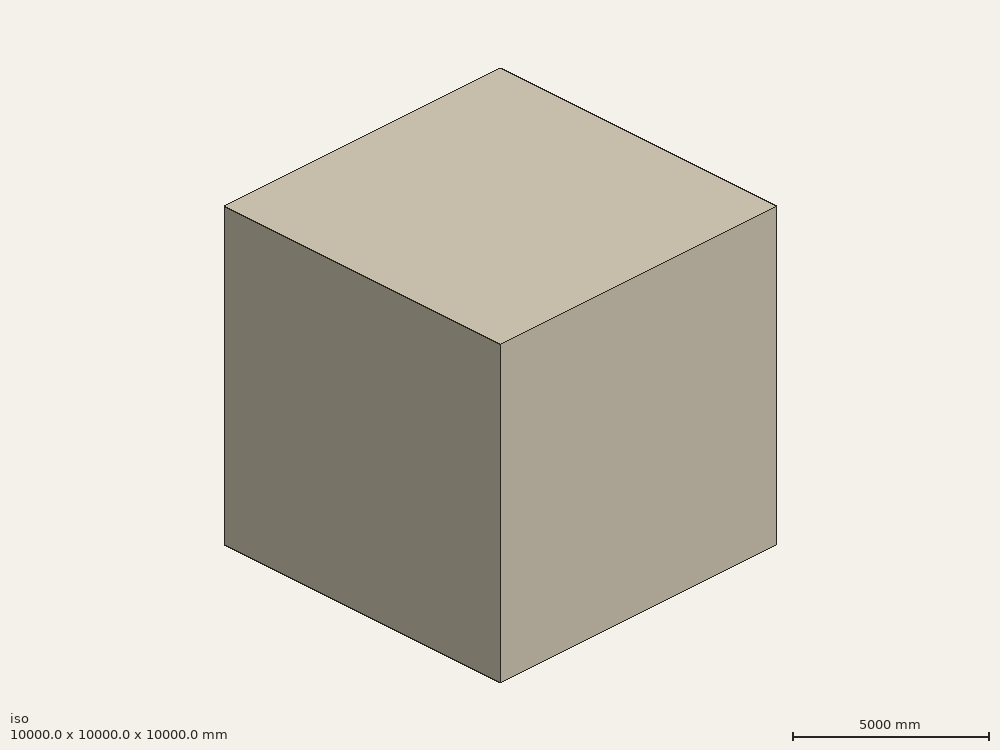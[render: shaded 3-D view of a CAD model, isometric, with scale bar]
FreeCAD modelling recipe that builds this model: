
FCSTD DOCUMENT  (FreeCAD 0.21R33694 (Git))
Label: vol31
License: All rights reserved
objects: App::DocumentObjectGroupPython×1265, Part::FeaturePython×4, App::Part×2, Part::Fuse×1, Part::Cut×1
note: 6 computed .brp shape members not serialized (recipe doc carries the construction recipe); baked Part::Feature solids carry a one-line shape summary decoded from their .brp

FEATURE [App::DocumentObjectGroupPython] HALFPI  # scripted group (container) (typed FeaturePython)
  name = HALFPI
  value = pi/2.
FEATURE [App::DocumentObjectGroupPython] PI  # scripted group (container) (typed FeaturePython)
  name = PI
  value = 1.*pi
FEATURE [App::DocumentObjectGroupPython] TWOPI  # scripted group (container) (typed FeaturePython)
  name = TWOPI
  value = 2.*pi
FEATURE [App::DocumentObjectGroupPython] Constants  # scripted group (container) (typed FeaturePython)
  Group = -> [HALFPI,PI,TWOPI]
FEATURE [App::DocumentObjectGroupPython] Variables  # scripted group (container) (typed FeaturePython)
FEATURE [App::DocumentObjectGroupPython] ro  # scripted group (container) (typed FeaturePython)
  name = ro
  type = density
  unit = g/cm3
  value = 1234
FEATURE [App::DocumentObjectGroupPython] sizeoft500  # scripted group (container) (typed FeaturePython)
  name = sizeoft500
  type = length
  unit = mm
  value = 500
FEATURE [App::DocumentObjectGroupPython] wextent  # scripted group (container) (typed FeaturePython)
  name = wextent
  type = length
  unit = mm
  value = 10000
FEATURE [App::DocumentObjectGroupPython] Quantities  # scripted group (container) (typed FeaturePython)
  Group = -> [ro,sizeoft500,wextent]
FEATURE [App::DocumentObjectGroupPython] Isotopes  # scripted group (container) (typed FeaturePython)
FEATURE [App::DocumentObjectGroupPython] Hydrogen  # scripted group (container) (typed FeaturePython)
  Z = 1
  atom_value = 1.01
  formula = H
  name = Hydrogen
FEATURE [App::DocumentObjectGroupPython] Oxygen  # scripted group (container) (typed FeaturePython)
  Z = 8
  atom_value = 16
  formula = O
  name = Oxygen
FEATURE [App::DocumentObjectGroupPython] Nitrogen  # scripted group (container) (typed FeaturePython)
  Z = 7
  atom_value = 14.01
  formula = N
  name = Nitrogen
FEATURE [App::DocumentObjectGroupPython] Lead  # scripted group (container) (typed FeaturePython)
  Z = 82
  atom_value = 207.2
  formula = Pb
  name = Lead
FEATURE [App::DocumentObjectGroupPython] Elements  # scripted group (container) (typed FeaturePython)
  Group = -> [Hydrogen,Oxygen,Nitrogen,Lead]
FEATURE [App::DocumentObjectGroupPython] Al  # scripted group (container) (typed FeaturePython)
  Dvalue = 2.7
  Z = 13
  atom_value = 26.98
  conduct = 2
  density = 1
  expand = 3
  name = Al
  specific = 4
FEATURE [App::DocumentObjectGroupPython] Hydrogen001  label="Hydrogen : 2"  # scripted group (container) (typed FeaturePython)
  n = 2
  ref = Hydrogen
FEATURE [App::DocumentObjectGroupPython] Oxygen001  label="Oxygen : 1"  # scripted group (container) (typed FeaturePython)
  n = 1
  ref = Oxygen
FEATURE [App::DocumentObjectGroupPython] Water  # scripted group (container) (typed FeaturePython)
  Dvalue = 1
  Group = -> [Hydrogen001,Oxygen001]
  conduct = 2
  density = 1
  expand = 3
  formula = H20
  name = Water
  specific = 4
FEATURE [App::DocumentObjectGroupPython] Nitrogen001  label="Nitrogen : 0.700"  # scripted group (container) (typed FeaturePython)
  n = 0.7
FEATURE [App::DocumentObjectGroupPython] Oxygen002  label="Oxygen : 0.300"  # scripted group (container) (typed FeaturePython)
  n = 0.3
FEATURE [App::DocumentObjectGroupPython] Air  # scripted group (container) (typed FeaturePython)
  Dunit = mg/cm3
  Dvalue = 1.29
  Group = -> [Nitrogen001,Oxygen002]
  conduct = 2
  density = 1
  expand = 3
  name = Air
  specific = 4
FEATURE [App::DocumentObjectGroupPython] Matrix  # scripted group (container) (typed FeaturePython)
FEATURE [App::DocumentObjectGroupPython] Surfaces  # scripted group (container) (typed FeaturePython)
FEATURE [App::DocumentObjectGroupPython] Opticals  # scripted group (container) (typed FeaturePython)
  Group = -> [Matrix,Surfaces]
FEATURE [App::DocumentObjectGroupPython] G4Isotopes  # scripted group (container) (typed FeaturePython)
FEATURE [App::DocumentObjectGroupPython] H_element  # scripted group (container) (typed FeaturePython)
  Z = 1
  atom_value = 1.008
  formula = H
  name = H_element
FEATURE [App::DocumentObjectGroupPython] He_element  # scripted group (container) (typed FeaturePython)
  Z = 2
  atom_value = 4.0026
  formula = He
  name = He_element
FEATURE [App::DocumentObjectGroupPython] Li_element  # scripted group (container) (typed FeaturePython)
  Z = 3
  atom_value = 6.94
  formula = Li
  name = Li_element
FEATURE [App::DocumentObjectGroupPython] Be_element  # scripted group (container) (typed FeaturePython)
  Z = 4
  atom_value = 9.01218
  formula = Be
  name = Be_element
FEATURE [App::DocumentObjectGroupPython] B_element  # scripted group (container) (typed FeaturePython)
  Z = 5
  atom_value = 10.81
  formula = B
  name = B_element
FEATURE [App::DocumentObjectGroupPython] C_element  # scripted group (container) (typed FeaturePython)
  Z = 6
  atom_value = 12.011
  formula = C
  name = C_element
FEATURE [App::DocumentObjectGroupPython] N_element  # scripted group (container) (typed FeaturePython)
  Z = 7
  atom_value = 14.007
  formula = N
  name = N_element
FEATURE [App::DocumentObjectGroupPython] O_element  # scripted group (container) (typed FeaturePython)
  Z = 8
  atom_value = 15.999
  formula = O
  name = O_element
FEATURE [App::DocumentObjectGroupPython] F_element  # scripted group (container) (typed FeaturePython)
  Z = 9
  atom_value = 18.9984
  formula = F
  name = F_element
FEATURE [App::DocumentObjectGroupPython] Ne_element  # scripted group (container) (typed FeaturePython)
  Z = 10
  atom_value = 20.1797
  formula = Ne
  name = Ne_element
FEATURE [App::DocumentObjectGroupPython] Na_element  # scripted group (container) (typed FeaturePython)
  Z = 11
  atom_value = 22.9898
  formula = Na
  name = Na_element
FEATURE [App::DocumentObjectGroupPython] Mg_element  # scripted group (container) (typed FeaturePython)
  Z = 12
  atom_value = 24.305
  formula = Mg
  name = Mg_element
FEATURE [App::DocumentObjectGroupPython] Al_element  # scripted group (container) (typed FeaturePython)
  Z = 13
  atom_value = 26.9815
  formula = Al
  name = Al_element
FEATURE [App::DocumentObjectGroupPython] Si_element  # scripted group (container) (typed FeaturePython)
  Z = 14
  atom_value = 28.085
  formula = Si
  name = Si_element
FEATURE [App::DocumentObjectGroupPython] P_element  # scripted group (container) (typed FeaturePython)
  Z = 15
  atom_value = 30.9738
  formula = P
  name = P_element
FEATURE [App::DocumentObjectGroupPython] S_element  # scripted group (container) (typed FeaturePython)
  Z = 16
  atom_value = 32.06
  formula = S
  name = S_element
FEATURE [App::DocumentObjectGroupPython] Cl_element  # scripted group (container) (typed FeaturePython)
  Z = 17
  atom_value = 35.45
  formula = Cl
  name = Cl_element
FEATURE [App::DocumentObjectGroupPython] Ar_element  # scripted group (container) (typed FeaturePython)
  Z = 18
  atom_value = 39.95
  formula = Ar
  name = Ar_element
FEATURE [App::DocumentObjectGroupPython] K_element  # scripted group (container) (typed FeaturePython)
  Z = 19
  atom_value = 39.0983
  formula = K
  name = K_element
FEATURE [App::DocumentObjectGroupPython] Ca_element  # scripted group (container) (typed FeaturePython)
  Z = 20
  atom_value = 40.078
  formula = Ca
  name = Ca_element
FEATURE [App::DocumentObjectGroupPython] Sc_element  # scripted group (container) (typed FeaturePython)
  Z = 21
  atom_value = 44.9559
  formula = Sc
  name = Sc_element
FEATURE [App::DocumentObjectGroupPython] Ti_element  # scripted group (container) (typed FeaturePython)
  Z = 22
  atom_value = 47.867
  formula = Ti
  name = Ti_element
FEATURE [App::DocumentObjectGroupPython] V_element  # scripted group (container) (typed FeaturePython)
  Z = 23
  atom_value = 50.9415
  formula = V
  name = V_element
FEATURE [App::DocumentObjectGroupPython] Cr_element  # scripted group (container) (typed FeaturePython)
  Z = 24
  atom_value = 51.9961
  formula = Cr
  name = Cr_element
FEATURE [App::DocumentObjectGroupPython] Mn_element  # scripted group (container) (typed FeaturePython)
  Z = 25
  atom_value = 54.938
  formula = Mn
  name = Mn_element
FEATURE [App::DocumentObjectGroupPython] Fe_element  # scripted group (container) (typed FeaturePython)
  Z = 26
  atom_value = 55.845
  formula = Fe
  name = Fe_element
FEATURE [App::DocumentObjectGroupPython] Co_element  # scripted group (container) (typed FeaturePython)
  Z = 27
  atom_value = 58.9332
  formula = Co
  name = Co_element
FEATURE [App::DocumentObjectGroupPython] Ni_element  # scripted group (container) (typed FeaturePython)
  Z = 28
  atom_value = 58.6934
  formula = Ni
  name = Ni_element
FEATURE [App::DocumentObjectGroupPython] Cu_element  # scripted group (container) (typed FeaturePython)
  Z = 29
  atom_value = 63.546
  formula = Cu
  name = Cu_element
FEATURE [App::DocumentObjectGroupPython] Zn_element  # scripted group (container) (typed FeaturePython)
  Z = 30
  atom_value = 65.38
  formula = Zn
  name = Zn_element
FEATURE [App::DocumentObjectGroupPython] Ga_element  # scripted group (container) (typed FeaturePython)
  Z = 31
  atom_value = 69.723
  formula = Ga
  name = Ga_element
FEATURE [App::DocumentObjectGroupPython] Ge_element  # scripted group (container) (typed FeaturePython)
  Z = 32
  atom_value = 72.63
  formula = Ge
  name = Ge_element
FEATURE [App::DocumentObjectGroupPython] As_element  # scripted group (container) (typed FeaturePython)
  Z = 33
  atom_value = 74.9216
  formula = As
  name = As_element
FEATURE [App::DocumentObjectGroupPython] Se_element  # scripted group (container) (typed FeaturePython)
  Z = 34
  atom_value = 78.971
  formula = Se
  name = Se_element
FEATURE [App::DocumentObjectGroupPython] Br_element  # scripted group (container) (typed FeaturePython)
  Z = 35
  atom_value = 79.904
  formula = Br
  name = Br_element
FEATURE [App::DocumentObjectGroupPython] Kr_element  # scripted group (container) (typed FeaturePython)
  Z = 36
  atom_value = 83.798
  formula = Kr
  name = Kr_element
FEATURE [App::DocumentObjectGroupPython] Rb_element  # scripted group (container) (typed FeaturePython)
  Z = 37
  atom_value = 85.4678
  formula = Rb
  name = Rb_element
FEATURE [App::DocumentObjectGroupPython] Sr_element  # scripted group (container) (typed FeaturePython)
  Z = 38
  atom_value = 87.62
  formula = Sr
  name = Sr_element
FEATURE [App::DocumentObjectGroupPython] Y_element  # scripted group (container) (typed FeaturePython)
  Z = 39
  atom_value = 88.9058
  formula = Y
  name = Y_element
FEATURE [App::DocumentObjectGroupPython] Zr_element  # scripted group (container) (typed FeaturePython)
  Z = 40
  atom_value = 91.224
  formula = Zr
  name = Zr_element
FEATURE [App::DocumentObjectGroupPython] Nb_element  # scripted group (container) (typed FeaturePython)
  Z = 41
  atom_value = 92.9064
  formula = Nb
  name = Nb_element
FEATURE [App::DocumentObjectGroupPython] Mo_element  # scripted group (container) (typed FeaturePython)
  Z = 42
  atom_value = 95.95
  formula = Mo
  name = Mo_element
FEATURE [App::DocumentObjectGroupPython] Tc_element  # scripted group (container) (typed FeaturePython)
  Z = 43
  atom_value = 97
  formula = Tc
  name = Tc_element
FEATURE [App::DocumentObjectGroupPython] Ru_element  # scripted group (container) (typed FeaturePython)
  Z = 44
  atom_value = 101.07
  formula = Ru
  name = Ru_element
FEATURE [App::DocumentObjectGroupPython] Rh_element  # scripted group (container) (typed FeaturePython)
  Z = 45
  atom_value = 102.905
  formula = Rh
  name = Rh_element
FEATURE [App::DocumentObjectGroupPython] Pd_element  # scripted group (container) (typed FeaturePython)
  Z = 46
  atom_value = 106.42
  formula = Pd
  name = Pd_element
FEATURE [App::DocumentObjectGroupPython] Ag_element  # scripted group (container) (typed FeaturePython)
  Z = 47
  atom_value = 107.868
  formula = Ag
  name = Ag_element
FEATURE [App::DocumentObjectGroupPython] Cd_element  # scripted group (container) (typed FeaturePython)
  Z = 48
  atom_value = 112.414
  formula = Cd
  name = Cd_element
FEATURE [App::DocumentObjectGroupPython] In_element  # scripted group (container) (typed FeaturePython)
  Z = 49
  atom_value = 114.818
  formula = In
  name = In_element
FEATURE [App::DocumentObjectGroupPython] Sn_element  # scripted group (container) (typed FeaturePython)
  Z = 50
  atom_value = 118.71
  formula = Sn
  name = Sn_element
FEATURE [App::DocumentObjectGroupPython] Sb_element  # scripted group (container) (typed FeaturePython)
  Z = 51
  atom_value = 121.76
  formula = Sb
  name = Sb_element
FEATURE [App::DocumentObjectGroupPython] Te_element  # scripted group (container) (typed FeaturePython)
  Z = 52
  atom_value = 127.6
  formula = Te
  name = Te_element
FEATURE [App::DocumentObjectGroupPython] I_element  # scripted group (container) (typed FeaturePython)
  Z = 53
  atom_value = 126.904
  formula = I
  name = I_element
FEATURE [App::DocumentObjectGroupPython] Xe_element  # scripted group (container) (typed FeaturePython)
  Z = 54
  atom_value = 131.293
  formula = Xe
  name = Xe_element
FEATURE [App::DocumentObjectGroupPython] Cs_element  # scripted group (container) (typed FeaturePython)
  Z = 55
  atom_value = 132.905
  formula = Cs
  name = Cs_element
FEATURE [App::DocumentObjectGroupPython] Ba_element  # scripted group (container) (typed FeaturePython)
  Z = 56
  atom_value = 137.327
  formula = Ba
  name = Ba_element
FEATURE [App::DocumentObjectGroupPython] La_element  # scripted group (container) (typed FeaturePython)
  Z = 57
  atom_value = 138.905
  formula = La
  name = La_element
FEATURE [App::DocumentObjectGroupPython] Ce_element  # scripted group (container) (typed FeaturePython)
  Z = 58
  atom_value = 140.116
  formula = Ce
  name = Ce_element
FEATURE [App::DocumentObjectGroupPython] Pr_element  # scripted group (container) (typed FeaturePython)
  Z = 59
  atom_value = 140.908
  formula = Pr
  name = Pr_element
FEATURE [App::DocumentObjectGroupPython] Nd_element  # scripted group (container) (typed FeaturePython)
  Z = 60
  atom_value = 144.242
  formula = Nd
  name = Nd_element
FEATURE [App::DocumentObjectGroupPython] Pm_element  # scripted group (container) (typed FeaturePython)
  Z = 61
  atom_value = 145
  formula = Pm
  name = Pm_element
FEATURE [App::DocumentObjectGroupPython] Sm_element  # scripted group (container) (typed FeaturePython)
  Z = 62
  atom_value = 150.36
  formula = Sm
  name = Sm_element
FEATURE [App::DocumentObjectGroupPython] Eu_element  # scripted group (container) (typed FeaturePython)
  Z = 63
  atom_value = 151.964
  formula = Eu
  name = Eu_element
FEATURE [App::DocumentObjectGroupPython] Gd_element  # scripted group (container) (typed FeaturePython)
  Z = 64
  atom_value = 157.25
  formula = Gd
  name = Gd_element
FEATURE [App::DocumentObjectGroupPython] Tb_element  # scripted group (container) (typed FeaturePython)
  Z = 65
  atom_value = 158.925
  formula = Tb
  name = Tb_element
FEATURE [App::DocumentObjectGroupPython] Dy_element  # scripted group (container) (typed FeaturePython)
  Z = 66
  atom_value = 162.5
  formula = Dy
  name = Dy_element
FEATURE [App::DocumentObjectGroupPython] Ho_element  # scripted group (container) (typed FeaturePython)
  Z = 67
  atom_value = 164.93
  formula = Ho
  name = Ho_element
FEATURE [App::DocumentObjectGroupPython] Er_element  # scripted group (container) (typed FeaturePython)
  Z = 68
  atom_value = 167.259
  formula = Er
  name = Er_element
FEATURE [App::DocumentObjectGroupPython] Tm_element  # scripted group (container) (typed FeaturePython)
  Z = 69
  atom_value = 168.934
  formula = Tm
  name = Tm_element
FEATURE [App::DocumentObjectGroupPython] Yb_element  # scripted group (container) (typed FeaturePython)
  Z = 70
  atom_value = 173.045
  formula = Yb
  name = Yb_element
FEATURE [App::DocumentObjectGroupPython] Lu_element  # scripted group (container) (typed FeaturePython)
  Z = 71
  atom_value = 174.967
  formula = Lu
  name = Lu_element
FEATURE [App::DocumentObjectGroupPython] Hf_element  # scripted group (container) (typed FeaturePython)
  Z = 72
  atom_value = 178.49
  formula = Hf
  name = Hf_element
FEATURE [App::DocumentObjectGroupPython] Ta_element  # scripted group (container) (typed FeaturePython)
  Z = 73
  atom_value = 180.948
  formula = Ta
  name = Ta_element
FEATURE [App::DocumentObjectGroupPython] W_element  # scripted group (container) (typed FeaturePython)
  Z = 74
  atom_value = 183.84
  formula = W
  name = W_element
FEATURE [App::DocumentObjectGroupPython] Re_element  # scripted group (container) (typed FeaturePython)
  Z = 75
  atom_value = 186.207
  formula = Re
  name = Re_element
FEATURE [App::DocumentObjectGroupPython] Os_element  # scripted group (container) (typed FeaturePython)
  Z = 76
  atom_value = 190.23
  formula = Os
  name = Os_element
FEATURE [App::DocumentObjectGroupPython] Ir_element  # scripted group (container) (typed FeaturePython)
  Z = 77
  atom_value = 192.217
  formula = Ir
  name = Ir_element
FEATURE [App::DocumentObjectGroupPython] Pt_element  # scripted group (container) (typed FeaturePython)
  Z = 78
  atom_value = 195.084
  formula = Pt
  name = Pt_element
FEATURE [App::DocumentObjectGroupPython] Au_element  # scripted group (container) (typed FeaturePython)
  Z = 79
  atom_value = 196.967
  formula = Au
  name = Au_element
FEATURE [App::DocumentObjectGroupPython] Hg_element  # scripted group (container) (typed FeaturePython)
  Z = 80
  atom_value = 200.592
  formula = Hg
  name = Hg_element
FEATURE [App::DocumentObjectGroupPython] Tl_element  # scripted group (container) (typed FeaturePython)
  Z = 81
  atom_value = 204.38
  formula = Tl
  name = Tl_element
FEATURE [App::DocumentObjectGroupPython] Pb_element  # scripted group (container) (typed FeaturePython)
  Z = 82
  atom_value = 207.2
  formula = Pb
  name = Pb_element
FEATURE [App::DocumentObjectGroupPython] Bi_element  # scripted group (container) (typed FeaturePython)
  Z = 83
  atom_value = 208.98
  formula = Bi
  name = Bi_element
FEATURE [App::DocumentObjectGroupPython] Po_element  # scripted group (container) (typed FeaturePython)
  Z = 84
  atom_value = 209
  formula = Po
  name = Po_element
FEATURE [App::DocumentObjectGroupPython] At_element  # scripted group (container) (typed FeaturePython)
  Z = 85
  atom_value = 210
  formula = At
  name = At_element
FEATURE [App::DocumentObjectGroupPython] Rn_element  # scripted group (container) (typed FeaturePython)
  Z = 86
  atom_value = 222
  formula = Rn
  name = Rn_element
FEATURE [App::DocumentObjectGroupPython] Fr_element  # scripted group (container) (typed FeaturePython)
  Z = 87
  atom_value = 223
  formula = Fr
  name = Fr_element
FEATURE [App::DocumentObjectGroupPython] Ra_element  # scripted group (container) (typed FeaturePython)
  Z = 88
  atom_value = 226
  formula = Ra
  name = Ra_element
FEATURE [App::DocumentObjectGroupPython] Ac_element  # scripted group (container) (typed FeaturePython)
  Z = 89
  atom_value = 227
  formula = Ac
  name = Ac_element
FEATURE [App::DocumentObjectGroupPython] Th_element  # scripted group (container) (typed FeaturePython)
  Z = 90
  atom_value = 232.038
  formula = Th
  name = Th_element
FEATURE [App::DocumentObjectGroupPython] Pa_element  # scripted group (container) (typed FeaturePython)
  Z = 91
  atom_value = 231.036
  formula = Pa
  name = Pa_element
FEATURE [App::DocumentObjectGroupPython] U_element  # scripted group (container) (typed FeaturePython)
  Z = 92
  atom_value = 238.029
  formula = U
  name = U_element
FEATURE [App::DocumentObjectGroupPython] Np_element  # scripted group (container) (typed FeaturePython)
  Z = 93
  atom_value = 237
  formula = Np
  name = Np_element
FEATURE [App::DocumentObjectGroupPython] Pu_element  # scripted group (container) (typed FeaturePython)
  Z = 94
  atom_value = 244
  formula = Pu
  name = Pu_element
FEATURE [App::DocumentObjectGroupPython] Am_element  # scripted group (container) (typed FeaturePython)
  Z = 95
  atom_value = 243
  formula = Am
  name = Am_element
FEATURE [App::DocumentObjectGroupPython] Cm_element  # scripted group (container) (typed FeaturePython)
  Z = 96
  atom_value = 247
  formula = Cm
  name = Cm_element
FEATURE [App::DocumentObjectGroupPython] Bk_element  # scripted group (container) (typed FeaturePython)
  Z = 97
  atom_value = 247
  formula = Bk
  name = Bk_element
FEATURE [App::DocumentObjectGroupPython] Cf_element  # scripted group (container) (typed FeaturePython)
  Z = 98
  atom_value = 251
  formula = Cf
  name = Cf_element
FEATURE [App::DocumentObjectGroupPython] G4Elements  # scripted group (container) (typed FeaturePython)
  Group = -> [H_element,He_element,Li_element,Be_element,B_element,C_element,N_element,O_element,F_element,Ne_element,Na_element,Mg_element,Al_element,Si_element,P_element,S_element,Cl_element,Ar_element,K_element,Ca_element,Sc_element,Ti_element,V_element,Cr_element,Mn_element,Fe_element,Co_element,Ni_element,Cu_element,Zn_element,Ga_element,Ge_element,As_element,Se_element,Br_element,Kr_element,Rb_element,+61 more]
FEATURE [App::DocumentObjectGroupPython] H_element001  label="H_element : 0.101"  # scripted group (container) (typed FeaturePython)
  n = 0.101327
FEATURE [App::DocumentObjectGroupPython] C_element001  label="C_element : 0.775"  # scripted group (container) (typed FeaturePython)
  n = 0.7755
FEATURE [App::DocumentObjectGroupPython] N_element001  label="N_element : 0.035"  # scripted group (container) (typed FeaturePython)
  n = 0.035057
FEATURE [App::DocumentObjectGroupPython] O_element001  label="O_element : 0.052"  # scripted group (container) (typed FeaturePython)
  n = 0.0523159
FEATURE [App::DocumentObjectGroupPython] F_element001  label="F_element : 0.017"  # scripted group (container) (typed FeaturePython)
  n = 0.017422
FEATURE [App::DocumentObjectGroupPython] Ca_element001  label="Ca_element : 0.018"  # scripted group (container) (typed FeaturePython)
  n = 0.018378
FEATURE [App::DocumentObjectGroupPython] G4_A_150_TISSUE  label="G4_A-150_TISSUE"  # scripted group (container) (typed FeaturePython)
  Dunit = g/cm3
  Dvalue = 1.127
  Group = -> [H_element001,C_element001,N_element001,O_element001,F_element001,Ca_element001]
  conduct = 2
  density = 1
  expand = 3
  formula = G4_A-150_TISSUE
  name = G4_A-150_TISSUE
  specific = 4
FEATURE [App::DocumentObjectGroupPython] C_element002  label="C_element : 3"  # scripted group (container) (typed FeaturePython)
  n = 3
  ref = C_element
FEATURE [App::DocumentObjectGroupPython] H_element002  label="H_element : 6"  # scripted group (container) (typed FeaturePython)
  n = 6
  ref = H_element
FEATURE [App::DocumentObjectGroupPython] O_element002  label="O_element : 1"  # scripted group (container) (typed FeaturePython)
  n = 1
  ref = O_element
FEATURE [App::DocumentObjectGroupPython] G4_ACETONE  # scripted group (container) (typed FeaturePython)
  Dunit = g/cm3
  Dvalue = 0.7899
  Group = -> [C_element002,H_element002,O_element002]
  conduct = 2
  density = 1
  expand = 3
  formula = G4_ACETONE
  name = G4_ACETONE
  specific = 4
FEATURE [App::DocumentObjectGroupPython] C_element003  label="C_element : 2"  # scripted group (container) (typed FeaturePython)
  n = 2
  ref = C_element
FEATURE [App::DocumentObjectGroupPython] H_element003  label="H_element : 2"  # scripted group (container) (typed FeaturePython)
  n = 2
  ref = H_element
FEATURE [App::DocumentObjectGroupPython] G4_ACETYLENE  # scripted group (container) (typed FeaturePython)
  Dunit = g/cm3
  Dvalue = 0.0010967
  Group = -> [C_element003,H_element003]
  conduct = 2
  density = 1
  expand = 3
  formula = G4_ACETYLENE
  name = G4_ACETYLENE
  specific = 4
FEATURE [App::DocumentObjectGroupPython] C_element004  label="C_element : 5"  # scripted group (container) (typed FeaturePython)
  n = 5
  ref = C_element
FEATURE [App::DocumentObjectGroupPython] H_element004  label="H_element : 5"  # scripted group (container) (typed FeaturePython)
  n = 5
  ref = H_element
FEATURE [App::DocumentObjectGroupPython] N_element002  label="N_element : 5"  # scripted group (container) (typed FeaturePython)
  n = 5
  ref = N_element
FEATURE [App::DocumentObjectGroupPython] G4_ADENINE  # scripted group (container) (typed FeaturePython)
  Dunit = g/cm3
  Dvalue = 1.6
  Group = -> [C_element004,H_element004,N_element002]
  conduct = 2
  density = 1
  expand = 3
  formula = G4_ADENINE
  name = G4_ADENINE
  specific = 4
FEATURE [App::DocumentObjectGroupPython] H_element005  label="H_element : 0.114"  # scripted group (container) (typed FeaturePython)
  n = 0.114
FEATURE [App::DocumentObjectGroupPython] C_element005  label="C_element : 0.598"  # scripted group (container) (typed FeaturePython)
  n = 0.598
FEATURE [App::DocumentObjectGroupPython] N_element003  label="N_element : 0.007"  # scripted group (container) (typed FeaturePython)
  n = 0.007
FEATURE [App::DocumentObjectGroupPython] O_element003  label="O_element : 0.278"  # scripted group (container) (typed FeaturePython)
  n = 0.278
FEATURE [App::DocumentObjectGroupPython] Na_element001  label="Na_element : 0.001"  # scripted group (container) (typed FeaturePython)
  n = 0.001
FEATURE [App::DocumentObjectGroupPython] S_element001  label="S_element : 0.001"  # scripted group (container) (typed FeaturePython)
  n = 0.001
FEATURE [App::DocumentObjectGroupPython] Cl_element001  label="Cl_element : 0.001"  # scripted group (container) (typed FeaturePython)
  n = 0.001
FEATURE [App::DocumentObjectGroupPython] G4_ADIPOSE_TISSUE_ICRP  # scripted group (container) (typed FeaturePython)
  Dunit = g/cm3
  Dvalue = 0.95
  Group = -> [H_element005,C_element005,N_element003,O_element003,Na_element001,S_element001,Cl_element001]
  conduct = 2
  density = 1
  expand = 3
  formula = G4_ADIPOSE_TISSUE_ICRP
  name = G4_ADIPOSE_TISSUE_ICRP
  specific = 4
FEATURE [App::DocumentObjectGroupPython] C_element006  label="C_element : 0.000"  # scripted group (container) (typed FeaturePython)
  n = 0.000124
FEATURE [App::DocumentObjectGroupPython] N_element004  label="N_element : 0.755"  # scripted group (container) (typed FeaturePython)
  n = 0.755268
FEATURE [App::DocumentObjectGroupPython] O_element004  label="O_element : 0.232"  # scripted group (container) (typed FeaturePython)
  n = 0.231781
FEATURE [App::DocumentObjectGroupPython] Ar_element001  label="Ar_element : 0.013"  # scripted group (container) (typed FeaturePython)
  n = 0.012827
FEATURE [App::DocumentObjectGroupPython] G4_AIR  # scripted group (container) (typed FeaturePython)
  Dunit = g/cm3
  Dvalue = 0.00120479
  Group = -> [C_element006,N_element004,O_element004,Ar_element001]
  conduct = 2
  density = 1
  expand = 3
  formula = G4_AIR
  name = G4_AIR
  specific = 4
FEATURE [App::DocumentObjectGroupPython] C_element007  label="C_element : 006"  # scripted group (container) (typed FeaturePython)
  n = 3
  ref = C_element
FEATURE [App::DocumentObjectGroupPython] H_element006  label="H_element : 7"  # scripted group (container) (typed FeaturePython)
  n = 7
  ref = H_element
FEATURE [App::DocumentObjectGroupPython] N_element005  label="N_element : 1"  # scripted group (container) (typed FeaturePython)
  n = 1
  ref = N_element
FEATURE [App::DocumentObjectGroupPython] O_element005  label="O_element : 2"  # scripted group (container) (typed FeaturePython)
  n = 2
  ref = O_element
FEATURE [App::DocumentObjectGroupPython] G4_ALANINE  # scripted group (container) (typed FeaturePython)
  Dunit = g/cm3
  Dvalue = 1.42
  Group = -> [C_element007,H_element006,N_element005,O_element005]
  conduct = 2
  density = 1
  expand = 3
  formula = G4_ALANINE
  name = G4_ALANINE
  specific = 4
FEATURE [App::DocumentObjectGroupPython] Al_element001  label="Al_element : 2"  # scripted group (container) (typed FeaturePython)
  n = 2
  ref = Al_element
FEATURE [App::DocumentObjectGroupPython] O_element006  label="O_element : 3"  # scripted group (container) (typed FeaturePython)
  n = 3
  ref = O_element
FEATURE [App::DocumentObjectGroupPython] G4_ALUMINUM_OXIDE  # scripted group (container) (typed FeaturePython)
  Dunit = g/cm3
  Dvalue = 3.97
  Group = -> [Al_element001,O_element006]
  conduct = 2
  density = 1
  expand = 3
  formula = G4_ALUMINUM_OXIDE
  name = G4_ALUMINUM_OXIDE
  specific = 4
FEATURE [App::DocumentObjectGroupPython] H_element007  label="H_element : 0.106"  # scripted group (container) (typed FeaturePython)
  n = 0.10593
FEATURE [App::DocumentObjectGroupPython] C_element008  label="C_element : 0.789"  # scripted group (container) (typed FeaturePython)
  n = 0.788974
FEATURE [App::DocumentObjectGroupPython] O_element007  label="O_element : 0.105"  # scripted group (container) (typed FeaturePython)
  n = 0.105096
FEATURE [App::DocumentObjectGroupPython] G4_AMBER  # scripted group (container) (typed FeaturePython)
  Dunit = g/cm3
  Dvalue = 1.1
  Group = -> [H_element007,C_element008,O_element007]
  conduct = 2
  density = 1
  expand = 3
  formula = G4_AMBER
  name = G4_AMBER
  specific = 4
FEATURE [App::DocumentObjectGroupPython] N_element006  label="N_element : 006"  # scripted group (container) (typed FeaturePython)
  n = 1
  ref = N_element
FEATURE [App::DocumentObjectGroupPython] H_element008  label="H_element : 3"  # scripted group (container) (typed FeaturePython)
  n = 3
  ref = H_element
FEATURE [App::DocumentObjectGroupPython] G4_AMMONIA  # scripted group (container) (typed FeaturePython)
  Dunit = g/cm3
  Dvalue = 0.000826019
  Group = -> [N_element006,H_element008]
  conduct = 2
  density = 1
  expand = 3
  formula = G4_AMMONIA
  name = G4_AMMONIA
  specific = 4
FEATURE [App::DocumentObjectGroupPython] C_element009  label="C_element : 6"  # scripted group (container) (typed FeaturePython)
  n = 6
  ref = C_element
FEATURE [App::DocumentObjectGroupPython] H_element009  label="H_element : 008"  # scripted group (container) (typed FeaturePython)
  n = 7
  ref = H_element
FEATURE [App::DocumentObjectGroupPython] N_element007  label="N_element : 007"  # scripted group (container) (typed FeaturePython)
  n = 1
  ref = N_element
FEATURE [App::DocumentObjectGroupPython] G4_ANILINE  # scripted group (container) (typed FeaturePython)
  Dunit = g/cm3
  Dvalue = 1.0235
  Group = -> [C_element009,H_element009,N_element007]
  conduct = 2
  density = 1
  expand = 3
  formula = G4_ANILINE
  name = G4_ANILINE
  specific = 4
FEATURE [App::DocumentObjectGroupPython] C_element010  label="C_element : 14"  # scripted group (container) (typed FeaturePython)
  n = 14
  ref = C_element
FEATURE [App::DocumentObjectGroupPython] H_element010  label="H_element : 10"  # scripted group (container) (typed FeaturePython)
  n = 10
  ref = H_element
FEATURE [App::DocumentObjectGroupPython] G4_ANTHRACENE  # scripted group (container) (typed FeaturePython)
  Dunit = g/cm3
  Dvalue = 1.283
  Group = -> [C_element010,H_element010]
  conduct = 2
  density = 1
  expand = 3
  formula = G4_ANTHRACENE
  name = G4_ANTHRACENE
  specific = 4
FEATURE [App::DocumentObjectGroupPython] H_element011  label="H_element : 0.065"  # scripted group (container) (typed FeaturePython)
  n = 0.0654709
FEATURE [App::DocumentObjectGroupPython] C_element011  label="C_element : 0.537"  # scripted group (container) (typed FeaturePython)
  n = 0.536944
FEATURE [App::DocumentObjectGroupPython] N_element008  label="N_element : 0.021"  # scripted group (container) (typed FeaturePython)
  n = 0.0215
FEATURE [App::DocumentObjectGroupPython] O_element008  label="O_element : 0.032"  # scripted group (container) (typed FeaturePython)
  n = 0.032085
FEATURE [App::DocumentObjectGroupPython] F_element002  label="F_element : 0.167"  # scripted group (container) (typed FeaturePython)
  n = 0.167411
FEATURE [App::DocumentObjectGroupPython] Ca_element002  label="Ca_element : 0.177"  # scripted group (container) (typed FeaturePython)
  n = 0.176589
FEATURE [App::DocumentObjectGroupPython] G4_B_100_BONE  label="G4_B-100_BONE"  # scripted group (container) (typed FeaturePython)
  Dunit = g/cm3
  Dvalue = 1.45
  Group = -> [H_element011,C_element011,N_element008,O_element008,F_element002,Ca_element002]
  conduct = 2
  density = 1
  expand = 3
  formula = G4_B-100_BONE
  name = G4_B-100_BONE
  specific = 4
FEATURE [App::DocumentObjectGroupPython] H_element012  label="H_element : 0.057"  # scripted group (container) (typed FeaturePython)
  n = 0.057441
FEATURE [App::DocumentObjectGroupPython] C_element012  label="C_element : 0.790"  # scripted group (container) (typed FeaturePython)
  n = 0.774591
FEATURE [App::DocumentObjectGroupPython] O_element009  label="O_element : 0.168"  # scripted group (container) (typed FeaturePython)
  n = 0.167968
FEATURE [App::DocumentObjectGroupPython] G4_BAKELITE  # scripted group (container) (typed FeaturePython)
  Dunit = g/cm3
  Dvalue = 1.25
  Group = -> [H_element012,C_element012,O_element009]
  conduct = 2
  density = 1
  expand = 3
  formula = G4_BAKELITE
  name = G4_BAKELITE
  specific = 4
FEATURE [App::DocumentObjectGroupPython] Ba_element001  label="Ba_element : 1"  # scripted group (container) (typed FeaturePython)
  n = 1
  ref = Ba_element
FEATURE [App::DocumentObjectGroupPython] F_element003  label="F_element : 2"  # scripted group (container) (typed FeaturePython)
  n = 2
  ref = F_element
FEATURE [App::DocumentObjectGroupPython] G4_BARIUM_FLUORIDE  # scripted group (container) (typed FeaturePython)
  Dunit = g/cm3
  Dvalue = 4.89
  Group = -> [Ba_element001,F_element003]
  conduct = 2
  density = 1
  expand = 3
  formula = G4_BARIUM_FLUORIDE
  name = G4_BARIUM_FLUORIDE
  specific = 4
FEATURE [App::DocumentObjectGroupPython] Ba_element002  label="Ba_element : 002"  # scripted group (container) (typed FeaturePython)
  n = 1
  ref = Ba_element
FEATURE [App::DocumentObjectGroupPython] S_element002  label="S_element : 1"  # scripted group (container) (typed FeaturePython)
  n = 1
  ref = S_element
FEATURE [App::DocumentObjectGroupPython] O_element010  label="O_element : 4"  # scripted group (container) (typed FeaturePython)
  n = 4
  ref = O_element
FEATURE [App::DocumentObjectGroupPython] G4_BARIUM_SULFATE  # scripted group (container) (typed FeaturePython)
  Dunit = g/cm3
  Dvalue = 4.5
  Group = -> [Ba_element002,S_element002,O_element010]
  conduct = 2
  density = 1
  expand = 3
  formula = G4_BARIUM_SULFATE
  name = G4_BARIUM_SULFATE
  specific = 4
FEATURE [App::DocumentObjectGroupPython] C_element013  label="C_element : 007"  # scripted group (container) (typed FeaturePython)
  n = 6
  ref = C_element
FEATURE [App::DocumentObjectGroupPython] H_element013  label="H_element : 009"  # scripted group (container) (typed FeaturePython)
  n = 6
  ref = H_element
FEATURE [App::DocumentObjectGroupPython] G4_BENZENE  # scripted group (container) (typed FeaturePython)
  Dunit = g/cm3
  Dvalue = 0.87865
  Group = -> [C_element013,H_element013]
  conduct = 2
  density = 1
  expand = 3
  formula = G4_BENZENE
  name = G4_BENZENE
  specific = 4
FEATURE [App::DocumentObjectGroupPython] Be_element001  label="Be_element : 1"  # scripted group (container) (typed FeaturePython)
  n = 1
  ref = Be_element
FEATURE [App::DocumentObjectGroupPython] O_element011  label="O_element : 005"  # scripted group (container) (typed FeaturePython)
  n = 1
  ref = O_element
FEATURE [App::DocumentObjectGroupPython] G4_BERYLLIUM_OXIDE  # scripted group (container) (typed FeaturePython)
  Dunit = g/cm3
  Dvalue = 3.01
  Group = -> [Be_element001,O_element011]
  conduct = 2
  density = 1
  expand = 3
  formula = G4_BERYLLIUM_OXIDE
  name = G4_BERYLLIUM_OXIDE
  specific = 4
FEATURE [App::DocumentObjectGroupPython] Bi_element001  label="Bi_element : 4"  # scripted group (container) (typed FeaturePython)
  n = 4
  ref = Bi_element
FEATURE [App::DocumentObjectGroupPython] Ge_element001  label="Ge_element : 3"  # scripted group (container) (typed FeaturePython)
  n = 3
  ref = Ge_element
FEATURE [App::DocumentObjectGroupPython] O_element012  label="O_element : 12"  # scripted group (container) (typed FeaturePython)
  n = 12
  ref = O_element
FEATURE [App::DocumentObjectGroupPython] G4_BGO  # scripted group (container) (typed FeaturePython)
  Dunit = g/cm3
  Dvalue = 7.13
  Group = -> [Bi_element001,Ge_element001,O_element012]
  conduct = 2
  density = 1
  expand = 3
  formula = G4_BGO
  name = G4_BGO
  specific = 4
FEATURE [App::DocumentObjectGroupPython] H_element014  label="H_element : 0.102"  # scripted group (container) (typed FeaturePython)
  n = 0.102
FEATURE [App::DocumentObjectGroupPython] C_element014  label="C_element : 0.110"  # scripted group (container) (typed FeaturePython)
  n = 0.11
FEATURE [App::DocumentObjectGroupPython] N_element009  label="N_element : 0.033"  # scripted group (container) (typed FeaturePython)
  n = 0.033
FEATURE [App::DocumentObjectGroupPython] O_element013  label="O_element : 0.745"  # scripted group (container) (typed FeaturePython)
  n = 0.745
FEATURE [App::DocumentObjectGroupPython] Na_element002  label="Na_element : 0.002"  # scripted group (container) (typed FeaturePython)
  n = 0.001
FEATURE [App::DocumentObjectGroupPython] P_element001  label="P_element : 0.001"  # scripted group (container) (typed FeaturePython)
  n = 0.001
FEATURE [App::DocumentObjectGroupPython] S_element003  label="S_element : 0.002"  # scripted group (container) (typed FeaturePython)
  n = 0.002
FEATURE [App::DocumentObjectGroupPython] Cl_element002  label="Cl_element : 0.003"  # scripted group (container) (typed FeaturePython)
  n = 0.003
FEATURE [App::DocumentObjectGroupPython] K_element001  label="K_element : 0.002"  # scripted group (container) (typed FeaturePython)
  n = 0.002
FEATURE [App::DocumentObjectGroupPython] Fe_element001  label="Fe_element : 0.001"  # scripted group (container) (typed FeaturePython)
  n = 0.001
FEATURE [App::DocumentObjectGroupPython] G4_BLOOD_ICRP  # scripted group (container) (typed FeaturePython)
  Dunit = g/cm3
  Dvalue = 1.06
  Group = -> [H_element014,C_element014,N_element009,O_element013,Na_element002,P_element001,S_element003,Cl_element002,K_element001,Fe_element001]
  conduct = 2
  density = 1
  expand = 3
  formula = G4_BLOOD_ICRP
  name = G4_BLOOD_ICRP
  specific = 4
FEATURE [App::DocumentObjectGroupPython] H_element015  label="H_element : 0.064"  # scripted group (container) (typed FeaturePython)
  n = 0.064
FEATURE [App::DocumentObjectGroupPython] C_element015  label="C_element : 0.278"  # scripted group (container) (typed FeaturePython)
  n = 0.278
FEATURE [App::DocumentObjectGroupPython] N_element010  label="N_element : 0.027"  # scripted group (container) (typed FeaturePython)
  n = 0.027
FEATURE [App::DocumentObjectGroupPython] O_element014  label="O_element : 0.410"  # scripted group (container) (typed FeaturePython)
  n = 0.41
FEATURE [App::DocumentObjectGroupPython] Mg_element001  label="Mg_element : 0.002"  # scripted group (container) (typed FeaturePython)
  n = 0.002
FEATURE [App::DocumentObjectGroupPython] P_element002  label="P_element : 0.070"  # scripted group (container) (typed FeaturePython)
  n = 0.07
FEATURE [App::DocumentObjectGroupPython] S_element004  label="S_element : 0.003"  # scripted group (container) (typed FeaturePython)
  n = 0.002
FEATURE [App::DocumentObjectGroupPython] Ca_element003  label="Ca_element : 0.147"  # scripted group (container) (typed FeaturePython)
  n = 0.147
FEATURE [App::DocumentObjectGroupPython] G4_BONE_COMPACT_ICRU  # scripted group (container) (typed FeaturePython)
  Dunit = g/cm3
  Dvalue = 1.85
  Group = -> [H_element015,C_element015,N_element010,O_element014,Mg_element001,P_element002,S_element004,Ca_element003]
  conduct = 2
  density = 1
  expand = 3
  formula = G4_BONE_COMPACT_ICRU
  name = G4_BONE_COMPACT_ICRU
  specific = 4
FEATURE [App::DocumentObjectGroupPython] H_element016  label="H_element : 0.034"  # scripted group (container) (typed FeaturePython)
  n = 0.034
FEATURE [App::DocumentObjectGroupPython] C_element016  label="C_element : 0.155"  # scripted group (container) (typed FeaturePython)
  n = 0.155
FEATURE [App::DocumentObjectGroupPython] N_element011  label="N_element : 0.042"  # scripted group (container) (typed FeaturePython)
  n = 0.042
FEATURE [App::DocumentObjectGroupPython] O_element015  label="O_element : 0.435"  # scripted group (container) (typed FeaturePython)
  n = 0.435
FEATURE [App::DocumentObjectGroupPython] Na_element003  label="Na_element : 0.003"  # scripted group (container) (typed FeaturePython)
  n = 0.001
FEATURE [App::DocumentObjectGroupPython] Mg_element002  label="Mg_element : 0.003"  # scripted group (container) (typed FeaturePython)
  n = 0.002
FEATURE [App::DocumentObjectGroupPython] P_element003  label="P_element : 0.103"  # scripted group (container) (typed FeaturePython)
  n = 0.103
FEATURE [App::DocumentObjectGroupPython] S_element005  label="S_element : 0.004"  # scripted group (container) (typed FeaturePython)
  n = 0.003
FEATURE [App::DocumentObjectGroupPython] Ca_element004  label="Ca_element : 0.225"  # scripted group (container) (typed FeaturePython)
  n = 0.225
FEATURE [App::DocumentObjectGroupPython] G4_BONE_CORTICAL_ICRP  # scripted group (container) (typed FeaturePython)
  Dunit = g/cm3
  Dvalue = 1.92
  Group = -> [H_element016,C_element016,N_element011,O_element015,Na_element003,Mg_element002,P_element003,S_element005,Ca_element004]
  conduct = 2
  density = 1
  expand = 3
  formula = G4_BONE_CORTICAL_ICRP
  name = G4_BONE_CORTICAL_ICRP
  specific = 4
FEATURE [App::DocumentObjectGroupPython] B_element001  label="B_element : 4"  # scripted group (container) (typed FeaturePython)
  n = 4
  ref = B_element
FEATURE [App::DocumentObjectGroupPython] C_element017  label="C_element : 1"  # scripted group (container) (typed FeaturePython)
  n = 1
  ref = C_element
FEATURE [App::DocumentObjectGroupPython] G4_BORON_CARBIDE  # scripted group (container) (typed FeaturePython)
  Dunit = g/cm3
  Dvalue = 2.52
  Group = -> [B_element001,C_element017]
  conduct = 2
  density = 1
  expand = 3
  formula = G4_BORON_CARBIDE
  name = G4_BORON_CARBIDE
  specific = 4
FEATURE [App::DocumentObjectGroupPython] B_element002  label="B_element : 2"  # scripted group (container) (typed FeaturePython)
  n = 2
  ref = B_element
FEATURE [App::DocumentObjectGroupPython] O_element016  label="O_element : 006"  # scripted group (container) (typed FeaturePython)
  n = 3
  ref = O_element
FEATURE [App::DocumentObjectGroupPython] G4_BORON_OXIDE  # scripted group (container) (typed FeaturePython)
  Dunit = g/cm3
  Dvalue = 1.812
  Group = -> [B_element002,O_element016]
  conduct = 2
  density = 1
  expand = 3
  formula = G4_BORON_OXIDE
  name = G4_BORON_OXIDE
  specific = 4
FEATURE [App::DocumentObjectGroupPython] H_element017  label="H_element : 0.107"  # scripted group (container) (typed FeaturePython)
  n = 0.107
FEATURE [App::DocumentObjectGroupPython] C_element018  label="C_element : 0.145"  # scripted group (container) (typed FeaturePython)
  n = 0.145
FEATURE [App::DocumentObjectGroupPython] N_element012  label="N_element : 0.022"  # scripted group (container) (typed FeaturePython)
  n = 0.022
FEATURE [App::DocumentObjectGroupPython] O_element017  label="O_element : 0.712"  # scripted group (container) (typed FeaturePython)
  n = 0.712
FEATURE [App::DocumentObjectGroupPython] Na_element004  label="Na_element : 0.004"  # scripted group (container) (typed FeaturePython)
  n = 0.002
FEATURE [App::DocumentObjectGroupPython] P_element004  label="P_element : 0.004"  # scripted group (container) (typed FeaturePython)
  n = 0.004
FEATURE [App::DocumentObjectGroupPython] S_element006  label="S_element : 0.005"  # scripted group (container) (typed FeaturePython)
  n = 0.002
FEATURE [App::DocumentObjectGroupPython] Cl_element003  label="Cl_element : 0.004"  # scripted group (container) (typed FeaturePython)
  n = 0.003
FEATURE [App::DocumentObjectGroupPython] K_element002  label="K_element : 0.003"  # scripted group (container) (typed FeaturePython)
  n = 0.003
FEATURE [App::DocumentObjectGroupPython] G4_BRAIN_ICRP  # scripted group (container) (typed FeaturePython)
  Dunit = g/cm3
  Dvalue = 1.04
  Group = -> [H_element017,C_element018,N_element012,O_element017,Na_element004,P_element004,S_element006,Cl_element003,K_element002]
  conduct = 2
  density = 1
  expand = 3
  formula = G4_BRAIN_ICRP
  name = G4_BRAIN_ICRP
  specific = 4
FEATURE [App::DocumentObjectGroupPython] C_element019  label="C_element : 4"  # scripted group (container) (typed FeaturePython)
  n = 4
  ref = C_element
FEATURE [App::DocumentObjectGroupPython] H_element018  label="H_element : 010"  # scripted group (container) (typed FeaturePython)
  n = 10
  ref = H_element
FEATURE [App::DocumentObjectGroupPython] G4_BUTANE  # scripted group (container) (typed FeaturePython)
  Dunit = g/cm3
  Dvalue = 0.00249343
  Group = -> [C_element019,H_element018]
  conduct = 2
  density = 1
  expand = 3
  formula = G4_BUTANE
  name = G4_BUTANE
  specific = 4
FEATURE [App::DocumentObjectGroupPython] C_element020  label="C_element : 008"  # scripted group (container) (typed FeaturePython)
  n = 4
  ref = C_element
FEATURE [App::DocumentObjectGroupPython] H_element019  label="H_element : 011"  # scripted group (container) (typed FeaturePython)
  n = 10
  ref = H_element
FEATURE [App::DocumentObjectGroupPython] O_element018  label="O_element : 007"  # scripted group (container) (typed FeaturePython)
  n = 1
  ref = O_element
FEATURE [App::DocumentObjectGroupPython] G4_N_BUTYL_ALCOHOL  label="G4_N-BUTYL_ALCOHOL"  # scripted group (container) (typed FeaturePython)
  Dunit = g/cm3
  Dvalue = 0.8098
  Group = -> [C_element020,H_element019,O_element018]
  conduct = 2
  density = 1
  expand = 3
  formula = G4_N-BUTYL_ALCOHOL
  name = G4_N-BUTYL_ALCOHOL
  specific = 4
FEATURE [App::DocumentObjectGroupPython] H_element020  label="H_element : 0.025"  # scripted group (container) (typed FeaturePython)
  n = 0.02468
FEATURE [App::DocumentObjectGroupPython] C_element021  label="C_element : 0.502"  # scripted group (container) (typed FeaturePython)
  n = 0.501611
FEATURE [App::DocumentObjectGroupPython] O_element019  label="O_element : 0.005"  # scripted group (container) (typed FeaturePython)
  n = 0.004527
FEATURE [App::DocumentObjectGroupPython] F_element004  label="F_element : 0.465"  # scripted group (container) (typed FeaturePython)
  n = 0.465209
FEATURE [App::DocumentObjectGroupPython] Si_element001  label="Si_element : 0.004"  # scripted group (container) (typed FeaturePython)
  n = 0.003973
FEATURE [App::DocumentObjectGroupPython] G4_C_552  label="G4_C-552"  # scripted group (container) (typed FeaturePython)
  Dunit = g/cm3
  Dvalue = 1.76
  Group = -> [H_element020,C_element021,O_element019,F_element004,Si_element001]
  conduct = 2
  density = 1
  expand = 3
  formula = G4_C-552
  name = G4_C-552
  specific = 4
FEATURE [App::DocumentObjectGroupPython] Cd_element001  label="Cd_element : 1"  # scripted group (container) (typed FeaturePython)
  n = 1
  ref = Cd_element
FEATURE [App::DocumentObjectGroupPython] Te_element001  label="Te_element : 1"  # scripted group (container) (typed FeaturePython)
  n = 1
  ref = Te_element
FEATURE [App::DocumentObjectGroupPython] G4_CADMIUM_TELLURIDE  # scripted group (container) (typed FeaturePython)
  Dunit = g/cm3
  Dvalue = 6.2
  Group = -> [Cd_element001,Te_element001]
  conduct = 2
  density = 1
  expand = 3
  formula = G4_CADMIUM_TELLURIDE
  name = G4_CADMIUM_TELLURIDE
  specific = 4
FEATURE [App::DocumentObjectGroupPython] Cd_element002  label="Cd_element : 002"  # scripted group (container) (typed FeaturePython)
  n = 1
  ref = Cd_element
FEATURE [App::DocumentObjectGroupPython] W_element001  label="W_element : 1"  # scripted group (container) (typed FeaturePython)
  n = 1
  ref = W_element
FEATURE [App::DocumentObjectGroupPython] O_element020  label="O_element : 008"  # scripted group (container) (typed FeaturePython)
  n = 4
  ref = O_element
FEATURE [App::DocumentObjectGroupPython] G4_CADMIUM_TUNGSTATE  # scripted group (container) (typed FeaturePython)
  Dunit = g/cm3
  Dvalue = 7.9
  Group = -> [Cd_element002,W_element001,O_element020]
  conduct = 2
  density = 1
  expand = 3
  formula = G4_CADMIUM_TUNGSTATE
  name = G4_CADMIUM_TUNGSTATE
  specific = 4
FEATURE [App::DocumentObjectGroupPython] Ca_element005  label="Ca_element : 1"  # scripted group (container) (typed FeaturePython)
  n = 1
  ref = Ca_element
FEATURE [App::DocumentObjectGroupPython] C_element022  label="C_element : 009"  # scripted group (container) (typed FeaturePython)
  n = 1
  ref = C_element
FEATURE [App::DocumentObjectGroupPython] O_element021  label="O_element : 009"  # scripted group (container) (typed FeaturePython)
  n = 3
  ref = O_element
FEATURE [App::DocumentObjectGroupPython] G4_CALCIUM_CARBONATE  # scripted group (container) (typed FeaturePython)
  Dunit = g/cm3
  Dvalue = 2.8
  Group = -> [Ca_element005,C_element022,O_element021]
  conduct = 2
  density = 1
  expand = 3
  formula = G4_CALCIUM_CARBONATE
  name = G4_CALCIUM_CARBONATE
  specific = 4
FEATURE [App::DocumentObjectGroupPython] Ca_element006  label="Ca_element : 002"  # scripted group (container) (typed FeaturePython)
  n = 1
  ref = Ca_element
FEATURE [App::DocumentObjectGroupPython] F_element005  label="F_element : 003"  # scripted group (container) (typed FeaturePython)
  n = 2
  ref = F_element
FEATURE [App::DocumentObjectGroupPython] G4_CALCIUM_FLUORIDE  # scripted group (container) (typed FeaturePython)
  Dunit = g/cm3
  Dvalue = 3.18
  Group = -> [Ca_element006,F_element005]
  conduct = 2
  density = 1
  expand = 3
  formula = G4_CALCIUM_FLUORIDE
  name = G4_CALCIUM_FLUORIDE
  specific = 4
FEATURE [App::DocumentObjectGroupPython] Ca_element007  label="Ca_element : 003"  # scripted group (container) (typed FeaturePython)
  n = 1
  ref = Ca_element
FEATURE [App::DocumentObjectGroupPython] O_element022  label="O_element : 010"  # scripted group (container) (typed FeaturePython)
  n = 1
  ref = O_element
FEATURE [App::DocumentObjectGroupPython] G4_CALCIUM_OXIDE  # scripted group (container) (typed FeaturePython)
  Dunit = g/cm3
  Dvalue = 3.3
  Group = -> [Ca_element007,O_element022]
  conduct = 2
  density = 1
  expand = 3
  formula = G4_CALCIUM_OXIDE
  name = G4_CALCIUM_OXIDE
  specific = 4
FEATURE [App::DocumentObjectGroupPython] Ca_element008  label="Ca_element : 004"  # scripted group (container) (typed FeaturePython)
  n = 1
  ref = Ca_element
FEATURE [App::DocumentObjectGroupPython] S_element007  label="S_element : 002"  # scripted group (container) (typed FeaturePython)
  n = 1
  ref = S_element
FEATURE [App::DocumentObjectGroupPython] O_element023  label="O_element : 011"  # scripted group (container) (typed FeaturePython)
  n = 4
  ref = O_element
FEATURE [App::DocumentObjectGroupPython] G4_CALCIUM_SULFATE  # scripted group (container) (typed FeaturePython)
  Dunit = g/cm3
  Dvalue = 2.96
  Group = -> [Ca_element008,S_element007,O_element023]
  conduct = 2
  density = 1
  expand = 3
  formula = G4_CALCIUM_SULFATE
  name = G4_CALCIUM_SULFATE
  specific = 4
FEATURE [App::DocumentObjectGroupPython] Ca_element009  label="Ca_element : 005"  # scripted group (container) (typed FeaturePython)
  n = 1
  ref = Ca_element
FEATURE [App::DocumentObjectGroupPython] W_element002  label="W_element : 002"  # scripted group (container) (typed FeaturePython)
  n = 1
  ref = W_element
FEATURE [App::DocumentObjectGroupPython] O_element024  label="O_element : 012"  # scripted group (container) (typed FeaturePython)
  n = 4
  ref = O_element
FEATURE [App::DocumentObjectGroupPython] G4_CALCIUM_TUNGSTATE  # scripted group (container) (typed FeaturePython)
  Dunit = g/cm3
  Dvalue = 6.062
  Group = -> [Ca_element009,W_element002,O_element024]
  conduct = 2
  density = 1
  expand = 3
  formula = G4_CALCIUM_TUNGSTATE
  name = G4_CALCIUM_TUNGSTATE
  specific = 4
FEATURE [App::DocumentObjectGroupPython] C_element023  label="C_element : 010"  # scripted group (container) (typed FeaturePython)
  n = 1
  ref = C_element
FEATURE [App::DocumentObjectGroupPython] O_element025  label="O_element : 013"  # scripted group (container) (typed FeaturePython)
  n = 2
  ref = O_element
FEATURE [App::DocumentObjectGroupPython] G4_CARBON_DIOXIDE  # scripted group (container) (typed FeaturePython)
  Dunit = g/cm3
  Dvalue = 0.00184212
  Group = -> [C_element023,O_element025]
  conduct = 2
  density = 1
  expand = 3
  formula = G4_CARBON_DIOXIDE
  name = G4_CARBON_DIOXIDE
  specific = 4
FEATURE [App::DocumentObjectGroupPython] C_element024  label="C_element : 011"  # scripted group (container) (typed FeaturePython)
  n = 1
  ref = C_element
FEATURE [App::DocumentObjectGroupPython] Cl_element004  label="Cl_element : 4"  # scripted group (container) (typed FeaturePython)
  n = 4
  ref = Cl_element
FEATURE [App::DocumentObjectGroupPython] G4_CARBON_TETRACHLORIDE  # scripted group (container) (typed FeaturePython)
  Dunit = g/cm3
  Dvalue = 1.594
  Group = -> [C_element024,Cl_element004]
  conduct = 2
  density = 1
  expand = 3
  formula = G4_CARBON_TETRACHLORIDE
  name = G4_CARBON_TETRACHLORIDE
  specific = 4
FEATURE [App::DocumentObjectGroupPython] C_element025  label="C_element : 012"  # scripted group (container) (typed FeaturePython)
  n = 6
  ref = C_element
FEATURE [App::DocumentObjectGroupPython] H_element021  label="H_element : 012"  # scripted group (container) (typed FeaturePython)
  n = 10
  ref = H_element
FEATURE [App::DocumentObjectGroupPython] O_element026  label="O_element : 5"  # scripted group (container) (typed FeaturePython)
  n = 5
  ref = O_element
FEATURE [App::DocumentObjectGroupPython] G4_CELLULOSE_CELLOPHANE  # scripted group (container) (typed FeaturePython)
  Dunit = g/cm3
  Dvalue = 1.42
  Group = -> [C_element025,H_element021,O_element026]
  conduct = 2
  density = 1
  expand = 3
  formula = G4_CELLULOSE_CELLOPHANE
  name = G4_CELLULOSE_CELLOPHANE
  specific = 4
FEATURE [App::DocumentObjectGroupPython] H_element022  label="H_element : 0.067"  # scripted group (container) (typed FeaturePython)
  n = 0.067125
FEATURE [App::DocumentObjectGroupPython] C_element026  label="C_element : 0.545"  # scripted group (container) (typed FeaturePython)
  n = 0.545403
FEATURE [App::DocumentObjectGroupPython] O_element027  label="O_element : 0.387"  # scripted group (container) (typed FeaturePython)
  n = 0.387472
FEATURE [App::DocumentObjectGroupPython] G4_CELLULOSE_BUTYRATE  # scripted group (container) (typed FeaturePython)
  Dunit = g/cm3
  Dvalue = 1.2
  Group = -> [H_element022,C_element026,O_element027]
  conduct = 2
  density = 1
  expand = 3
  formula = G4_CELLULOSE_BUTYRATE
  name = G4_CELLULOSE_BUTYRATE
  specific = 4
FEATURE [App::DocumentObjectGroupPython] H_element023  label="H_element : 0.029"  # scripted group (container) (typed FeaturePython)
  n = 0.029216
FEATURE [App::DocumentObjectGroupPython] C_element027  label="C_element : 0.271"  # scripted group (container) (typed FeaturePython)
  n = 0.271296
FEATURE [App::DocumentObjectGroupPython] N_element013  label="N_element : 0.121"  # scripted group (container) (typed FeaturePython)
  n = 0.121276
FEATURE [App::DocumentObjectGroupPython] O_element028  label="O_element : 0.578"  # scripted group (container) (typed FeaturePython)
  n = 0.578212
FEATURE [App::DocumentObjectGroupPython] G4_CELLULOSE_NITRATE  # scripted group (container) (typed FeaturePython)
  Dunit = g/cm3
  Dvalue = 1.49
  Group = -> [H_element023,C_element027,N_element013,O_element028]
  conduct = 2
  density = 1
  expand = 3
  formula = G4_CELLULOSE_NITRATE
  name = G4_CELLULOSE_NITRATE
  specific = 4
FEATURE [App::DocumentObjectGroupPython] H_element024  label="H_element : 0.108"  # scripted group (container) (typed FeaturePython)
  n = 0.107596
FEATURE [App::DocumentObjectGroupPython] N_element014  label="N_element : 0.001"  # scripted group (container) (typed FeaturePython)
  n = 0.0008
FEATURE [App::DocumentObjectGroupPython] O_element029  label="O_element : 0.875"  # scripted group (container) (typed FeaturePython)
  n = 0.874976
FEATURE [App::DocumentObjectGroupPython] S_element008  label="S_element : 0.015"  # scripted group (container) (typed FeaturePython)
  n = 0.014627
FEATURE [App::DocumentObjectGroupPython] Ce_element001  label="Ce_element : 0.002"  # scripted group (container) (typed FeaturePython)
  n = 0.002001
FEATURE [App::DocumentObjectGroupPython] G4_CERIC_SULFATE  # scripted group (container) (typed FeaturePython)
  Dunit = g/cm3
  Dvalue = 1.03
  Group = -> [H_element024,N_element014,O_element029,S_element008,Ce_element001]
  conduct = 2
  density = 1
  expand = 3
  formula = G4_CERIC_SULFATE
  name = G4_CERIC_SULFATE
  specific = 4
FEATURE [App::DocumentObjectGroupPython] Cs_element001  label="Cs_element : 1"  # scripted group (container) (typed FeaturePython)
  n = 1
  ref = Cs_element
FEATURE [App::DocumentObjectGroupPython] F_element006  label="F_element : 1"  # scripted group (container) (typed FeaturePython)
  n = 1
  ref = F_element
FEATURE [App::DocumentObjectGroupPython] G4_CESIUM_FLUORIDE  # scripted group (container) (typed FeaturePython)
  Dunit = g/cm3
  Dvalue = 4.115
  Group = -> [Cs_element001,F_element006]
  conduct = 2
  density = 1
  expand = 3
  formula = G4_CESIUM_FLUORIDE
  name = G4_CESIUM_FLUORIDE
  specific = 4
FEATURE [App::DocumentObjectGroupPython] Cs_element002  label="Cs_element : 002"  # scripted group (container) (typed FeaturePython)
  n = 1
  ref = Cs_element
FEATURE [App::DocumentObjectGroupPython] I_element001  label="I_element : 1"  # scripted group (container) (typed FeaturePython)
  n = 1
  ref = I_element
FEATURE [App::DocumentObjectGroupPython] G4_CESIUM_IODIDE  # scripted group (container) (typed FeaturePython)
  Dunit = g/cm3
  Dvalue = 4.51
  Group = -> [Cs_element002,I_element001]
  conduct = 2
  density = 1
  expand = 3
  formula = G4_CESIUM_IODIDE
  name = G4_CESIUM_IODIDE
  specific = 4
FEATURE [App::DocumentObjectGroupPython] C_element028  label="C_element : 013"  # scripted group (container) (typed FeaturePython)
  n = 6
  ref = C_element
FEATURE [App::DocumentObjectGroupPython] H_element025  label="H_element : 013"  # scripted group (container) (typed FeaturePython)
  n = 5
  ref = H_element
FEATURE [App::DocumentObjectGroupPython] Cl_element005  label="Cl_element : 1"  # scripted group (container) (typed FeaturePython)
  n = 1
  ref = Cl_element
FEATURE [App::DocumentObjectGroupPython] G4_CHLOROBENZENE  # scripted group (container) (typed FeaturePython)
  Dunit = g/cm3
  Dvalue = 1.1058
  Group = -> [C_element028,H_element025,Cl_element005]
  conduct = 2
  density = 1
  expand = 3
  formula = G4_CHLOROBENZENE
  name = G4_CHLOROBENZENE
  specific = 4
FEATURE [App::DocumentObjectGroupPython] C_element029  label="C_element : 014"  # scripted group (container) (typed FeaturePython)
  n = 1
  ref = C_element
FEATURE [App::DocumentObjectGroupPython] H_element026  label="H_element : 1"  # scripted group (container) (typed FeaturePython)
  n = 1
  ref = H_element
FEATURE [App::DocumentObjectGroupPython] Cl_element006  label="Cl_element : 3"  # scripted group (container) (typed FeaturePython)
  n = 3
  ref = Cl_element
FEATURE [App::DocumentObjectGroupPython] G4_CHLOROFORM  # scripted group (container) (typed FeaturePython)
  Dunit = g/cm3
  Dvalue = 1.4832
  Group = -> [C_element029,H_element026,Cl_element006]
  conduct = 2
  density = 1
  expand = 3
  formula = G4_CHLOROFORM
  name = G4_CHLOROFORM
  specific = 4
FEATURE [App::DocumentObjectGroupPython] H_element027  label="H_element : 0.010"  # scripted group (container) (typed FeaturePython)
  n = 0.01
FEATURE [App::DocumentObjectGroupPython] C_element030  label="C_element : 0.001"  # scripted group (container) (typed FeaturePython)
  n = 0.001
FEATURE [App::DocumentObjectGroupPython] O_element030  label="O_element : 0.529"  # scripted group (container) (typed FeaturePython)
  n = 0.529107
FEATURE [App::DocumentObjectGroupPython] Na_element005  label="Na_element : 0.016"  # scripted group (container) (typed FeaturePython)
  n = 0.016
FEATURE [App::DocumentObjectGroupPython] Mg_element003  label="Mg_element : 0.004"  # scripted group (container) (typed FeaturePython)
  n = 0.002
FEATURE [App::DocumentObjectGroupPython] Al_element002  label="Al_element : 0.034"  # scripted group (container) (typed FeaturePython)
  n = 0.033872
FEATURE [App::DocumentObjectGroupPython] Si_element002  label="Si_element : 0.337"  # scripted group (container) (typed FeaturePython)
  n = 0.337021
FEATURE [App::DocumentObjectGroupPython] K_element003  label="K_element : 0.013"  # scripted group (container) (typed FeaturePython)
  n = 0.013
FEATURE [App::DocumentObjectGroupPython] Ca_element010  label="Ca_element : 0.044"  # scripted group (container) (typed FeaturePython)
  n = 0.044
FEATURE [App::DocumentObjectGroupPython] Fe_element002  label="Fe_element : 0.014"  # scripted group (container) (typed FeaturePython)
  n = 0.014
FEATURE [App::DocumentObjectGroupPython] G4_CONCRETE  # scripted group (container) (typed FeaturePython)
  Dunit = g/cm3
  Dvalue = 2.3
  Group = -> [H_element027,C_element030,O_element030,Na_element005,Mg_element003,Al_element002,Si_element002,K_element003,Ca_element010,Fe_element002]
  conduct = 2
  density = 1
  expand = 3
  formula = G4_CONCRETE
  name = G4_CONCRETE
  specific = 4
FEATURE [App::DocumentObjectGroupPython] C_element031  label="C_element : 015"  # scripted group (container) (typed FeaturePython)
  n = 6
  ref = C_element
FEATURE [App::DocumentObjectGroupPython] H_element028  label="H_element : 12"  # scripted group (container) (typed FeaturePython)
  n = 12
  ref = H_element
FEATURE [App::DocumentObjectGroupPython] G4_CYCLOHEXANE  # scripted group (container) (typed FeaturePython)
  Dunit = g/cm3
  Dvalue = 0.779
  Group = -> [C_element031,H_element028]
  conduct = 2
  density = 1
  expand = 3
  formula = G4_CYCLOHEXANE
  name = G4_CYCLOHEXANE
  specific = 4
FEATURE [App::DocumentObjectGroupPython] C_element032  label="C_element : 016"  # scripted group (container) (typed FeaturePython)
  n = 6
  ref = C_element
FEATURE [App::DocumentObjectGroupPython] H_element029  label="H_element : 4"  # scripted group (container) (typed FeaturePython)
  n = 4
  ref = H_element
FEATURE [App::DocumentObjectGroupPython] Cl_element007  label="Cl_element : 2"  # scripted group (container) (typed FeaturePython)
  n = 2
  ref = Cl_element
FEATURE [App::DocumentObjectGroupPython] G4_1_2_DICHLOROBENZENE  label="G4_1.2-DICHLOROBENZENE"  # scripted group (container) (typed FeaturePython)
  Dunit = g/cm3
  Dvalue = 1.3048
  Group = -> [C_element032,H_element029,Cl_element007]
  conduct = 2
  density = 1
  expand = 3
  formula = G4_1.2-DICHLOROBENZENE
  name = G4_1.2-DICHLOROBENZENE
  specific = 4
FEATURE [App::DocumentObjectGroupPython] C_element033  label="C_element : 017"  # scripted group (container) (typed FeaturePython)
  n = 4
  ref = C_element
FEATURE [App::DocumentObjectGroupPython] H_element030  label="H_element : 8"  # scripted group (container) (typed FeaturePython)
  n = 8
  ref = H_element
FEATURE [App::DocumentObjectGroupPython] O_element031  label="O_element : 014"  # scripted group (container) (typed FeaturePython)
  n = 1
  ref = O_element
FEATURE [App::DocumentObjectGroupPython] Cl_element008  label="Cl_element : 005"  # scripted group (container) (typed FeaturePython)
  n = 2
  ref = Cl_element
FEATURE [App::DocumentObjectGroupPython] G4_DICHLORODIETHYL_ETHER  # scripted group (container) (typed FeaturePython)
  Dunit = g/cm3
  Dvalue = 1.2199
  Group = -> [C_element033,H_element030,O_element031,Cl_element008]
  conduct = 2
  density = 1
  expand = 3
  formula = G4_DICHLORODIETHYL_ETHER
  name = G4_DICHLORODIETHYL_ETHER
  specific = 4
FEATURE [App::DocumentObjectGroupPython] C_element034  label="C_element : 018"  # scripted group (container) (typed FeaturePython)
  n = 2
  ref = C_element
FEATURE [App::DocumentObjectGroupPython] H_element031  label="H_element : 014"  # scripted group (container) (typed FeaturePython)
  n = 4
  ref = H_element
FEATURE [App::DocumentObjectGroupPython] Cl_element009  label="Cl_element : 006"  # scripted group (container) (typed FeaturePython)
  n = 2
  ref = Cl_element
FEATURE [App::DocumentObjectGroupPython] G4_1_2_DICHLOROETHANE  label="G4_1.2-DICHLOROETHANE"  # scripted group (container) (typed FeaturePython)
  Dunit = g/cm3
  Dvalue = 1.2351
  Group = -> [C_element034,H_element031,Cl_element009]
  conduct = 2
  density = 1
  expand = 3
  formula = G4_1.2-DICHLOROETHANE
  name = G4_1.2-DICHLOROETHANE
  specific = 4
FEATURE [App::DocumentObjectGroupPython] C_element035  label="C_element : 019"  # scripted group (container) (typed FeaturePython)
  n = 4
  ref = C_element
FEATURE [App::DocumentObjectGroupPython] H_element032  label="H_element : 015"  # scripted group (container) (typed FeaturePython)
  n = 10
  ref = H_element
FEATURE [App::DocumentObjectGroupPython] O_element032  label="O_element : 015"  # scripted group (container) (typed FeaturePython)
  n = 1
  ref = O_element
FEATURE [App::DocumentObjectGroupPython] G4_DIETHYL_ETHER  # scripted group (container) (typed FeaturePython)
  Dunit = g/cm3
  Dvalue = 0.71378
  Group = -> [C_element035,H_element032,O_element032]
  conduct = 2
  density = 1
  expand = 3
  formula = G4_DIETHYL_ETHER
  name = G4_DIETHYL_ETHER
  specific = 4
FEATURE [App::DocumentObjectGroupPython] C_element036  label="C_element : 020"  # scripted group (container) (typed FeaturePython)
  n = 3
  ref = C_element
FEATURE [App::DocumentObjectGroupPython] H_element033  label="H_element : 016"  # scripted group (container) (typed FeaturePython)
  n = 7
  ref = H_element
FEATURE [App::DocumentObjectGroupPython] N_element015  label="N_element : 008"  # scripted group (container) (typed FeaturePython)
  n = 1
  ref = N_element
FEATURE [App::DocumentObjectGroupPython] O_element033  label="O_element : 016"  # scripted group (container) (typed FeaturePython)
  n = 1
  ref = O_element
FEATURE [App::DocumentObjectGroupPython] G4_N_N_DIMETHYL_FORMAMIDE  label="G4_N.N-DIMETHYL_FORMAMIDE"  # scripted group (container) (typed FeaturePython)
  Dunit = g/cm3
  Dvalue = 0.9487
  Group = -> [C_element036,H_element033,N_element015,O_element033]
  conduct = 2
  density = 1
  expand = 3
  formula = G4_N.N-DIMETHYL_FORMAMIDE
  name = G4_N.N-DIMETHYL_FORMAMIDE
  specific = 4
FEATURE [App::DocumentObjectGroupPython] C_element037  label="C_element : 021"  # scripted group (container) (typed FeaturePython)
  n = 2
  ref = C_element
FEATURE [App::DocumentObjectGroupPython] H_element034  label="H_element : 017"  # scripted group (container) (typed FeaturePython)
  n = 6
  ref = H_element
FEATURE [App::DocumentObjectGroupPython] O_element034  label="O_element : 017"  # scripted group (container) (typed FeaturePython)
  n = 1
  ref = O_element
FEATURE [App::DocumentObjectGroupPython] S_element009  label="S_element : 003"  # scripted group (container) (typed FeaturePython)
  n = 1
  ref = S_element
FEATURE [App::DocumentObjectGroupPython] G4_DIMETHYL_SULFOXIDE  # scripted group (container) (typed FeaturePython)
  Dunit = g/cm3
  Dvalue = 1.1014
  Group = -> [C_element037,H_element034,O_element034,S_element009]
  conduct = 2
  density = 1
  expand = 3
  formula = G4_DIMETHYL_SULFOXIDE
  name = G4_DIMETHYL_SULFOXIDE
  specific = 4
FEATURE [App::DocumentObjectGroupPython] C_element038  label="C_element : 022"  # scripted group (container) (typed FeaturePython)
  n = 2
  ref = C_element
FEATURE [App::DocumentObjectGroupPython] H_element035  label="H_element : 018"  # scripted group (container) (typed FeaturePython)
  n = 6
  ref = H_element
FEATURE [App::DocumentObjectGroupPython] G4_ETHANE  # scripted group (container) (typed FeaturePython)
  Dunit = g/cm3
  Dvalue = 0.00125324
  Group = -> [C_element038,H_element035]
  conduct = 2
  density = 1
  expand = 3
  formula = G4_ETHANE
  name = G4_ETHANE
  specific = 4
FEATURE [App::DocumentObjectGroupPython] C_element039  label="C_element : 023"  # scripted group (container) (typed FeaturePython)
  n = 2
  ref = C_element
FEATURE [App::DocumentObjectGroupPython] H_element036  label="H_element : 019"  # scripted group (container) (typed FeaturePython)
  n = 6
  ref = H_element
FEATURE [App::DocumentObjectGroupPython] O_element035  label="O_element : 018"  # scripted group (container) (typed FeaturePython)
  n = 1
  ref = O_element
FEATURE [App::DocumentObjectGroupPython] G4_ETHYL_ALCOHOL  # scripted group (container) (typed FeaturePython)
  Dunit = g/cm3
  Dvalue = 0.7893
  Group = -> [C_element039,H_element036,O_element035]
  conduct = 2
  density = 1
  expand = 3
  formula = G4_ETHYL_ALCOHOL
  name = G4_ETHYL_ALCOHOL
  specific = 4
FEATURE [App::DocumentObjectGroupPython] H_element037  label="H_element : 0.090"  # scripted group (container) (typed FeaturePython)
  n = 0.090027
FEATURE [App::DocumentObjectGroupPython] C_element040  label="C_element : 0.585"  # scripted group (container) (typed FeaturePython)
  n = 0.585182
FEATURE [App::DocumentObjectGroupPython] O_element036  label="O_element : 0.325"  # scripted group (container) (typed FeaturePython)
  n = 0.324791
FEATURE [App::DocumentObjectGroupPython] G4_ETHYL_CELLULOSE  # scripted group (container) (typed FeaturePython)
  Dunit = g/cm3
  Dvalue = 1.13
  Group = -> [H_element037,C_element040,O_element036]
  conduct = 2
  density = 1
  expand = 3
  formula = G4_ETHYL_CELLULOSE
  name = G4_ETHYL_CELLULOSE
  specific = 4
FEATURE [App::DocumentObjectGroupPython] C_element041  label="C_element : 024"  # scripted group (container) (typed FeaturePython)
  n = 2
  ref = C_element
FEATURE [App::DocumentObjectGroupPython] H_element038  label="H_element : 020"  # scripted group (container) (typed FeaturePython)
  n = 4
  ref = H_element
FEATURE [App::DocumentObjectGroupPython] G4_ETHYLENE  # scripted group (container) (typed FeaturePython)
  Dunit = g/cm3
  Dvalue = 0.00117497
  Group = -> [C_element041,H_element038]
  conduct = 2
  density = 1
  expand = 3
  formula = G4_ETHYLENE
  name = G4_ETHYLENE
  specific = 4
FEATURE [App::DocumentObjectGroupPython] H_element039  label="H_element : 0.096"  # scripted group (container) (typed FeaturePython)
  n = 0.096
FEATURE [App::DocumentObjectGroupPython] C_element042  label="C_element : 0.195"  # scripted group (container) (typed FeaturePython)
  n = 0.195
FEATURE [App::DocumentObjectGroupPython] N_element016  label="N_element : 0.057"  # scripted group (container) (typed FeaturePython)
  n = 0.057
FEATURE [App::DocumentObjectGroupPython] O_element037  label="O_element : 0.646"  # scripted group (container) (typed FeaturePython)
  n = 0.646
FEATURE [App::DocumentObjectGroupPython] Na_element006  label="Na_element : 0.017"  # scripted group (container) (typed FeaturePython)
  n = 0.001
FEATURE [App::DocumentObjectGroupPython] P_element005  label="P_element : 0.104"  # scripted group (container) (typed FeaturePython)
  n = 0.001
FEATURE [App::DocumentObjectGroupPython] S_element010  label="S_element : 0.016"  # scripted group (container) (typed FeaturePython)
  n = 0.003
FEATURE [App::DocumentObjectGroupPython] Cl_element010  label="Cl_element : 0.005"  # scripted group (container) (typed FeaturePython)
  n = 0.001
FEATURE [App::DocumentObjectGroupPython] G4_EYE_LENS_ICRP  # scripted group (container) (typed FeaturePython)
  Dunit = g/cm3
  Dvalue = 1.07
  Group = -> [H_element039,C_element042,N_element016,O_element037,Na_element006,P_element005,S_element010,Cl_element010]
  conduct = 2
  density = 1
  expand = 3
  formula = G4_EYE_LENS_ICRP
  name = G4_EYE_LENS_ICRP
  specific = 4
FEATURE [App::DocumentObjectGroupPython] Fe_element003  label="Fe_element : 2"  # scripted group (container) (typed FeaturePython)
  n = 2
  ref = Fe_element
FEATURE [App::DocumentObjectGroupPython] O_element038  label="O_element : 019"  # scripted group (container) (typed FeaturePython)
  n = 3
  ref = O_element
FEATURE [App::DocumentObjectGroupPython] G4_FERRIC_OXIDE  # scripted group (container) (typed FeaturePython)
  Dunit = g/cm3
  Dvalue = 5.2
  Group = -> [Fe_element003,O_element038]
  conduct = 2
  density = 1
  expand = 3
  formula = G4_FERRIC_OXIDE
  name = G4_FERRIC_OXIDE
  specific = 4
FEATURE [App::DocumentObjectGroupPython] Fe_element004  label="Fe_element : 1"  # scripted group (container) (typed FeaturePython)
  n = 1
  ref = Fe_element
FEATURE [App::DocumentObjectGroupPython] B_element003  label="B_element : 1"  # scripted group (container) (typed FeaturePython)
  n = 1
  ref = B_element
FEATURE [App::DocumentObjectGroupPython] G4_FERROBORIDE  # scripted group (container) (typed FeaturePython)
  Dunit = g/cm3
  Dvalue = 7.15
  Group = -> [Fe_element004,B_element003]
  conduct = 2
  density = 1
  expand = 3
  formula = G4_FERROBORIDE
  name = G4_FERROBORIDE
  specific = 4
FEATURE [App::DocumentObjectGroupPython] Fe_element005  label="Fe_element : 003"  # scripted group (container) (typed FeaturePython)
  n = 1
  ref = Fe_element
FEATURE [App::DocumentObjectGroupPython] O_element039  label="O_element : 020"  # scripted group (container) (typed FeaturePython)
  n = 1
  ref = O_element
FEATURE [App::DocumentObjectGroupPython] G4_FERROUS_OXIDE  # scripted group (container) (typed FeaturePython)
  Dunit = g/cm3
  Dvalue = 5.7
  Group = -> [Fe_element005,O_element039]
  conduct = 2
  density = 1
  expand = 3
  formula = G4_FERROUS_OXIDE
  name = G4_FERROUS_OXIDE
  specific = 4
FEATURE [App::DocumentObjectGroupPython] H_element040  label="H_element : 0.115"  # scripted group (container) (typed FeaturePython)
  n = 0.108259
FEATURE [App::DocumentObjectGroupPython] N_element017  label="N_element : 0.000"  # scripted group (container) (typed FeaturePython)
  n = 2.7e-05
FEATURE [App::DocumentObjectGroupPython] O_element040  label="O_element : 0.879"  # scripted group (container) (typed FeaturePython)
  n = 0.878636
FEATURE [App::DocumentObjectGroupPython] Na_element007  label="Na_element : 0.000"  # scripted group (container) (typed FeaturePython)
  n = 2.2e-05
FEATURE [App::DocumentObjectGroupPython] S_element011  label="S_element : 0.013"  # scripted group (container) (typed FeaturePython)
  n = 0.012968
FEATURE [App::DocumentObjectGroupPython] Cl_element011  label="Cl_element : 0.000"  # scripted group (container) (typed FeaturePython)
  n = 3.4e-05
FEATURE [App::DocumentObjectGroupPython] Fe_element006  label="Fe_element : 0.000"  # scripted group (container) (typed FeaturePython)
  n = 5.4e-05
FEATURE [App::DocumentObjectGroupPython] G4_FERROUS_SULFATE  # scripted group (container) (typed FeaturePython)
  Dunit = g/cm3
  Dvalue = 1.024
  Group = -> [H_element040,N_element017,O_element040,Na_element007,S_element011,Cl_element011,Fe_element006]
  conduct = 2
  density = 1
  expand = 3
  formula = G4_FERROUS_SULFATE
  name = G4_FERROUS_SULFATE
  specific = 4
FEATURE [App::DocumentObjectGroupPython] C_element043  label="C_element : 0.099"  # scripted group (container) (typed FeaturePython)
  n = 0.099335
FEATURE [App::DocumentObjectGroupPython] F_element007  label="F_element : 0.314"  # scripted group (container) (typed FeaturePython)
  n = 0.314247
FEATURE [App::DocumentObjectGroupPython] Cl_element012  label="Cl_element : 0.586"  # scripted group (container) (typed FeaturePython)
  n = 0.586418
FEATURE [App::DocumentObjectGroupPython] G4_FREON_12  label="G4_FREON-12"  # scripted group (container) (typed FeaturePython)
  Dunit = g/cm3
  Dvalue = 1.12
  Group = -> [C_element043,F_element007,Cl_element012]
  conduct = 2
  density = 1
  expand = 3
  formula = G4_FREON-12
  name = G4_FREON-12
  specific = 4
FEATURE [App::DocumentObjectGroupPython] C_element044  label="C_element : 0.057"  # scripted group (container) (typed FeaturePython)
  n = 0.057245
FEATURE [App::DocumentObjectGroupPython] F_element008  label="F_element : 0.181"  # scripted group (container) (typed FeaturePython)
  n = 0.181096
FEATURE [App::DocumentObjectGroupPython] Br_element001  label="Br_element : 0.762"  # scripted group (container) (typed FeaturePython)
  n = 0.761659
FEATURE [App::DocumentObjectGroupPython] G4_FREON_12B2  label="G4_FREON-12B2"  # scripted group (container) (typed FeaturePython)
  Dunit = g/cm3
  Dvalue = 1.8
  Group = -> [C_element044,F_element008,Br_element001]
  conduct = 2
  density = 1
  expand = 3
  formula = G4_FREON-12B2
  name = G4_FREON-12B2
  specific = 4
FEATURE [App::DocumentObjectGroupPython] C_element045  label="C_element : 0.115"  # scripted group (container) (typed FeaturePython)
  n = 0.114983
FEATURE [App::DocumentObjectGroupPython] F_element009  label="F_element : 0.546"  # scripted group (container) (typed FeaturePython)
  n = 0.545621
FEATURE [App::DocumentObjectGroupPython] Cl_element013  label="Cl_element : 0.339"  # scripted group (container) (typed FeaturePython)
  n = 0.339396
FEATURE [App::DocumentObjectGroupPython] G4_FREON_13  label="G4_FREON-13"  # scripted group (container) (typed FeaturePython)
  Dunit = g/cm3
  Dvalue = 0.95
  Group = -> [C_element045,F_element009,Cl_element013]
  conduct = 2
  density = 1
  expand = 3
  formula = G4_FREON-13
  name = G4_FREON-13
  specific = 4
FEATURE [App::DocumentObjectGroupPython] C_element046  label="C_element : 025"  # scripted group (container) (typed FeaturePython)
  n = 1
  ref = C_element
FEATURE [App::DocumentObjectGroupPython] F_element010  label="F_element : 3"  # scripted group (container) (typed FeaturePython)
  n = 3
  ref = F_element
FEATURE [App::DocumentObjectGroupPython] Br_element002  label="Br_element : 1"  # scripted group (container) (typed FeaturePython)
  n = 1
  ref = Br_element
FEATURE [App::DocumentObjectGroupPython] G4_FREON_13B1  label="G4_FREON-13B1"  # scripted group (container) (typed FeaturePython)
  Dunit = g/cm3
  Dvalue = 1.5
  Group = -> [C_element046,F_element010,Br_element002]
  conduct = 2
  density = 1
  expand = 3
  formula = G4_FREON-13B1
  name = G4_FREON-13B1
  specific = 4
FEATURE [App::DocumentObjectGroupPython] C_element047  label="C_element : 0.061"  # scripted group (container) (typed FeaturePython)
  n = 0.061309
FEATURE [App::DocumentObjectGroupPython] F_element011  label="F_element : 0.291"  # scripted group (container) (typed FeaturePython)
  n = 0.290924
FEATURE [App::DocumentObjectGroupPython] I_element002  label="I_element : 0.648"  # scripted group (container) (typed FeaturePython)
  n = 0.647767
FEATURE [App::DocumentObjectGroupPython] G4_FREON_13I1  label="G4_FREON-13I1"  # scripted group (container) (typed FeaturePython)
  Dunit = g/cm3
  Dvalue = 1.8
  Group = -> [C_element047,F_element011,I_element002]
  conduct = 2
  density = 1
  expand = 3
  formula = G4_FREON-13I1
  name = G4_FREON-13I1
  specific = 4
FEATURE [App::DocumentObjectGroupPython] Gd_element001  label="Gd_element : 2"  # scripted group (container) (typed FeaturePython)
  n = 2
  ref = Gd_element
FEATURE [App::DocumentObjectGroupPython] O_element041  label="O_element : 021"  # scripted group (container) (typed FeaturePython)
  n = 2
  ref = O_element
FEATURE [App::DocumentObjectGroupPython] S_element012  label="S_element : 004"  # scripted group (container) (typed FeaturePython)
  n = 1
  ref = S_element
FEATURE [App::DocumentObjectGroupPython] G4_GADOLINIUM_OXYSULFIDE  # scripted group (container) (typed FeaturePython)
  Dunit = g/cm3
  Dvalue = 7.44
  Group = -> [Gd_element001,O_element041,S_element012]
  conduct = 2
  density = 1
  expand = 3
  formula = G4_GADOLINIUM_OXYSULFIDE
  name = G4_GADOLINIUM_OXYSULFIDE
  specific = 4
FEATURE [App::DocumentObjectGroupPython] Ga_element001  label="Ga_element : 1"  # scripted group (container) (typed FeaturePython)
  n = 1
  ref = Ga_element
FEATURE [App::DocumentObjectGroupPython] As_element001  label="As_element : 1"  # scripted group (container) (typed FeaturePython)
  n = 1
  ref = As_element
FEATURE [App::DocumentObjectGroupPython] G4_GALLIUM_ARSENIDE  # scripted group (container) (typed FeaturePython)
  Dunit = g/cm3
  Dvalue = 5.31
  Group = -> [Ga_element001,As_element001]
  conduct = 2
  density = 1
  expand = 3
  formula = G4_GALLIUM_ARSENIDE
  name = G4_GALLIUM_ARSENIDE
  specific = 4
FEATURE [App::DocumentObjectGroupPython] H_element041  label="H_element : 0.081"  # scripted group (container) (typed FeaturePython)
  n = 0.08118
FEATURE [App::DocumentObjectGroupPython] C_element048  label="C_element : 0.416"  # scripted group (container) (typed FeaturePython)
  n = 0.41606
FEATURE [App::DocumentObjectGroupPython] N_element018  label="N_element : 0.111"  # scripted group (container) (typed FeaturePython)
  n = 0.11124
FEATURE [App::DocumentObjectGroupPython] O_element042  label="O_element : 0.381"  # scripted group (container) (typed FeaturePython)
  n = 0.38064
FEATURE [App::DocumentObjectGroupPython] S_element013  label="S_element : 0.011"  # scripted group (container) (typed FeaturePython)
  n = 0.01088
FEATURE [App::DocumentObjectGroupPython] G4_GEL_PHOTO_EMULSION  # scripted group (container) (typed FeaturePython)
  Dunit = g/cm3
  Dvalue = 1.2914
  Group = -> [H_element041,C_element048,N_element018,O_element042,S_element013]
  conduct = 2
  density = 1
  expand = 3
  formula = G4_GEL_PHOTO_EMULSION
  name = G4_GEL_PHOTO_EMULSION
  specific = 4
FEATURE [App::DocumentObjectGroupPython] B_element004  label="B_element : 0.040"  # scripted group (container) (typed FeaturePython)
  n = 0.0400639
FEATURE [App::DocumentObjectGroupPython] O_element043  label="O_element : 0.540"  # scripted group (container) (typed FeaturePython)
  n = 0.539561
FEATURE [App::DocumentObjectGroupPython] Na_element008  label="Na_element : 0.028"  # scripted group (container) (typed FeaturePython)
  n = 0.0281909
FEATURE [App::DocumentObjectGroupPython] Al_element003  label="Al_element : 0.012"  # scripted group (container) (typed FeaturePython)
  n = 0.011644
FEATURE [App::DocumentObjectGroupPython] Si_element003  label="Si_element : 0.377"  # scripted group (container) (typed FeaturePython)
  n = 0.377219
FEATURE [App::DocumentObjectGroupPython] K_element004  label="K_element : 0.014"  # scripted group (container) (typed FeaturePython)
  n = 0.00332099
FEATURE [App::DocumentObjectGroupPython] G4_Pyrex_Glass  # scripted group (container) (typed FeaturePython)
  Dunit = g/cm3
  Dvalue = 2.23
  Group = -> [B_element004,O_element043,Na_element008,Al_element003,Si_element003,K_element004]
  conduct = 2
  density = 1
  expand = 3
  formula = G4_Pyrex_Glass
  name = G4_Pyrex_Glass
  specific = 4
FEATURE [App::DocumentObjectGroupPython] O_element044  label="O_element : 0.156"  # scripted group (container) (typed FeaturePython)
  n = 0.156453
FEATURE [App::DocumentObjectGroupPython] Si_element004  label="Si_element : 0.081"  # scripted group (container) (typed FeaturePython)
  n = 0.080866
FEATURE [App::DocumentObjectGroupPython] Ti_element001  label="Ti_element : 0.008"  # scripted group (container) (typed FeaturePython)
  n = 0.008092
FEATURE [App::DocumentObjectGroupPython] As_element002  label="As_element : 0.003"  # scripted group (container) (typed FeaturePython)
  n = 0.002651
FEATURE [App::DocumentObjectGroupPython] Pb_element001  label="Pb_element : 0.752"  # scripted group (container) (typed FeaturePython)
  n = 0.751938
FEATURE [App::DocumentObjectGroupPython] G4_GLASS_LEAD  # scripted group (container) (typed FeaturePython)
  Dunit = g/cm3
  Dvalue = 6.22
  Group = -> [O_element044,Si_element004,Ti_element001,As_element002,Pb_element001]
  conduct = 2
  density = 1
  expand = 3
  formula = G4_GLASS_LEAD
  name = G4_GLASS_LEAD
  specific = 4
FEATURE [App::DocumentObjectGroupPython] O_element045  label="O_element : 0.460"  # scripted group (container) (typed FeaturePython)
  n = 0.4598
FEATURE [App::DocumentObjectGroupPython] Na_element009  label="Na_element : 0.096"  # scripted group (container) (typed FeaturePython)
  n = 0.0964411
FEATURE [App::DocumentObjectGroupPython] Si_element005  label="Si_element : 0.378"  # scripted group (container) (typed FeaturePython)
  n = 0.336553
FEATURE [App::DocumentObjectGroupPython] Ca_element011  label="Ca_element : 0.107"  # scripted group (container) (typed FeaturePython)
  n = 0.107205
FEATURE [App::DocumentObjectGroupPython] G4_GLASS_PLATE  # scripted group (container) (typed FeaturePython)
  Dunit = g/cm3
  Dvalue = 2.4
  Group = -> [O_element045,Na_element009,Si_element005,Ca_element011]
  conduct = 2
  density = 1
  expand = 3
  formula = G4_GLASS_PLATE
  name = G4_GLASS_PLATE
  specific = 4
FEATURE [App::DocumentObjectGroupPython] C_element049  label="C_element : 026"  # scripted group (container) (typed FeaturePython)
  n = 5
  ref = C_element
FEATURE [App::DocumentObjectGroupPython] H_element042  label="H_element : 021"  # scripted group (container) (typed FeaturePython)
  n = 10
  ref = H_element
FEATURE [App::DocumentObjectGroupPython] N_element019  label="N_element : 2"  # scripted group (container) (typed FeaturePython)
  n = 2
  ref = N_element
FEATURE [App::DocumentObjectGroupPython] O_element046  label="O_element : 022"  # scripted group (container) (typed FeaturePython)
  n = 3
  ref = O_element
FEATURE [App::DocumentObjectGroupPython] G4_GLUTAMINE  # scripted group (container) (typed FeaturePython)
  Dunit = g/cm3
  Dvalue = 1.46
  Group = -> [C_element049,H_element042,N_element019,O_element046]
  conduct = 2
  density = 1
  expand = 3
  formula = G4_GLUTAMINE
  name = G4_GLUTAMINE
  specific = 4
FEATURE [App::DocumentObjectGroupPython] C_element050  label="C_element : 027"  # scripted group (container) (typed FeaturePython)
  n = 3
  ref = C_element
FEATURE [App::DocumentObjectGroupPython] H_element043  label="H_element : 022"  # scripted group (container) (typed FeaturePython)
  n = 8
  ref = H_element
FEATURE [App::DocumentObjectGroupPython] O_element047  label="O_element : 023"  # scripted group (container) (typed FeaturePython)
  n = 3
  ref = O_element
FEATURE [App::DocumentObjectGroupPython] G4_GLYCEROL  # scripted group (container) (typed FeaturePython)
  Dunit = g/cm3
  Dvalue = 1.2613
  Group = -> [C_element050,H_element043,O_element047]
  conduct = 2
  density = 1
  expand = 3
  formula = G4_GLYCEROL
  name = G4_GLYCEROL
  specific = 4
FEATURE [App::DocumentObjectGroupPython] C_element051  label="C_element : 028"  # scripted group (container) (typed FeaturePython)
  n = 5
  ref = C_element
FEATURE [App::DocumentObjectGroupPython] H_element044  label="H_element : 023"  # scripted group (container) (typed FeaturePython)
  n = 5
  ref = H_element
FEATURE [App::DocumentObjectGroupPython] N_element020  label="N_element : 009"  # scripted group (container) (typed FeaturePython)
  n = 5
  ref = N_element
FEATURE [App::DocumentObjectGroupPython] O_element048  label="O_element : 024"  # scripted group (container) (typed FeaturePython)
  n = 1
  ref = O_element
FEATURE [App::DocumentObjectGroupPython] G4_GUANINE  # scripted group (container) (typed FeaturePython)
  Dunit = g/cm3
  Dvalue = 2.2
  Group = -> [C_element051,H_element044,N_element020,O_element048]
  conduct = 2
  density = 1
  expand = 3
  formula = G4_GUANINE
  name = G4_GUANINE
  specific = 4
FEATURE [App::DocumentObjectGroupPython] Ca_element012  label="Ca_element : 006"  # scripted group (container) (typed FeaturePython)
  n = 1
  ref = Ca_element
FEATURE [App::DocumentObjectGroupPython] S_element014  label="S_element : 005"  # scripted group (container) (typed FeaturePython)
  n = 1
  ref = S_element
FEATURE [App::DocumentObjectGroupPython] O_element049  label="O_element : 6"  # scripted group (container) (typed FeaturePython)
  n = 6
  ref = O_element
FEATURE [App::DocumentObjectGroupPython] H_element045  label="H_element : 024"  # scripted group (container) (typed FeaturePython)
  n = 4
  ref = H_element
FEATURE [App::DocumentObjectGroupPython] G4_GYPSUM  # scripted group (container) (typed FeaturePython)
  Dunit = g/cm3
  Dvalue = 2.32
  Group = -> [Ca_element012,S_element014,O_element049,H_element045]
  conduct = 2
  density = 1
  expand = 3
  formula = G4_GYPSUM
  name = G4_GYPSUM
  specific = 4
FEATURE [App::DocumentObjectGroupPython] C_element052  label="C_element : 7"  # scripted group (container) (typed FeaturePython)
  n = 7
  ref = C_element
FEATURE [App::DocumentObjectGroupPython] H_element046  label="H_element : 16"  # scripted group (container) (typed FeaturePython)
  n = 16
  ref = H_element
FEATURE [App::DocumentObjectGroupPython] G4_N_HEPTANE  label="G4_N-HEPTANE"  # scripted group (container) (typed FeaturePython)
  Dunit = g/cm3
  Dvalue = 0.68376
  Group = -> [C_element052,H_element046]
  conduct = 2
  density = 1
  expand = 3
  formula = G4_N-HEPTANE
  name = G4_N-HEPTANE
  specific = 4
FEATURE [App::DocumentObjectGroupPython] C_element053  label="C_element : 029"  # scripted group (container) (typed FeaturePython)
  n = 6
  ref = C_element
FEATURE [App::DocumentObjectGroupPython] H_element047  label="H_element : 14"  # scripted group (container) (typed FeaturePython)
  n = 14
  ref = H_element
FEATURE [App::DocumentObjectGroupPython] G4_N_HEXANE  label="G4_N-HEXANE"  # scripted group (container) (typed FeaturePython)
  Dunit = g/cm3
  Dvalue = 0.6603
  Group = -> [C_element053,H_element047]
  conduct = 2
  density = 1
  expand = 3
  formula = G4_N-HEXANE
  name = G4_N-HEXANE
  specific = 4
FEATURE [App::DocumentObjectGroupPython] C_element054  label="C_element : 22"  # scripted group (container) (typed FeaturePython)
  n = 22
  ref = C_element
FEATURE [App::DocumentObjectGroupPython] H_element048  label="H_element : 025"  # scripted group (container) (typed FeaturePython)
  n = 10
  ref = H_element
FEATURE [App::DocumentObjectGroupPython] N_element021  label="N_element : 010"  # scripted group (container) (typed FeaturePython)
  n = 2
  ref = N_element
FEATURE [App::DocumentObjectGroupPython] O_element050  label="O_element : 025"  # scripted group (container) (typed FeaturePython)
  n = 5
  ref = O_element
FEATURE [App::DocumentObjectGroupPython] G4_KAPTON  # scripted group (container) (typed FeaturePython)
  Dunit = g/cm3
  Dvalue = 1.42
  Group = -> [C_element054,H_element048,N_element021,O_element050]
  conduct = 2
  density = 1
  expand = 3
  formula = G4_KAPTON
  name = G4_KAPTON
  specific = 4
FEATURE [App::DocumentObjectGroupPython] La_element001  label="La_element : 1"  # scripted group (container) (typed FeaturePython)
  n = 1
  ref = La_element
FEATURE [App::DocumentObjectGroupPython] Br_element003  label="Br_element : 002"  # scripted group (container) (typed FeaturePython)
  n = 1
  ref = Br_element
FEATURE [App::DocumentObjectGroupPython] O_element051  label="O_element : 026"  # scripted group (container) (typed FeaturePython)
  n = 1
  ref = O_element
FEATURE [App::DocumentObjectGroupPython] G4_LANTHANUM_OXYBROMIDE  # scripted group (container) (typed FeaturePython)
  Dunit = g/cm3
  Dvalue = 6.28
  Group = -> [La_element001,Br_element003,O_element051]
  conduct = 2
  density = 1
  expand = 3
  formula = G4_LANTHANUM_OXYBROMIDE
  name = G4_LANTHANUM_OXYBROMIDE
  specific = 4
FEATURE [App::DocumentObjectGroupPython] La_element002  label="La_element : 2"  # scripted group (container) (typed FeaturePython)
  n = 2
  ref = La_element
FEATURE [App::DocumentObjectGroupPython] O_element052  label="O_element : 027"  # scripted group (container) (typed FeaturePython)
  n = 2
  ref = O_element
FEATURE [App::DocumentObjectGroupPython] S_element015  label="S_element : 006"  # scripted group (container) (typed FeaturePython)
  n = 1
  ref = S_element
FEATURE [App::DocumentObjectGroupPython] G4_LANTHANUM_OXYSULFIDE  # scripted group (container) (typed FeaturePython)
  Dunit = g/cm3
  Dvalue = 5.86
  Group = -> [La_element002,O_element052,S_element015]
  conduct = 2
  density = 1
  expand = 3
  formula = G4_LANTHANUM_OXYSULFIDE
  name = G4_LANTHANUM_OXYSULFIDE
  specific = 4
FEATURE [App::DocumentObjectGroupPython] O_element053  label="O_element : 0.072"  # scripted group (container) (typed FeaturePython)
  n = 0.071682
FEATURE [App::DocumentObjectGroupPython] Pb_element002  label="Pb_element : 0.928"  # scripted group (container) (typed FeaturePython)
  n = 0.928318
FEATURE [App::DocumentObjectGroupPython] G4_LEAD_OXIDE  # scripted group (container) (typed FeaturePython)
  Dunit = g/cm3
  Dvalue = 9.53
  Group = -> [O_element053,Pb_element002]
  conduct = 2
  density = 1
  expand = 3
  formula = G4_LEAD_OXIDE
  name = G4_LEAD_OXIDE
  specific = 4
FEATURE [App::DocumentObjectGroupPython] Li_element001  label="Li_element : 1"  # scripted group (container) (typed FeaturePython)
  n = 1
  ref = Li_element
FEATURE [App::DocumentObjectGroupPython] N_element022  label="N_element : 011"  # scripted group (container) (typed FeaturePython)
  n = 1
  ref = N_element
FEATURE [App::DocumentObjectGroupPython] H_element049  label="H_element : 026"  # scripted group (container) (typed FeaturePython)
  n = 2
  ref = H_element
FEATURE [App::DocumentObjectGroupPython] G4_LITHIUM_AMIDE  # scripted group (container) (typed FeaturePython)
  Dunit = g/cm3
  Dvalue = 1.178
  Group = -> [Li_element001,N_element022,H_element049]
  conduct = 2
  density = 1
  expand = 3
  formula = G4_LITHIUM_AMIDE
  name = G4_LITHIUM_AMIDE
  specific = 4
FEATURE [App::DocumentObjectGroupPython] Li_element002  label="Li_element : 2"  # scripted group (container) (typed FeaturePython)
  n = 2
  ref = Li_element
FEATURE [App::DocumentObjectGroupPython] C_element055  label="C_element : 030"  # scripted group (container) (typed FeaturePython)
  n = 1
  ref = C_element
FEATURE [App::DocumentObjectGroupPython] O_element054  label="O_element : 028"  # scripted group (container) (typed FeaturePython)
  n = 3
  ref = O_element
FEATURE [App::DocumentObjectGroupPython] G4_LITHIUM_CARBONATE  # scripted group (container) (typed FeaturePython)
  Dunit = g/cm3
  Dvalue = 2.11
  Group = -> [Li_element002,C_element055,O_element054]
  conduct = 2
  density = 1
  expand = 3
  formula = G4_LITHIUM_CARBONATE
  name = G4_LITHIUM_CARBONATE
  specific = 4
FEATURE [App::DocumentObjectGroupPython] Li_element003  label="Li_element : 003"  # scripted group (container) (typed FeaturePython)
  n = 1
  ref = Li_element
FEATURE [App::DocumentObjectGroupPython] F_element012  label="F_element : 004"  # scripted group (container) (typed FeaturePython)
  n = 1
  ref = F_element
FEATURE [App::DocumentObjectGroupPython] G4_LITHIUM_FLUORIDE  # scripted group (container) (typed FeaturePython)
  Dunit = g/cm3
  Dvalue = 2.635
  Group = -> [Li_element003,F_element012]
  conduct = 2
  density = 1
  expand = 3
  formula = G4_LITHIUM_FLUORIDE
  name = G4_LITHIUM_FLUORIDE
  specific = 4
FEATURE [App::DocumentObjectGroupPython] Li_element004  label="Li_element : 004"  # scripted group (container) (typed FeaturePython)
  n = 1
  ref = Li_element
FEATURE [App::DocumentObjectGroupPython] H_element050  label="H_element : 027"  # scripted group (container) (typed FeaturePython)
  n = 1
  ref = H_element
FEATURE [App::DocumentObjectGroupPython] G4_LITHIUM_HYDRIDE  # scripted group (container) (typed FeaturePython)
  Dunit = g/cm3
  Dvalue = 0.82
  Group = -> [Li_element004,H_element050]
  conduct = 2
  density = 1
  expand = 3
  formula = G4_LITHIUM_HYDRIDE
  name = G4_LITHIUM_HYDRIDE
  specific = 4
FEATURE [App::DocumentObjectGroupPython] Li_element005  label="Li_element : 005"  # scripted group (container) (typed FeaturePython)
  n = 1
  ref = Li_element
FEATURE [App::DocumentObjectGroupPython] I_element003  label="I_element : 002"  # scripted group (container) (typed FeaturePython)
  n = 1
  ref = I_element
FEATURE [App::DocumentObjectGroupPython] G4_LITHIUM_IODIDE  # scripted group (container) (typed FeaturePython)
  Dunit = g/cm3
  Dvalue = 3.494
  Group = -> [Li_element005,I_element003]
  conduct = 2
  density = 1
  expand = 3
  formula = G4_LITHIUM_IODIDE
  name = G4_LITHIUM_IODIDE
  specific = 4
FEATURE [App::DocumentObjectGroupPython] Li_element006  label="Li_element : 006"  # scripted group (container) (typed FeaturePython)
  n = 2
  ref = Li_element
FEATURE [App::DocumentObjectGroupPython] O_element055  label="O_element : 029"  # scripted group (container) (typed FeaturePython)
  n = 1
  ref = O_element
FEATURE [App::DocumentObjectGroupPython] G4_LITHIUM_OXIDE  # scripted group (container) (typed FeaturePython)
  Dunit = g/cm3
  Dvalue = 2.013
  Group = -> [Li_element006,O_element055]
  conduct = 2
  density = 1
  expand = 3
  formula = G4_LITHIUM_OXIDE
  name = G4_LITHIUM_OXIDE
  specific = 4
FEATURE [App::DocumentObjectGroupPython] Li_element007  label="Li_element : 007"  # scripted group (container) (typed FeaturePython)
  n = 2
  ref = Li_element
FEATURE [App::DocumentObjectGroupPython] B_element005  label="B_element : 005"  # scripted group (container) (typed FeaturePython)
  n = 4
  ref = B_element
FEATURE [App::DocumentObjectGroupPython] O_element056  label="O_element : 7"  # scripted group (container) (typed FeaturePython)
  n = 7
  ref = O_element
FEATURE [App::DocumentObjectGroupPython] G4_LITHIUM_TETRABORATE  # scripted group (container) (typed FeaturePython)
  Dunit = g/cm3
  Dvalue = 2.44
  Group = -> [Li_element007,B_element005,O_element056]
  conduct = 2
  density = 1
  expand = 3
  formula = G4_LITHIUM_TETRABORATE
  name = G4_LITHIUM_TETRABORATE
  specific = 4
FEATURE [App::DocumentObjectGroupPython] H_element051  label="H_element : 0.105"  # scripted group (container) (typed FeaturePython)
  n = 0.105
FEATURE [App::DocumentObjectGroupPython] C_element056  label="C_element : 0.083"  # scripted group (container) (typed FeaturePython)
  n = 0.083
FEATURE [App::DocumentObjectGroupPython] N_element023  label="N_element : 0.023"  # scripted group (container) (typed FeaturePython)
  n = 0.023
FEATURE [App::DocumentObjectGroupPython] O_element057  label="O_element : 0.779"  # scripted group (container) (typed FeaturePython)
  n = 0.779
FEATURE [App::DocumentObjectGroupPython] Na_element010  label="Na_element : 0.097"  # scripted group (container) (typed FeaturePython)
  n = 0.002
FEATURE [App::DocumentObjectGroupPython] P_element006  label="P_element : 0.105"  # scripted group (container) (typed FeaturePython)
  n = 0.001
FEATURE [App::DocumentObjectGroupPython] S_element016  label="S_element : 0.017"  # scripted group (container) (typed FeaturePython)
  n = 0.002
FEATURE [App::DocumentObjectGroupPython] Cl_element014  label="Cl_element : 0.587"  # scripted group (container) (typed FeaturePython)
  n = 0.003
FEATURE [App::DocumentObjectGroupPython] K_element005  label="K_element : 0.015"  # scripted group (container) (typed FeaturePython)
  n = 0.002
FEATURE [App::DocumentObjectGroupPython] G4_LUNG_ICRP  # scripted group (container) (typed FeaturePython)
  Dunit = g/cm3
  Dvalue = 1.04
  Group = -> [H_element051,C_element056,N_element023,O_element057,Na_element010,P_element006,S_element016,Cl_element014,K_element005]
  conduct = 2
  density = 1
  expand = 3
  formula = G4_LUNG_ICRP
  name = G4_LUNG_ICRP
  specific = 4
FEATURE [App::DocumentObjectGroupPython] H_element052  label="H_element : 0.116"  # scripted group (container) (typed FeaturePython)
  n = 0.114318
FEATURE [App::DocumentObjectGroupPython] C_element057  label="C_element : 0.656"  # scripted group (container) (typed FeaturePython)
  n = 0.655824
FEATURE [App::DocumentObjectGroupPython] O_element058  label="O_element : 0.092"  # scripted group (container) (typed FeaturePython)
  n = 0.0921831
FEATURE [App::DocumentObjectGroupPython] Mg_element004  label="Mg_element : 0.135"  # scripted group (container) (typed FeaturePython)
  n = 0.134792
FEATURE [App::DocumentObjectGroupPython] Ca_element013  label="Ca_element : 0.003"  # scripted group (container) (typed FeaturePython)
  n = 0.002883
FEATURE [App::DocumentObjectGroupPython] G4_M3_WAX  # scripted group (container) (typed FeaturePython)
  Dunit = g/cm3
  Dvalue = 1.05
  Group = -> [H_element052,C_element057,O_element058,Mg_element004,Ca_element013]
  conduct = 2
  density = 1
  expand = 3
  formula = G4_M3_WAX
  name = G4_M3_WAX
  specific = 4
FEATURE [App::DocumentObjectGroupPython] Mg_element005  label="Mg_element : 1"  # scripted group (container) (typed FeaturePython)
  n = 1
  ref = Mg_element
FEATURE [App::DocumentObjectGroupPython] C_element058  label="C_element : 031"  # scripted group (container) (typed FeaturePython)
  n = 1
  ref = C_element
FEATURE [App::DocumentObjectGroupPython] O_element059  label="O_element : 030"  # scripted group (container) (typed FeaturePython)
  n = 3
  ref = O_element
FEATURE [App::DocumentObjectGroupPython] G4_MAGNESIUM_CARBONATE  # scripted group (container) (typed FeaturePython)
  Dunit = g/cm3
  Dvalue = 2.958
  Group = -> [Mg_element005,C_element058,O_element059]
  conduct = 2
  density = 1
  expand = 3
  formula = G4_MAGNESIUM_CARBONATE
  name = G4_MAGNESIUM_CARBONATE
  specific = 4
FEATURE [App::DocumentObjectGroupPython] Mg_element006  label="Mg_element : 002"  # scripted group (container) (typed FeaturePython)
  n = 1
  ref = Mg_element
FEATURE [App::DocumentObjectGroupPython] F_element013  label="F_element : 005"  # scripted group (container) (typed FeaturePython)
  n = 2
  ref = F_element
FEATURE [App::DocumentObjectGroupPython] G4_MAGNESIUM_FLUORIDE  # scripted group (container) (typed FeaturePython)
  Dunit = g/cm3
  Dvalue = 3
  Group = -> [Mg_element006,F_element013]
  conduct = 2
  density = 1
  expand = 3
  formula = G4_MAGNESIUM_FLUORIDE
  name = G4_MAGNESIUM_FLUORIDE
  specific = 4
FEATURE [App::DocumentObjectGroupPython] Mg_element007  label="Mg_element : 003"  # scripted group (container) (typed FeaturePython)
  n = 1
  ref = Mg_element
FEATURE [App::DocumentObjectGroupPython] O_element060  label="O_element : 031"  # scripted group (container) (typed FeaturePython)
  n = 1
  ref = O_element
FEATURE [App::DocumentObjectGroupPython] G4_MAGNESIUM_OXIDE  # scripted group (container) (typed FeaturePython)
  Dunit = g/cm3
  Dvalue = 3.58
  Group = -> [Mg_element007,O_element060]
  conduct = 2
  density = 1
  expand = 3
  formula = G4_MAGNESIUM_OXIDE
  name = G4_MAGNESIUM_OXIDE
  specific = 4
FEATURE [App::DocumentObjectGroupPython] Mg_element008  label="Mg_element : 004"  # scripted group (container) (typed FeaturePython)
  n = 1
  ref = Mg_element
FEATURE [App::DocumentObjectGroupPython] B_element006  label="B_element : 006"  # scripted group (container) (typed FeaturePython)
  n = 4
  ref = B_element
FEATURE [App::DocumentObjectGroupPython] O_element061  label="O_element : 032"  # scripted group (container) (typed FeaturePython)
  n = 7
  ref = O_element
FEATURE [App::DocumentObjectGroupPython] G4_MAGNESIUM_TETRABORATE  # scripted group (container) (typed FeaturePython)
  Dunit = g/cm3
  Dvalue = 2.53
  Group = -> [Mg_element008,B_element006,O_element061]
  conduct = 2
  density = 1
  expand = 3
  formula = G4_MAGNESIUM_TETRABORATE
  name = G4_MAGNESIUM_TETRABORATE
  specific = 4
FEATURE [App::DocumentObjectGroupPython] Hg_element001  label="Hg_element : 1"  # scripted group (container) (typed FeaturePython)
  n = 1
  ref = Hg_element
FEATURE [App::DocumentObjectGroupPython] I_element004  label="I_element : 2"  # scripted group (container) (typed FeaturePython)
  n = 2
  ref = I_element
FEATURE [App::DocumentObjectGroupPython] G4_MERCURIC_IODIDE  # scripted group (container) (typed FeaturePython)
  Dunit = g/cm3
  Dvalue = 6.36
  Group = -> [Hg_element001,I_element004]
  conduct = 2
  density = 1
  expand = 3
  formula = G4_MERCURIC_IODIDE
  name = G4_MERCURIC_IODIDE
  specific = 4
FEATURE [App::DocumentObjectGroupPython] C_element059  label="C_element : 032"  # scripted group (container) (typed FeaturePython)
  n = 1
  ref = C_element
FEATURE [App::DocumentObjectGroupPython] H_element053  label="H_element : 028"  # scripted group (container) (typed FeaturePython)
  n = 4
  ref = H_element
FEATURE [App::DocumentObjectGroupPython] G4_METHANE  # scripted group (container) (typed FeaturePython)
  Dunit = g/cm3
  Dvalue = 0.000667151
  Group = -> [C_element059,H_element053]
  conduct = 2
  density = 1
  expand = 3
  formula = G4_METHANE
  name = G4_METHANE
  specific = 4
FEATURE [App::DocumentObjectGroupPython] C_element060  label="C_element : 033"  # scripted group (container) (typed FeaturePython)
  n = 1
  ref = C_element
FEATURE [App::DocumentObjectGroupPython] H_element054  label="H_element : 029"  # scripted group (container) (typed FeaturePython)
  n = 4
  ref = H_element
FEATURE [App::DocumentObjectGroupPython] O_element062  label="O_element : 033"  # scripted group (container) (typed FeaturePython)
  n = 1
  ref = O_element
FEATURE [App::DocumentObjectGroupPython] G4_METHANOL  # scripted group (container) (typed FeaturePython)
  Dunit = g/cm3
  Dvalue = 0.7914
  Group = -> [C_element060,H_element054,O_element062]
  conduct = 2
  density = 1
  expand = 3
  formula = G4_METHANOL
  name = G4_METHANOL
  specific = 4
FEATURE [App::DocumentObjectGroupPython] H_element055  label="H_element : 0.134"  # scripted group (container) (typed FeaturePython)
  n = 0.13404
FEATURE [App::DocumentObjectGroupPython] C_element061  label="C_element : 0.778"  # scripted group (container) (typed FeaturePython)
  n = 0.77796
FEATURE [App::DocumentObjectGroupPython] O_element063  label="O_element : 0.035"  # scripted group (container) (typed FeaturePython)
  n = 0.03502
FEATURE [App::DocumentObjectGroupPython] Mg_element009  label="Mg_element : 0.039"  # scripted group (container) (typed FeaturePython)
  n = 0.038594
FEATURE [App::DocumentObjectGroupPython] Ti_element002  label="Ti_element : 0.014"  # scripted group (container) (typed FeaturePython)
  n = 0.014386
FEATURE [App::DocumentObjectGroupPython] G4_MIX_D_WAX  # scripted group (container) (typed FeaturePython)
  Dunit = g/cm3
  Dvalue = 0.99
  Group = -> [H_element055,C_element061,O_element063,Mg_element009,Ti_element002]
  conduct = 2
  density = 1
  expand = 3
  formula = G4_MIX_D_WAX
  name = G4_MIX_D_WAX
  specific = 4
FEATURE [App::DocumentObjectGroupPython] H_element056  label="H_element : 0.135"  # scripted group (container) (typed FeaturePython)
  n = 0.081192
FEATURE [App::DocumentObjectGroupPython] C_element062  label="C_element : 0.583"  # scripted group (container) (typed FeaturePython)
  n = 0.583442
FEATURE [App::DocumentObjectGroupPython] N_element024  label="N_element : 0.018"  # scripted group (container) (typed FeaturePython)
  n = 0.017798
FEATURE [App::DocumentObjectGroupPython] O_element064  label="O_element : 0.186"  # scripted group (container) (typed FeaturePython)
  n = 0.186381
FEATURE [App::DocumentObjectGroupPython] Mg_element010  label="Mg_element : 0.130"  # scripted group (container) (typed FeaturePython)
  n = 0.130287
FEATURE [App::DocumentObjectGroupPython] Cl_element015  label="Cl_element : 0.588"  # scripted group (container) (typed FeaturePython)
  n = 0.0009
FEATURE [App::DocumentObjectGroupPython] G4_MS20_TISSUE  # scripted group (container) (typed FeaturePython)
  Dunit = g/cm3
  Dvalue = 1
  Group = -> [H_element056,C_element062,N_element024,O_element064,Mg_element010,Cl_element015]
  conduct = 2
  density = 1
  expand = 3
  formula = G4_MS20_TISSUE
  name = G4_MS20_TISSUE
  specific = 4
FEATURE [App::DocumentObjectGroupPython] H_element057  label="H_element : 0.136"  # scripted group (container) (typed FeaturePython)
  n = 0.102
FEATURE [App::DocumentObjectGroupPython] C_element063  label="C_element : 0.143"  # scripted group (container) (typed FeaturePython)
  n = 0.143
FEATURE [App::DocumentObjectGroupPython] N_element025  label="N_element : 0.034"  # scripted group (container) (typed FeaturePython)
  n = 0.034
FEATURE [App::DocumentObjectGroupPython] O_element065  label="O_element : 0.710"  # scripted group (container) (typed FeaturePython)
  n = 0.71
FEATURE [App::DocumentObjectGroupPython] Na_element011  label="Na_element : 0.098"  # scripted group (container) (typed FeaturePython)
  n = 0.001
FEATURE [App::DocumentObjectGroupPython] P_element007  label="P_element : 0.002"  # scripted group (container) (typed FeaturePython)
  n = 0.002
FEATURE [App::DocumentObjectGroupPython] S_element017  label="S_element : 0.018"  # scripted group (container) (typed FeaturePython)
  n = 0.003
FEATURE [App::DocumentObjectGroupPython] Cl_element016  label="Cl_element : 0.589"  # scripted group (container) (typed FeaturePython)
  n = 0.001
FEATURE [App::DocumentObjectGroupPython] K_element006  label="K_element : 0.004"  # scripted group (container) (typed FeaturePython)
  n = 0.004
FEATURE [App::DocumentObjectGroupPython] G4_MUSCLE_SKELETAL_ICRP  # scripted group (container) (typed FeaturePython)
  Dunit = g/cm3
  Dvalue = 1.05
  Group = -> [H_element057,C_element063,N_element025,O_element065,Na_element011,P_element007,S_element017,Cl_element016,K_element006]
  conduct = 2
  density = 1
  expand = 3
  formula = G4_MUSCLE_SKELETAL_ICRP
  name = G4_MUSCLE_SKELETAL_ICRP
  specific = 4
FEATURE [App::DocumentObjectGroupPython] H_element058  label="H_element : 0.137"  # scripted group (container) (typed FeaturePython)
  n = 0.102102
FEATURE [App::DocumentObjectGroupPython] C_element064  label="C_element : 0.123"  # scripted group (container) (typed FeaturePython)
  n = 0.123123
FEATURE [App::DocumentObjectGroupPython] N_element026  label="N_element : 0.756"  # scripted group (container) (typed FeaturePython)
  n = 0.035035
FEATURE [App::DocumentObjectGroupPython] O_element066  label="O_element : 0.730"  # scripted group (container) (typed FeaturePython)
  n = 0.72973
FEATURE [App::DocumentObjectGroupPython] Na_element012  label="Na_element : 0.099"  # scripted group (container) (typed FeaturePython)
  n = 0.001001
FEATURE [App::DocumentObjectGroupPython] P_element008  label="P_element : 0.106"  # scripted group (container) (typed FeaturePython)
  n = 0.002002
FEATURE [App::DocumentObjectGroupPython] S_element018  label="S_element : 0.019"  # scripted group (container) (typed FeaturePython)
  n = 0.004004
FEATURE [App::DocumentObjectGroupPython] K_element007  label="K_element : 0.016"  # scripted group (container) (typed FeaturePython)
  n = 0.003003
FEATURE [App::DocumentObjectGroupPython] G4_MUSCLE_STRIATED_ICRU  # scripted group (container) (typed FeaturePython)
  Dunit = g/cm3
  Dvalue = 1.04
  Group = -> [H_element058,C_element064,N_element026,O_element066,Na_element012,P_element008,S_element018,K_element007]
  conduct = 2
  density = 1
  expand = 3
  formula = G4_MUSCLE_STRIATED_ICRU
  name = G4_MUSCLE_STRIATED_ICRU
  specific = 4
FEATURE [App::DocumentObjectGroupPython] H_element059  label="H_element : 0.098"  # scripted group (container) (typed FeaturePython)
  n = 0.0982341
FEATURE [App::DocumentObjectGroupPython] C_element065  label="C_element : 0.156"  # scripted group (container) (typed FeaturePython)
  n = 0.156214
FEATURE [App::DocumentObjectGroupPython] N_element027  label="N_element : 0.757"  # scripted group (container) (typed FeaturePython)
  n = 0.035451
FEATURE [App::DocumentObjectGroupPython] O_element067  label="O_element : 0.880"  # scripted group (container) (typed FeaturePython)
  n = 0.710101
FEATURE [App::DocumentObjectGroupPython] G4_MUSCLE_WITH_SUCROSE  # scripted group (container) (typed FeaturePython)
  Dunit = g/cm3
  Dvalue = 1.11
  Group = -> [H_element059,C_element065,N_element027,O_element067]
  conduct = 2
  density = 1
  expand = 3
  formula = G4_MUSCLE_WITH_SUCROSE
  name = G4_MUSCLE_WITH_SUCROSE
  specific = 4
FEATURE [App::DocumentObjectGroupPython] H_element060  label="H_element : 0.138"  # scripted group (container) (typed FeaturePython)
  n = 0.101969
FEATURE [App::DocumentObjectGroupPython] C_element066  label="C_element : 0.120"  # scripted group (container) (typed FeaturePython)
  n = 0.120058
FEATURE [App::DocumentObjectGroupPython] N_element028  label="N_element : 0.758"  # scripted group (container) (typed FeaturePython)
  n = 0.035451
FEATURE [App::DocumentObjectGroupPython] O_element068  label="O_element : 0.743"  # scripted group (container) (typed FeaturePython)
  n = 0.742522
FEATURE [App::DocumentObjectGroupPython] G4_MUSCLE_WITHOUT_SUCROSE  # scripted group (container) (typed FeaturePython)
  Dunit = g/cm3
  Dvalue = 1.07
  Group = -> [H_element060,C_element066,N_element028,O_element068]
  conduct = 2
  density = 1
  expand = 3
  formula = G4_MUSCLE_WITHOUT_SUCROSE
  name = G4_MUSCLE_WITHOUT_SUCROSE
  specific = 4
FEATURE [App::DocumentObjectGroupPython] C_element067  label="C_element : 10"  # scripted group (container) (typed FeaturePython)
  n = 10
  ref = C_element
FEATURE [App::DocumentObjectGroupPython] H_element061  label="H_element : 030"  # scripted group (container) (typed FeaturePython)
  n = 8
  ref = H_element
FEATURE [App::DocumentObjectGroupPython] G4_NAPHTHALENE  # scripted group (container) (typed FeaturePython)
  Dunit = g/cm3
  Dvalue = 1.145
  Group = -> [C_element067,H_element061]
  conduct = 2
  density = 1
  expand = 3
  formula = G4_NAPHTHALENE
  name = G4_NAPHTHALENE
  specific = 4
FEATURE [App::DocumentObjectGroupPython] C_element068  label="C_element : 034"  # scripted group (container) (typed FeaturePython)
  n = 6
  ref = C_element
FEATURE [App::DocumentObjectGroupPython] H_element062  label="H_element : 031"  # scripted group (container) (typed FeaturePython)
  n = 5
  ref = H_element
FEATURE [App::DocumentObjectGroupPython] N_element029  label="N_element : 012"  # scripted group (container) (typed FeaturePython)
  n = 1
  ref = N_element
FEATURE [App::DocumentObjectGroupPython] O_element069  label="O_element : 034"  # scripted group (container) (typed FeaturePython)
  n = 2
  ref = O_element
FEATURE [App::DocumentObjectGroupPython] G4_NITROBENZENE  # scripted group (container) (typed FeaturePython)
  Dunit = g/cm3
  Dvalue = 1.19867
  Group = -> [C_element068,H_element062,N_element029,O_element069]
  conduct = 2
  density = 1
  expand = 3
  formula = G4_NITROBENZENE
  name = G4_NITROBENZENE
  specific = 4
FEATURE [App::DocumentObjectGroupPython] N_element030  label="N_element : 013"  # scripted group (container) (typed FeaturePython)
  n = 2
  ref = N_element
FEATURE [App::DocumentObjectGroupPython] O_element070  label="O_element : 035"  # scripted group (container) (typed FeaturePython)
  n = 1
  ref = O_element
FEATURE [App::DocumentObjectGroupPython] G4_NITROUS_OXIDE  # scripted group (container) (typed FeaturePython)
  Dunit = g/cm3
  Dvalue = 0.00183094
  Group = -> [N_element030,O_element070]
  conduct = 2
  density = 1
  expand = 3
  formula = G4_NITROUS_OXIDE
  name = G4_NITROUS_OXIDE
  specific = 4
FEATURE [App::DocumentObjectGroupPython] H_element063  label="H_element : 0.104"  # scripted group (container) (typed FeaturePython)
  n = 0.103509
FEATURE [App::DocumentObjectGroupPython] C_element069  label="C_element : 0.648"  # scripted group (container) (typed FeaturePython)
  n = 0.648416
FEATURE [App::DocumentObjectGroupPython] N_element031  label="N_element : 0.100"  # scripted group (container) (typed FeaturePython)
  n = 0.0995361
FEATURE [App::DocumentObjectGroupPython] O_element071  label="O_element : 0.149"  # scripted group (container) (typed FeaturePython)
  n = 0.148539
FEATURE [App::DocumentObjectGroupPython] G4_NYLON_8062  label="G4_NYLON-8062"  # scripted group (container) (typed FeaturePython)
  Dunit = g/cm3
  Dvalue = 1.08
  Group = -> [H_element063,C_element069,N_element031,O_element071]
  conduct = 2
  density = 1
  expand = 3
  formula = G4_NYLON-8062
  name = G4_NYLON-8062
  specific = 4
FEATURE [App::DocumentObjectGroupPython] C_element070  label="C_element : 035"  # scripted group (container) (typed FeaturePython)
  n = 6
  ref = C_element
FEATURE [App::DocumentObjectGroupPython] H_element064  label="H_element : 11"  # scripted group (container) (typed FeaturePython)
  n = 11
  ref = H_element
FEATURE [App::DocumentObjectGroupPython] N_element032  label="N_element : 014"  # scripted group (container) (typed FeaturePython)
  n = 1
  ref = N_element
FEATURE [App::DocumentObjectGroupPython] O_element072  label="O_element : 036"  # scripted group (container) (typed FeaturePython)
  n = 1
  ref = O_element
FEATURE [App::DocumentObjectGroupPython] G4_NYLON_6_6  label="G4_NYLON-6-6"  # scripted group (container) (typed FeaturePython)
  Dunit = g/cm3
  Dvalue = 1.14
  Group = -> [C_element070,H_element064,N_element032,O_element072]
  conduct = 2
  density = 1
  expand = 3
  formula = G4_NYLON-6-6
  name = G4_NYLON-6-6
  specific = 4
FEATURE [App::DocumentObjectGroupPython] H_element065  label="H_element : 0.139"  # scripted group (container) (typed FeaturePython)
  n = 0.107062
FEATURE [App::DocumentObjectGroupPython] C_element071  label="C_element : 0.680"  # scripted group (container) (typed FeaturePython)
  n = 0.680449
FEATURE [App::DocumentObjectGroupPython] N_element033  label="N_element : 0.099"  # scripted group (container) (typed FeaturePython)
  n = 0.099189
FEATURE [App::DocumentObjectGroupPython] O_element073  label="O_element : 0.113"  # scripted group (container) (typed FeaturePython)
  n = 0.1133
FEATURE [App::DocumentObjectGroupPython] G4_NYLON_6_10  label="G4_NYLON-6-10"  # scripted group (container) (typed FeaturePython)
  Dunit = g/cm3
  Dvalue = 1.14
  Group = -> [H_element065,C_element071,N_element033,O_element073]
  conduct = 2
  density = 1
  expand = 3
  formula = G4_NYLON-6-10
  name = G4_NYLON-6-10
  specific = 4
FEATURE [App::DocumentObjectGroupPython] H_element066  label="H_element : 0.140"  # scripted group (container) (typed FeaturePython)
  n = 0.115476
FEATURE [App::DocumentObjectGroupPython] C_element072  label="C_element : 0.721"  # scripted group (container) (typed FeaturePython)
  n = 0.720818
FEATURE [App::DocumentObjectGroupPython] N_element034  label="N_element : 0.076"  # scripted group (container) (typed FeaturePython)
  n = 0.0764169
FEATURE [App::DocumentObjectGroupPython] O_element074  label="O_element : 0.087"  # scripted group (container) (typed FeaturePython)
  n = 0.0872889
FEATURE [App::DocumentObjectGroupPython] G4_NYLON_11_RILSAN  label="G4_NYLON-11_RILSAN"  # scripted group (container) (typed FeaturePython)
  Dunit = g/cm3
  Dvalue = 1.425
  Group = -> [H_element066,C_element072,N_element034,O_element074]
  conduct = 2
  density = 1
  expand = 3
  formula = G4_NYLON-11_RILSAN
  name = G4_NYLON-11_RILSAN
  specific = 4
FEATURE [App::DocumentObjectGroupPython] C_element073  label="C_element : 8"  # scripted group (container) (typed FeaturePython)
  n = 8
  ref = C_element
FEATURE [App::DocumentObjectGroupPython] H_element067  label="H_element : 18"  # scripted group (container) (typed FeaturePython)
  n = 18
  ref = H_element
FEATURE [App::DocumentObjectGroupPython] G4_OCTANE  # scripted group (container) (typed FeaturePython)
  Dunit = g/cm3
  Dvalue = 0.7026
  Group = -> [C_element073,H_element067]
  conduct = 2
  density = 1
  expand = 3
  formula = G4_OCTANE
  name = G4_OCTANE
  specific = 4
FEATURE [App::DocumentObjectGroupPython] C_element074  label="C_element : 25"  # scripted group (container) (typed FeaturePython)
  n = 25
  ref = C_element
FEATURE [App::DocumentObjectGroupPython] H_element068  label="H_element : 52"  # scripted group (container) (typed FeaturePython)
  n = 52
  ref = H_element
FEATURE [App::DocumentObjectGroupPython] G4_PARAFFIN  # scripted group (container) (typed FeaturePython)
  Dunit = g/cm3
  Dvalue = 0.93
  Group = -> [C_element074,H_element068]
  conduct = 2
  density = 1
  expand = 3
  formula = G4_PARAFFIN
  name = G4_PARAFFIN
  specific = 4
FEATURE [App::DocumentObjectGroupPython] C_element075  label="C_element : 036"  # scripted group (container) (typed FeaturePython)
  n = 5
  ref = C_element
FEATURE [App::DocumentObjectGroupPython] H_element069  label="H_element : 032"  # scripted group (container) (typed FeaturePython)
  n = 12
  ref = H_element
FEATURE [App::DocumentObjectGroupPython] G4_N_PENTANE  label="G4_N-PENTANE"  # scripted group (container) (typed FeaturePython)
  Dunit = g/cm3
  Dvalue = 0.6262
  Group = -> [C_element075,H_element069]
  conduct = 2
  density = 1
  expand = 3
  formula = G4_N-PENTANE
  name = G4_N-PENTANE
  specific = 4
FEATURE [App::DocumentObjectGroupPython] H_element070  label="H_element : 0.014"  # scripted group (container) (typed FeaturePython)
  n = 0.0141
FEATURE [App::DocumentObjectGroupPython] C_element076  label="C_element : 0.072"  # scripted group (container) (typed FeaturePython)
  n = 0.072261
FEATURE [App::DocumentObjectGroupPython] N_element035  label="N_element : 0.019"  # scripted group (container) (typed FeaturePython)
  n = 0.01932
FEATURE [App::DocumentObjectGroupPython] O_element075  label="O_element : 0.066"  # scripted group (container) (typed FeaturePython)
  n = 0.066101
FEATURE [App::DocumentObjectGroupPython] S_element019  label="S_element : 0.020"  # scripted group (container) (typed FeaturePython)
  n = 0.00189
FEATURE [App::DocumentObjectGroupPython] Br_element004  label="Br_element : 0.349"  # scripted group (container) (typed FeaturePython)
  n = 0.349103
FEATURE [App::DocumentObjectGroupPython] Ag_element001  label="Ag_element : 0.474"  # scripted group (container) (typed FeaturePython)
  n = 0.474105
FEATURE [App::DocumentObjectGroupPython] I_element005  label="I_element : 0.003"  # scripted group (container) (typed FeaturePython)
  n = 0.00312
FEATURE [App::DocumentObjectGroupPython] G4_PHOTO_EMULSION  # scripted group (container) (typed FeaturePython)
  Dunit = g/cm3
  Dvalue = 3.815
  Group = -> [H_element070,C_element076,N_element035,O_element075,S_element019,Br_element004,Ag_element001,I_element005]
  conduct = 2
  density = 1
  expand = 3
  formula = G4_PHOTO_EMULSION
  name = G4_PHOTO_EMULSION
  specific = 4
FEATURE [App::DocumentObjectGroupPython] C_element077  label="C_element : 9"  # scripted group (container) (typed FeaturePython)
  n = 9
  ref = C_element
FEATURE [App::DocumentObjectGroupPython] H_element071  label="H_element : 033"  # scripted group (container) (typed FeaturePython)
  n = 10
  ref = H_element
FEATURE [App::DocumentObjectGroupPython] G4_PLASTIC_SC_VINYLTOLUENE  # scripted group (container) (typed FeaturePython)
  Dunit = g/cm3
  Dvalue = 1.032
  Group = -> [C_element077,H_element071]
  conduct = 2
  density = 1
  expand = 3
  formula = G4_PLASTIC_SC_VINYLTOLUENE
  name = G4_PLASTIC_SC_VINYLTOLUENE
  specific = 4
FEATURE [App::DocumentObjectGroupPython] Pu_element001  label="Pu_element : 1"  # scripted group (container) (typed FeaturePython)
  n = 1
  ref = Pu_element
FEATURE [App::DocumentObjectGroupPython] O_element076  label="O_element : 037"  # scripted group (container) (typed FeaturePython)
  n = 2
  ref = O_element
FEATURE [App::DocumentObjectGroupPython] G4_PLUTONIUM_DIOXIDE  # scripted group (container) (typed FeaturePython)
  Dunit = g/cm3
  Dvalue = 11.46
  Group = -> [Pu_element001,O_element076]
  conduct = 2
  density = 1
  expand = 3
  formula = G4_PLUTONIUM_DIOXIDE
  name = G4_PLUTONIUM_DIOXIDE
  specific = 4
FEATURE [App::DocumentObjectGroupPython] C_element078  label="C_element : 037"  # scripted group (container) (typed FeaturePython)
  n = 3
  ref = C_element
FEATURE [App::DocumentObjectGroupPython] H_element072  label="H_element : 034"  # scripted group (container) (typed FeaturePython)
  n = 3
  ref = H_element
FEATURE [App::DocumentObjectGroupPython] N_element036  label="N_element : 015"  # scripted group (container) (typed FeaturePython)
  n = 1
  ref = N_element
FEATURE [App::DocumentObjectGroupPython] G4_POLYACRYLONITRILE  # scripted group (container) (typed FeaturePython)
  Dunit = g/cm3
  Dvalue = 1.17
  Group = -> [C_element078,H_element072,N_element036]
  conduct = 2
  density = 1
  expand = 3
  formula = G4_POLYACRYLONITRILE
  name = G4_POLYACRYLONITRILE
  specific = 4
FEATURE [App::DocumentObjectGroupPython] C_element079  label="C_element : 16"  # scripted group (container) (typed FeaturePython)
  n = 16
  ref = C_element
FEATURE [App::DocumentObjectGroupPython] H_element073  label="H_element : 035"  # scripted group (container) (typed FeaturePython)
  n = 14
  ref = H_element
FEATURE [App::DocumentObjectGroupPython] O_element077  label="O_element : 038"  # scripted group (container) (typed FeaturePython)
  n = 3
  ref = O_element
FEATURE [App::DocumentObjectGroupPython] G4_POLYCARBONATE  # scripted group (container) (typed FeaturePython)
  Dunit = g/cm3
  Dvalue = 1.2
  Group = -> [C_element079,H_element073,O_element077]
  conduct = 2
  density = 1
  expand = 3
  formula = G4_POLYCARBONATE
  name = G4_POLYCARBONATE
  specific = 4
FEATURE [App::DocumentObjectGroupPython] C_element080  label="C_element : 038"  # scripted group (container) (typed FeaturePython)
  n = 8
  ref = C_element
FEATURE [App::DocumentObjectGroupPython] H_element074  label="H_element : 036"  # scripted group (container) (typed FeaturePython)
  n = 7
  ref = H_element
FEATURE [App::DocumentObjectGroupPython] Cl_element017  label="Cl_element : 007"  # scripted group (container) (typed FeaturePython)
  n = 1
  ref = Cl_element
FEATURE [App::DocumentObjectGroupPython] G4_POLYCHLOROSTYRENE  # scripted group (container) (typed FeaturePython)
  Dunit = g/cm3
  Dvalue = 1.3
  Group = -> [C_element080,H_element074,Cl_element017]
  conduct = 2
  density = 1
  expand = 3
  formula = G4_POLYCHLOROSTYRENE
  name = G4_POLYCHLOROSTYRENE
  specific = 4
FEATURE [App::DocumentObjectGroupPython] C_element081  label="C_element : 039"  # scripted group (container) (typed FeaturePython)
  n = 1
  ref = C_element
FEATURE [App::DocumentObjectGroupPython] H_element075  label="H_element : 037"  # scripted group (container) (typed FeaturePython)
  n = 2
  ref = H_element
FEATURE [App::DocumentObjectGroupPython] G4_POLYETHYLENE  # scripted group (container) (typed FeaturePython)
  Dunit = g/cm3
  Dvalue = 0.94
  Group = -> [C_element081,H_element075]
  conduct = 2
  density = 1
  expand = 3
  formula = G4_POLYETHYLENE
  name = G4_POLYETHYLENE
  specific = 4
FEATURE [App::DocumentObjectGroupPython] C_element082  label="C_element : 040"  # scripted group (container) (typed FeaturePython)
  n = 10
  ref = C_element
FEATURE [App::DocumentObjectGroupPython] H_element076  label="H_element : 038"  # scripted group (container) (typed FeaturePython)
  n = 8
  ref = H_element
FEATURE [App::DocumentObjectGroupPython] O_element078  label="O_element : 039"  # scripted group (container) (typed FeaturePython)
  n = 4
  ref = O_element
FEATURE [App::DocumentObjectGroupPython] G4_MYLAR  # scripted group (container) (typed FeaturePython)
  Dunit = g/cm3
  Dvalue = 1.4
  Group = -> [C_element082,H_element076,O_element078]
  conduct = 2
  density = 1
  expand = 3
  formula = G4_MYLAR
  name = G4_MYLAR
  specific = 4
FEATURE [App::DocumentObjectGroupPython] C_element083  label="C_element : 041"  # scripted group (container) (typed FeaturePython)
  n = 5
  ref = C_element
FEATURE [App::DocumentObjectGroupPython] H_element077  label="H_element : 039"  # scripted group (container) (typed FeaturePython)
  n = 8
  ref = H_element
FEATURE [App::DocumentObjectGroupPython] O_element079  label="O_element : 040"  # scripted group (container) (typed FeaturePython)
  n = 2
  ref = O_element
FEATURE [App::DocumentObjectGroupPython] G4_PLEXIGLASS  # scripted group (container) (typed FeaturePython)
  Dunit = g/cm3
  Dvalue = 1.19
  Group = -> [C_element083,H_element077,O_element079]
  conduct = 2
  density = 1
  expand = 3
  formula = G4_PLEXIGLASS
  name = G4_PLEXIGLASS
  specific = 4
FEATURE [App::DocumentObjectGroupPython] C_element084  label="C_element : 042"  # scripted group (container) (typed FeaturePython)
  n = 1
  ref = C_element
FEATURE [App::DocumentObjectGroupPython] H_element078  label="H_element : 040"  # scripted group (container) (typed FeaturePython)
  n = 2
  ref = H_element
FEATURE [App::DocumentObjectGroupPython] O_element080  label="O_element : 041"  # scripted group (container) (typed FeaturePython)
  n = 1
  ref = O_element
FEATURE [App::DocumentObjectGroupPython] G4_POLYOXYMETHYLENE  # scripted group (container) (typed FeaturePython)
  Dunit = g/cm3
  Dvalue = 1.425
  Group = -> [C_element084,H_element078,O_element080]
  conduct = 2
  density = 1
  expand = 3
  formula = G4_POLYOXYMETHYLENE
  name = G4_POLYOXYMETHYLENE
  specific = 4
FEATURE [App::DocumentObjectGroupPython] C_element085  label="C_element : 043"  # scripted group (container) (typed FeaturePython)
  n = 2
  ref = C_element
FEATURE [App::DocumentObjectGroupPython] H_element079  label="H_element : 041"  # scripted group (container) (typed FeaturePython)
  n = 4
  ref = H_element
FEATURE [App::DocumentObjectGroupPython] G4_POLYPROPYLENE  # scripted group (container) (typed FeaturePython)
  Dunit = g/cm3
  Dvalue = 0.9
  Group = -> [C_element085,H_element079]
  conduct = 2
  density = 1
  expand = 3
  formula = G4_POLYPROPYLENE
  name = G4_POLYPROPYLENE
  specific = 4
FEATURE [App::DocumentObjectGroupPython] C_element086  label="C_element : 044"  # scripted group (container) (typed FeaturePython)
  n = 8
  ref = C_element
FEATURE [App::DocumentObjectGroupPython] H_element080  label="H_element : 042"  # scripted group (container) (typed FeaturePython)
  n = 8
  ref = H_element
FEATURE [App::DocumentObjectGroupPython] G4_POLYSTYRENE  # scripted group (container) (typed FeaturePython)
  Dunit = g/cm3
  Dvalue = 1.06
  Group = -> [C_element086,H_element080]
  conduct = 2
  density = 1
  expand = 3
  formula = G4_POLYSTYRENE
  name = G4_POLYSTYRENE
  specific = 4
FEATURE [App::DocumentObjectGroupPython] C_element087  label="C_element : 045"  # scripted group (container) (typed FeaturePython)
  n = 2
  ref = C_element
FEATURE [App::DocumentObjectGroupPython] F_element014  label="F_element : 4"  # scripted group (container) (typed FeaturePython)
  n = 4
  ref = F_element
FEATURE [App::DocumentObjectGroupPython] G4_TEFLON  # scripted group (container) (typed FeaturePython)
  Dunit = g/cm3
  Dvalue = 2.2
  Group = -> [C_element087,F_element014]
  conduct = 2
  density = 1
  expand = 3
  formula = G4_TEFLON
  name = G4_TEFLON
  specific = 4
FEATURE [App::DocumentObjectGroupPython] C_element088  label="C_element : 046"  # scripted group (container) (typed FeaturePython)
  n = 2
  ref = C_element
FEATURE [App::DocumentObjectGroupPython] F_element015  label="F_element : 006"  # scripted group (container) (typed FeaturePython)
  n = 3
  ref = F_element
FEATURE [App::DocumentObjectGroupPython] Cl_element018  label="Cl_element : 008"  # scripted group (container) (typed FeaturePython)
  n = 1
  ref = Cl_element
FEATURE [App::DocumentObjectGroupPython] G4_POLYTRIFLUOROCHLOROETHYLENE  # scripted group (container) (typed FeaturePython)
  Dunit = g/cm3
  Dvalue = 2.1
  Group = -> [C_element088,F_element015,Cl_element018]
  conduct = 2
  density = 1
  expand = 3
  formula = G4_POLYTRIFLUOROCHLOROETHYLENE
  name = G4_POLYTRIFLUOROCHLOROETHYLENE
  specific = 4
FEATURE [App::DocumentObjectGroupPython] C_element089  label="C_element : 047"  # scripted group (container) (typed FeaturePython)
  n = 4
  ref = C_element
FEATURE [App::DocumentObjectGroupPython] H_element081  label="H_element : 043"  # scripted group (container) (typed FeaturePython)
  n = 6
  ref = H_element
FEATURE [App::DocumentObjectGroupPython] O_element081  label="O_element : 042"  # scripted group (container) (typed FeaturePython)
  n = 2
  ref = O_element
FEATURE [App::DocumentObjectGroupPython] G4_POLYVINYL_ACETATE  # scripted group (container) (typed FeaturePython)
  Dunit = g/cm3
  Dvalue = 1.19
  Group = -> [C_element089,H_element081,O_element081]
  conduct = 2
  density = 1
  expand = 3
  formula = G4_POLYVINYL_ACETATE
  name = G4_POLYVINYL_ACETATE
  specific = 4
FEATURE [App::DocumentObjectGroupPython] C_element090  label="C_element : 048"  # scripted group (container) (typed FeaturePython)
  n = 2
  ref = C_element
FEATURE [App::DocumentObjectGroupPython] H_element082  label="H_element : 044"  # scripted group (container) (typed FeaturePython)
  n = 4
  ref = H_element
FEATURE [App::DocumentObjectGroupPython] O_element082  label="O_element : 043"  # scripted group (container) (typed FeaturePython)
  n = 1
  ref = O_element
FEATURE [App::DocumentObjectGroupPython] G4_POLYVINYL_ALCOHOL  # scripted group (container) (typed FeaturePython)
  Dunit = g/cm3
  Dvalue = 1.3
  Group = -> [C_element090,H_element082,O_element082]
  conduct = 2
  density = 1
  expand = 3
  formula = G4_POLYVINYL_ALCOHOL
  name = G4_POLYVINYL_ALCOHOL
  specific = 4
FEATURE [App::DocumentObjectGroupPython] C_element091  label="C_element : 049"  # scripted group (container) (typed FeaturePython)
  n = 8
  ref = C_element
FEATURE [App::DocumentObjectGroupPython] H_element083  label="H_element : 045"  # scripted group (container) (typed FeaturePython)
  n = 14
  ref = H_element
FEATURE [App::DocumentObjectGroupPython] O_element083  label="O_element : 044"  # scripted group (container) (typed FeaturePython)
  n = 2
  ref = O_element
FEATURE [App::DocumentObjectGroupPython] G4_POLYVINYL_BUTYRAL  # scripted group (container) (typed FeaturePython)
  Dunit = g/cm3
  Dvalue = 1.12
  Group = -> [C_element091,H_element083,O_element083]
  conduct = 2
  density = 1
  expand = 3
  formula = G4_POLYVINYL_BUTYRAL
  name = G4_POLYVINYL_BUTYRAL
  specific = 4
FEATURE [App::DocumentObjectGroupPython] C_element092  label="C_element : 050"  # scripted group (container) (typed FeaturePython)
  n = 2
  ref = C_element
FEATURE [App::DocumentObjectGroupPython] H_element084  label="H_element : 046"  # scripted group (container) (typed FeaturePython)
  n = 3
  ref = H_element
FEATURE [App::DocumentObjectGroupPython] Cl_element019  label="Cl_element : 009"  # scripted group (container) (typed FeaturePython)
  n = 1
  ref = Cl_element
FEATURE [App::DocumentObjectGroupPython] G4_POLYVINYL_CHLORIDE  # scripted group (container) (typed FeaturePython)
  Dunit = g/cm3
  Dvalue = 1.3
  Group = -> [C_element092,H_element084,Cl_element019]
  conduct = 2
  density = 1
  expand = 3
  formula = G4_POLYVINYL_CHLORIDE
  name = G4_POLYVINYL_CHLORIDE
  specific = 4
FEATURE [App::DocumentObjectGroupPython] C_element093  label="C_element : 051"  # scripted group (container) (typed FeaturePython)
  n = 2
  ref = C_element
FEATURE [App::DocumentObjectGroupPython] H_element085  label="H_element : 047"  # scripted group (container) (typed FeaturePython)
  n = 2
  ref = H_element
FEATURE [App::DocumentObjectGroupPython] Cl_element020  label="Cl_element : 010"  # scripted group (container) (typed FeaturePython)
  n = 2
  ref = Cl_element
FEATURE [App::DocumentObjectGroupPython] G4_POLYVINYLIDENE_CHLORIDE  # scripted group (container) (typed FeaturePython)
  Dunit = g/cm3
  Dvalue = 1.7
  Group = -> [C_element093,H_element085,Cl_element020]
  conduct = 2
  density = 1
  expand = 3
  formula = G4_POLYVINYLIDENE_CHLORIDE
  name = G4_POLYVINYLIDENE_CHLORIDE
  specific = 4
FEATURE [App::DocumentObjectGroupPython] C_element094  label="C_element : 052"  # scripted group (container) (typed FeaturePython)
  n = 2
  ref = C_element
FEATURE [App::DocumentObjectGroupPython] H_element086  label="H_element : 048"  # scripted group (container) (typed FeaturePython)
  n = 2
  ref = H_element
FEATURE [App::DocumentObjectGroupPython] F_element016  label="F_element : 007"  # scripted group (container) (typed FeaturePython)
  n = 2
  ref = F_element
FEATURE [App::DocumentObjectGroupPython] G4_POLYVINYLIDENE_FLUORIDE  # scripted group (container) (typed FeaturePython)
  Dunit = g/cm3
  Dvalue = 1.76
  Group = -> [C_element094,H_element086,F_element016]
  conduct = 2
  density = 1
  expand = 3
  formula = G4_POLYVINYLIDENE_FLUORIDE
  name = G4_POLYVINYLIDENE_FLUORIDE
  specific = 4
FEATURE [App::DocumentObjectGroupPython] C_element095  label="C_element : 053"  # scripted group (container) (typed FeaturePython)
  n = 6
  ref = C_element
FEATURE [App::DocumentObjectGroupPython] H_element087  label="H_element : 9"  # scripted group (container) (typed FeaturePython)
  n = 9
  ref = H_element
FEATURE [App::DocumentObjectGroupPython] N_element037  label="N_element : 016"  # scripted group (container) (typed FeaturePython)
  n = 1
  ref = N_element
FEATURE [App::DocumentObjectGroupPython] O_element084  label="O_element : 045"  # scripted group (container) (typed FeaturePython)
  n = 1
  ref = O_element
FEATURE [App::DocumentObjectGroupPython] G4_POLYVINYL_PYRROLIDONE  # scripted group (container) (typed FeaturePython)
  Dunit = g/cm3
  Dvalue = 1.25
  Group = -> [C_element095,H_element087,N_element037,O_element084]
  conduct = 2
  density = 1
  expand = 3
  formula = G4_POLYVINYL_PYRROLIDONE
  name = G4_POLYVINYL_PYRROLIDONE
  specific = 4
FEATURE [App::DocumentObjectGroupPython] K_element008  label="K_element : 1"  # scripted group (container) (typed FeaturePython)
  n = 1
  ref = K_element
FEATURE [App::DocumentObjectGroupPython] I_element006  label="I_element : 003"  # scripted group (container) (typed FeaturePython)
  n = 1
  ref = I_element
FEATURE [App::DocumentObjectGroupPython] G4_POTASSIUM_IODIDE  # scripted group (container) (typed FeaturePython)
  Dunit = g/cm3
  Dvalue = 3.13
  Group = -> [K_element008,I_element006]
  conduct = 2
  density = 1
  expand = 3
  formula = G4_POTASSIUM_IODIDE
  name = G4_POTASSIUM_IODIDE
  specific = 4
FEATURE [App::DocumentObjectGroupPython] K_element009  label="K_element : 2"  # scripted group (container) (typed FeaturePython)
  n = 2
  ref = K_element
FEATURE [App::DocumentObjectGroupPython] O_element085  label="O_element : 046"  # scripted group (container) (typed FeaturePython)
  n = 1
  ref = O_element
FEATURE [App::DocumentObjectGroupPython] G4_POTASSIUM_OXIDE  # scripted group (container) (typed FeaturePython)
  Dunit = g/cm3
  Dvalue = 2.32
  Group = -> [K_element009,O_element085]
  conduct = 2
  density = 1
  expand = 3
  formula = G4_POTASSIUM_OXIDE
  name = G4_POTASSIUM_OXIDE
  specific = 4
FEATURE [App::DocumentObjectGroupPython] C_element096  label="C_element : 054"  # scripted group (container) (typed FeaturePython)
  n = 3
  ref = C_element
FEATURE [App::DocumentObjectGroupPython] H_element088  label="H_element : 049"  # scripted group (container) (typed FeaturePython)
  n = 8
  ref = H_element
FEATURE [App::DocumentObjectGroupPython] G4_PROPANE  # scripted group (container) (typed FeaturePython)
  Dunit = g/cm3
  Dvalue = 0.00187939
  Group = -> [C_element096,H_element088]
  conduct = 2
  density = 1
  expand = 3
  formula = G4_PROPANE
  name = G4_PROPANE
  specific = 4
FEATURE [App::DocumentObjectGroupPython] C_element097  label="C_element : 055"  # scripted group (container) (typed FeaturePython)
  n = 3
  ref = C_element
FEATURE [App::DocumentObjectGroupPython] H_element089  label="H_element : 050"  # scripted group (container) (typed FeaturePython)
  n = 8
  ref = H_element
FEATURE [App::DocumentObjectGroupPython] G4_lPROPANE  # scripted group (container) (typed FeaturePython)
  Dunit = g/cm3
  Dvalue = 0.43
  Group = -> [C_element097,H_element089]
  conduct = 2
  density = 1
  expand = 3
  formula = G4_lPROPANE
  name = G4_lPROPANE
  specific = 4
FEATURE [App::DocumentObjectGroupPython] C_element098  label="C_element : 056"  # scripted group (container) (typed FeaturePython)
  n = 3
  ref = C_element
FEATURE [App::DocumentObjectGroupPython] H_element090  label="H_element : 051"  # scripted group (container) (typed FeaturePython)
  n = 8
  ref = H_element
FEATURE [App::DocumentObjectGroupPython] O_element086  label="O_element : 047"  # scripted group (container) (typed FeaturePython)
  n = 1
  ref = O_element
FEATURE [App::DocumentObjectGroupPython] G4_N_PROPYL_ALCOHOL  label="G4_N-PROPYL_ALCOHOL"  # scripted group (container) (typed FeaturePython)
  Dunit = g/cm3
  Dvalue = 0.8035
  Group = -> [C_element098,H_element090,O_element086]
  conduct = 2
  density = 1
  expand = 3
  formula = G4_N-PROPYL_ALCOHOL
  name = G4_N-PROPYL_ALCOHOL
  specific = 4
FEATURE [App::DocumentObjectGroupPython] C_element099  label="C_element : 057"  # scripted group (container) (typed FeaturePython)
  n = 5
  ref = C_element
FEATURE [App::DocumentObjectGroupPython] H_element091  label="H_element : 052"  # scripted group (container) (typed FeaturePython)
  n = 5
  ref = H_element
FEATURE [App::DocumentObjectGroupPython] N_element038  label="N_element : 017"  # scripted group (container) (typed FeaturePython)
  n = 1
  ref = N_element
FEATURE [App::DocumentObjectGroupPython] G4_PYRIDINE  # scripted group (container) (typed FeaturePython)
  Dunit = g/cm3
  Dvalue = 0.9819
  Group = -> [C_element099,H_element091,N_element038]
  conduct = 2
  density = 1
  expand = 3
  formula = G4_PYRIDINE
  name = G4_PYRIDINE
  specific = 4
FEATURE [App::DocumentObjectGroupPython] H_element092  label="H_element : 0.144"  # scripted group (container) (typed FeaturePython)
  n = 0.143711
FEATURE [App::DocumentObjectGroupPython] C_element100  label="C_element : 0.856"  # scripted group (container) (typed FeaturePython)
  n = 0.856289
FEATURE [App::DocumentObjectGroupPython] G4_RUBBER_BUTYL  # scripted group (container) (typed FeaturePython)
  Dunit = g/cm3
  Dvalue = 0.92
  Group = -> [H_element092,C_element100]
  conduct = 2
  density = 1
  expand = 3
  formula = G4_RUBBER_BUTYL
  name = G4_RUBBER_BUTYL
  specific = 4
FEATURE [App::DocumentObjectGroupPython] H_element093  label="H_element : 0.118"  # scripted group (container) (typed FeaturePython)
  n = 0.118371
FEATURE [App::DocumentObjectGroupPython] C_element101  label="C_element : 0.882"  # scripted group (container) (typed FeaturePython)
  n = 0.881629
FEATURE [App::DocumentObjectGroupPython] G4_RUBBER_NATURAL  # scripted group (container) (typed FeaturePython)
  Dunit = g/cm3
  Dvalue = 0.92
  Group = -> [H_element093,C_element101]
  conduct = 2
  density = 1
  expand = 3
  formula = G4_RUBBER_NATURAL
  name = G4_RUBBER_NATURAL
  specific = 4
FEATURE [App::DocumentObjectGroupPython] H_element094  label="H_element : 0.145"  # scripted group (container) (typed FeaturePython)
  n = 0.05692
FEATURE [App::DocumentObjectGroupPython] C_element102  label="C_element : 0.543"  # scripted group (container) (typed FeaturePython)
  n = 0.542646
FEATURE [App::DocumentObjectGroupPython] Cl_element021  label="Cl_element : 0.400"  # scripted group (container) (typed FeaturePython)
  n = 0.400434
FEATURE [App::DocumentObjectGroupPython] G4_RUBBER_NEOPRENE  # scripted group (container) (typed FeaturePython)
  Dunit = g/cm3
  Dvalue = 1.23
  Group = -> [H_element094,C_element102,Cl_element021]
  conduct = 2
  density = 1
  expand = 3
  formula = G4_RUBBER_NEOPRENE
  name = G4_RUBBER_NEOPRENE
  specific = 4
FEATURE [App::DocumentObjectGroupPython] Si_element006  label="Si_element : 1"  # scripted group (container) (typed FeaturePython)
  n = 1
  ref = Si_element
FEATURE [App::DocumentObjectGroupPython] O_element087  label="O_element : 048"  # scripted group (container) (typed FeaturePython)
  n = 2
  ref = O_element
FEATURE [App::DocumentObjectGroupPython] G4_SILICON_DIOXIDE  # scripted group (container) (typed FeaturePython)
  Dunit = g/cm3
  Dvalue = 2.32
  Group = -> [Si_element006,O_element087]
  conduct = 2
  density = 1
  expand = 3
  formula = G4_SILICON_DIOXIDE
  name = G4_SILICON_DIOXIDE
  specific = 4
FEATURE [App::DocumentObjectGroupPython] Ag_element002  label="Ag_element : 1"  # scripted group (container) (typed FeaturePython)
  n = 1
  ref = Ag_element
FEATURE [App::DocumentObjectGroupPython] Br_element005  label="Br_element : 003"  # scripted group (container) (typed FeaturePython)
  n = 1
  ref = Br_element
FEATURE [App::DocumentObjectGroupPython] G4_SILVER_BROMIDE  # scripted group (container) (typed FeaturePython)
  Dunit = g/cm3
  Dvalue = 6.473
  Group = -> [Ag_element002,Br_element005]
  conduct = 2
  density = 1
  expand = 3
  formula = G4_SILVER_BROMIDE
  name = G4_SILVER_BROMIDE
  specific = 4
FEATURE [App::DocumentObjectGroupPython] Ag_element003  label="Ag_element : 002"  # scripted group (container) (typed FeaturePython)
  n = 1
  ref = Ag_element
FEATURE [App::DocumentObjectGroupPython] Cl_element022  label="Cl_element : 011"  # scripted group (container) (typed FeaturePython)
  n = 1
  ref = Cl_element
FEATURE [App::DocumentObjectGroupPython] G4_SILVER_CHLORIDE  # scripted group (container) (typed FeaturePython)
  Dunit = g/cm3
  Dvalue = 5.56
  Group = -> [Ag_element003,Cl_element022]
  conduct = 2
  density = 1
  expand = 3
  formula = G4_SILVER_CHLORIDE
  name = G4_SILVER_CHLORIDE
  specific = 4
FEATURE [App::DocumentObjectGroupPython] Br_element006  label="Br_element : 0.423"  # scripted group (container) (typed FeaturePython)
  n = 0.422895
FEATURE [App::DocumentObjectGroupPython] Ag_element004  label="Ag_element : 0.574"  # scripted group (container) (typed FeaturePython)
  n = 0.573748
FEATURE [App::DocumentObjectGroupPython] I_element007  label="I_element : 0.649"  # scripted group (container) (typed FeaturePython)
  n = 0.003357
FEATURE [App::DocumentObjectGroupPython] G4_SILVER_HALIDES  # scripted group (container) (typed FeaturePython)
  Dunit = g/cm3
  Dvalue = 6.47
  Group = -> [Br_element006,Ag_element004,I_element007]
  conduct = 2
  density = 1
  expand = 3
  formula = G4_SILVER_HALIDES
  name = G4_SILVER_HALIDES
  specific = 4
FEATURE [App::DocumentObjectGroupPython] Ag_element005  label="Ag_element : 003"  # scripted group (container) (typed FeaturePython)
  n = 1
  ref = Ag_element
FEATURE [App::DocumentObjectGroupPython] I_element008  label="I_element : 004"  # scripted group (container) (typed FeaturePython)
  n = 1
  ref = I_element
FEATURE [App::DocumentObjectGroupPython] G4_SILVER_IODIDE  # scripted group (container) (typed FeaturePython)
  Dunit = g/cm3
  Dvalue = 6.01
  Group = -> [Ag_element005,I_element008]
  conduct = 2
  density = 1
  expand = 3
  formula = G4_SILVER_IODIDE
  name = G4_SILVER_IODIDE
  specific = 4
FEATURE [App::DocumentObjectGroupPython] H_element095  label="H_element : 0.100"  # scripted group (container) (typed FeaturePython)
  n = 0.1
FEATURE [App::DocumentObjectGroupPython] C_element103  label="C_element : 0.204"  # scripted group (container) (typed FeaturePython)
  n = 0.204
FEATURE [App::DocumentObjectGroupPython] N_element039  label="N_element : 0.759"  # scripted group (container) (typed FeaturePython)
  n = 0.042
FEATURE [App::DocumentObjectGroupPython] O_element088  label="O_element : 0.645"  # scripted group (container) (typed FeaturePython)
  n = 0.645
FEATURE [App::DocumentObjectGroupPython] Na_element013  label="Na_element : 0.100"  # scripted group (container) (typed FeaturePython)
  n = 0.002
FEATURE [App::DocumentObjectGroupPython] P_element009  label="P_element : 0.107"  # scripted group (container) (typed FeaturePython)
  n = 0.001
FEATURE [App::DocumentObjectGroupPython] S_element020  label="S_element : 0.021"  # scripted group (container) (typed FeaturePython)
  n = 0.002
FEATURE [App::DocumentObjectGroupPython] Cl_element023  label="Cl_element : 0.590"  # scripted group (container) (typed FeaturePython)
  n = 0.003
FEATURE [App::DocumentObjectGroupPython] K_element010  label="K_element : 0.001"  # scripted group (container) (typed FeaturePython)
  n = 0.001
FEATURE [App::DocumentObjectGroupPython] G4_SKIN_ICRP  # scripted group (container) (typed FeaturePython)
  Dunit = g/cm3
  Dvalue = 1.09
  Group = -> [H_element095,C_element103,N_element039,O_element088,Na_element013,P_element009,S_element020,Cl_element023,K_element010]
  conduct = 2
  density = 1
  expand = 3
  formula = G4_SKIN_ICRP
  name = G4_SKIN_ICRP
  specific = 4
FEATURE [App::DocumentObjectGroupPython] Na_element014  label="Na_element : 2"  # scripted group (container) (typed FeaturePython)
  n = 2
  ref = Na_element
FEATURE [App::DocumentObjectGroupPython] C_element104  label="C_element : 058"  # scripted group (container) (typed FeaturePython)
  n = 1
  ref = C_element
FEATURE [App::DocumentObjectGroupPython] O_element089  label="O_element : 049"  # scripted group (container) (typed FeaturePython)
  n = 3
  ref = O_element
FEATURE [App::DocumentObjectGroupPython] G4_SODIUM_CARBONATE  # scripted group (container) (typed FeaturePython)
  Dunit = g/cm3
  Dvalue = 2.532
  Group = -> [Na_element014,C_element104,O_element089]
  conduct = 2
  density = 1
  expand = 3
  formula = G4_SODIUM_CARBONATE
  name = G4_SODIUM_CARBONATE
  specific = 4
FEATURE [App::DocumentObjectGroupPython] Na_element015  label="Na_element : 1"  # scripted group (container) (typed FeaturePython)
  n = 1
  ref = Na_element
FEATURE [App::DocumentObjectGroupPython] I_element009  label="I_element : 005"  # scripted group (container) (typed FeaturePython)
  n = 1
  ref = I_element
FEATURE [App::DocumentObjectGroupPython] G4_SODIUM_IODIDE  # scripted group (container) (typed FeaturePython)
  Dunit = g/cm3
  Dvalue = 3.667
  Group = -> [Na_element015,I_element009]
  conduct = 2
  density = 1
  expand = 3
  formula = G4_SODIUM_IODIDE
  name = G4_SODIUM_IODIDE
  specific = 4
FEATURE [App::DocumentObjectGroupPython] Na_element016  label="Na_element : 003"  # scripted group (container) (typed FeaturePython)
  n = 2
  ref = Na_element
FEATURE [App::DocumentObjectGroupPython] O_element090  label="O_element : 050"  # scripted group (container) (typed FeaturePython)
  n = 1
  ref = O_element
FEATURE [App::DocumentObjectGroupPython] G4_SODIUM_MONOXIDE  # scripted group (container) (typed FeaturePython)
  Dunit = g/cm3
  Dvalue = 2.27
  Group = -> [Na_element016,O_element090]
  conduct = 2
  density = 1
  expand = 3
  formula = G4_SODIUM_MONOXIDE
  name = G4_SODIUM_MONOXIDE
  specific = 4
FEATURE [App::DocumentObjectGroupPython] Na_element017  label="Na_element : 004"  # scripted group (container) (typed FeaturePython)
  n = 1
  ref = Na_element
FEATURE [App::DocumentObjectGroupPython] N_element040  label="N_element : 018"  # scripted group (container) (typed FeaturePython)
  n = 1
  ref = N_element
FEATURE [App::DocumentObjectGroupPython] O_element091  label="O_element : 051"  # scripted group (container) (typed FeaturePython)
  n = 3
  ref = O_element
FEATURE [App::DocumentObjectGroupPython] G4_SODIUM_NITRATE  # scripted group (container) (typed FeaturePython)
  Dunit = g/cm3
  Dvalue = 2.261
  Group = -> [Na_element017,N_element040,O_element091]
  conduct = 2
  density = 1
  expand = 3
  formula = G4_SODIUM_NITRATE
  name = G4_SODIUM_NITRATE
  specific = 4
FEATURE [App::DocumentObjectGroupPython] C_element105  label="C_element : 059"  # scripted group (container) (typed FeaturePython)
  n = 14
  ref = C_element
FEATURE [App::DocumentObjectGroupPython] H_element096  label="H_element : 053"  # scripted group (container) (typed FeaturePython)
  n = 12
  ref = H_element
FEATURE [App::DocumentObjectGroupPython] G4_STILBENE  # scripted group (container) (typed FeaturePython)
  Dunit = g/cm3
  Dvalue = 0.9707
  Group = -> [C_element105,H_element096]
  conduct = 2
  density = 1
  expand = 3
  formula = G4_STILBENE
  name = G4_STILBENE
  specific = 4
FEATURE [App::DocumentObjectGroupPython] C_element106  label="C_element : 12"  # scripted group (container) (typed FeaturePython)
  n = 12
  ref = C_element
FEATURE [App::DocumentObjectGroupPython] H_element097  label="H_element : 22"  # scripted group (container) (typed FeaturePython)
  n = 22
  ref = H_element
FEATURE [App::DocumentObjectGroupPython] O_element092  label="O_element : 11"  # scripted group (container) (typed FeaturePython)
  n = 11
  ref = O_element
FEATURE [App::DocumentObjectGroupPython] G4_SUCROSE  # scripted group (container) (typed FeaturePython)
  Dunit = g/cm3
  Dvalue = 1.5805
  Group = -> [C_element106,H_element097,O_element092]
  conduct = 2
  density = 1
  expand = 3
  formula = G4_SUCROSE
  name = G4_SUCROSE
  specific = 4
FEATURE [App::DocumentObjectGroupPython] C_element107  label="C_element : 18"  # scripted group (container) (typed FeaturePython)
  n = 18
  ref = C_element
FEATURE [App::DocumentObjectGroupPython] H_element098  label="H_element : 054"  # scripted group (container) (typed FeaturePython)
  n = 14
  ref = H_element
FEATURE [App::DocumentObjectGroupPython] G4_TERPHENYL  # scripted group (container) (typed FeaturePython)
  Dunit = g/cm3
  Dvalue = 1.24
  Group = -> [C_element107,H_element098]
  conduct = 2
  density = 1
  expand = 3
  formula = G4_TERPHENYL
  name = G4_TERPHENYL
  specific = 4
FEATURE [App::DocumentObjectGroupPython] H_element099  label="H_element : 0.146"  # scripted group (container) (typed FeaturePython)
  n = 0.106
FEATURE [App::DocumentObjectGroupPython] C_element108  label="C_element : 0.883"  # scripted group (container) (typed FeaturePython)
  n = 0.099
FEATURE [App::DocumentObjectGroupPython] N_element041  label="N_element : 0.020"  # scripted group (container) (typed FeaturePython)
  n = 0.02
FEATURE [App::DocumentObjectGroupPython] O_element093  label="O_element : 0.766"  # scripted group (container) (typed FeaturePython)
  n = 0.766
FEATURE [App::DocumentObjectGroupPython] Na_element018  label="Na_element : 0.101"  # scripted group (container) (typed FeaturePython)
  n = 0.002
FEATURE [App::DocumentObjectGroupPython] P_element010  label="P_element : 0.108"  # scripted group (container) (typed FeaturePython)
  n = 0.001
FEATURE [App::DocumentObjectGroupPython] S_element021  label="S_element : 0.022"  # scripted group (container) (typed FeaturePython)
  n = 0.002
FEATURE [App::DocumentObjectGroupPython] Cl_element024  label="Cl_element : 0.002"  # scripted group (container) (typed FeaturePython)
  n = 0.002
FEATURE [App::DocumentObjectGroupPython] K_element011  label="K_element : 0.017"  # scripted group (container) (typed FeaturePython)
  n = 0.002
FEATURE [App::DocumentObjectGroupPython] G4_TESTIS_ICRP  # scripted group (container) (typed FeaturePython)
  Dunit = g/cm3
  Dvalue = 1.04
  Group = -> [H_element099,C_element108,N_element041,O_element093,Na_element018,P_element010,S_element021,Cl_element024,K_element011]
  conduct = 2
  density = 1
  expand = 3
  formula = G4_TESTIS_ICRP
  name = G4_TESTIS_ICRP
  specific = 4
FEATURE [App::DocumentObjectGroupPython] C_element109  label="C_element : 060"  # scripted group (container) (typed FeaturePython)
  n = 2
  ref = C_element
FEATURE [App::DocumentObjectGroupPython] Cl_element025  label="Cl_element : 012"  # scripted group (container) (typed FeaturePython)
  n = 4
  ref = Cl_element
FEATURE [App::DocumentObjectGroupPython] G4_TETRACHLOROETHYLENE  # scripted group (container) (typed FeaturePython)
  Dunit = g/cm3
  Dvalue = 1.625
  Group = -> [C_element109,Cl_element025]
  conduct = 2
  density = 1
  expand = 3
  formula = G4_TETRACHLOROETHYLENE
  name = G4_TETRACHLOROETHYLENE
  specific = 4
FEATURE [App::DocumentObjectGroupPython] Tl_element001  label="Tl_element : 1"  # scripted group (container) (typed FeaturePython)
  n = 1
  ref = Tl_element
FEATURE [App::DocumentObjectGroupPython] Cl_element026  label="Cl_element : 013"  # scripted group (container) (typed FeaturePython)
  n = 1
  ref = Cl_element
FEATURE [App::DocumentObjectGroupPython] G4_THALLIUM_CHLORIDE  # scripted group (container) (typed FeaturePython)
  Dunit = g/cm3
  Dvalue = 7.004
  Group = -> [Tl_element001,Cl_element026]
  conduct = 2
  density = 1
  expand = 3
  formula = G4_THALLIUM_CHLORIDE
  name = G4_THALLIUM_CHLORIDE
  specific = 4
FEATURE [App::DocumentObjectGroupPython] H_element100  label="H_element : 0.147"  # scripted group (container) (typed FeaturePython)
  n = 0.105
FEATURE [App::DocumentObjectGroupPython] C_element110  label="C_element : 0.256"  # scripted group (container) (typed FeaturePython)
  n = 0.256
FEATURE [App::DocumentObjectGroupPython] N_element042  label="N_element : 0.760"  # scripted group (container) (typed FeaturePython)
  n = 0.027
FEATURE [App::DocumentObjectGroupPython] O_element094  label="O_element : 0.602"  # scripted group (container) (typed FeaturePython)
  n = 0.602
FEATURE [App::DocumentObjectGroupPython] Na_element019  label="Na_element : 0.102"  # scripted group (container) (typed FeaturePython)
  n = 0.001
FEATURE [App::DocumentObjectGroupPython] P_element011  label="P_element : 0.109"  # scripted group (container) (typed FeaturePython)
  n = 0.002
FEATURE [App::DocumentObjectGroupPython] S_element022  label="S_element : 0.023"  # scripted group (container) (typed FeaturePython)
  n = 0.003
FEATURE [App::DocumentObjectGroupPython] Cl_element027  label="Cl_element : 0.591"  # scripted group (container) (typed FeaturePython)
  n = 0.002
FEATURE [App::DocumentObjectGroupPython] K_element012  label="K_element : 0.018"  # scripted group (container) (typed FeaturePython)
  n = 0.002
FEATURE [App::DocumentObjectGroupPython] G4_TISSUE_SOFT_ICRP  # scripted group (container) (typed FeaturePython)
  Dunit = g/cm3
  Dvalue = 1.03
  Group = -> [H_element100,C_element110,N_element042,O_element094,Na_element019,P_element011,S_element022,Cl_element027,K_element012]
  conduct = 2
  density = 1
  expand = 3
  formula = G4_TISSUE_SOFT_ICRP
  name = G4_TISSUE_SOFT_ICRP
  specific = 4
FEATURE [App::DocumentObjectGroupPython] H_element101  label="H_element : 0.148"  # scripted group (container) (typed FeaturePython)
  n = 0.101
FEATURE [App::DocumentObjectGroupPython] C_element111  label="C_element : 0.111"  # scripted group (container) (typed FeaturePython)
  n = 0.111
FEATURE [App::DocumentObjectGroupPython] N_element043  label="N_element : 0.026"  # scripted group (container) (typed FeaturePython)
  n = 0.026
FEATURE [App::DocumentObjectGroupPython] O_element095  label="O_element : 0.762"  # scripted group (container) (typed FeaturePython)
  n = 0.762
FEATURE [App::DocumentObjectGroupPython] G4_TISSUE_SOFT_ICRU_4  label="G4_TISSUE_SOFT_ICRU-4"  # scripted group (container) (typed FeaturePython)
  Dunit = g/cm3
  Dvalue = 1
  Group = -> [H_element101,C_element111,N_element043,O_element095]
  conduct = 2
  density = 1
  expand = 3
  formula = G4_TISSUE_SOFT_ICRU-4
  name = G4_TISSUE_SOFT_ICRU-4
  specific = 4
FEATURE [App::DocumentObjectGroupPython] H_element102  label="H_element : 0.149"  # scripted group (container) (typed FeaturePython)
  n = 0.101869
FEATURE [App::DocumentObjectGroupPython] C_element112  label="C_element : 0.456"  # scripted group (container) (typed FeaturePython)
  n = 0.456179
FEATURE [App::DocumentObjectGroupPython] N_element044  label="N_element : 0.761"  # scripted group (container) (typed FeaturePython)
  n = 0.035172
FEATURE [App::DocumentObjectGroupPython] O_element096  label="O_element : 0.407"  # scripted group (container) (typed FeaturePython)
  n = 0.40678
FEATURE [App::DocumentObjectGroupPython] G4_TISSUE_METHANE  label="G4_TISSUE-METHANE"  # scripted group (container) (typed FeaturePython)
  Dunit = g/cm3
  Dvalue = 0.00106409
  Group = -> [H_element102,C_element112,N_element044,O_element096]
  conduct = 2
  density = 1
  expand = 3
  formula = G4_TISSUE-METHANE
  name = G4_TISSUE-METHANE
  specific = 4
FEATURE [App::DocumentObjectGroupPython] H_element103  label="H_element : 0.103"  # scripted group (container) (typed FeaturePython)
  n = 0.102672
FEATURE [App::DocumentObjectGroupPython] C_element113  label="C_element : 0.569"  # scripted group (container) (typed FeaturePython)
  n = 0.56894
FEATURE [App::DocumentObjectGroupPython] N_element045  label="N_element : 0.762"  # scripted group (container) (typed FeaturePython)
  n = 0.035022
FEATURE [App::DocumentObjectGroupPython] O_element097  label="O_element : 0.293"  # scripted group (container) (typed FeaturePython)
  n = 0.293366
FEATURE [App::DocumentObjectGroupPython] G4_TISSUE_PROPANE  label="G4_TISSUE-PROPANE"  # scripted group (container) (typed FeaturePython)
  Dunit = g/cm3
  Dvalue = 0.00182628
  Group = -> [H_element103,C_element113,N_element045,O_element097]
  conduct = 2
  density = 1
  expand = 3
  formula = G4_TISSUE-PROPANE
  name = G4_TISSUE-PROPANE
  specific = 4
FEATURE [App::DocumentObjectGroupPython] Ti_element003  label="Ti_element : 1"  # scripted group (container) (typed FeaturePython)
  n = 1
  ref = Ti_element
FEATURE [App::DocumentObjectGroupPython] O_element098  label="O_element : 052"  # scripted group (container) (typed FeaturePython)
  n = 2
  ref = O_element
FEATURE [App::DocumentObjectGroupPython] G4_TITANIUM_DIOXIDE  # scripted group (container) (typed FeaturePython)
  Dunit = g/cm3
  Dvalue = 4.26
  Group = -> [Ti_element003,O_element098]
  conduct = 2
  density = 1
  expand = 3
  formula = G4_TITANIUM_DIOXIDE
  name = G4_TITANIUM_DIOXIDE
  specific = 4
FEATURE [App::DocumentObjectGroupPython] C_element114  label="C_element : 061"  # scripted group (container) (typed FeaturePython)
  n = 7
  ref = C_element
FEATURE [App::DocumentObjectGroupPython] H_element104  label="H_element : 055"  # scripted group (container) (typed FeaturePython)
  n = 8
  ref = H_element
FEATURE [App::DocumentObjectGroupPython] G4_TOLUENE  # scripted group (container) (typed FeaturePython)
  Dunit = g/cm3
  Dvalue = 0.8669
  Group = -> [C_element114,H_element104]
  conduct = 2
  density = 1
  expand = 3
  formula = G4_TOLUENE
  name = G4_TOLUENE
  specific = 4
FEATURE [App::DocumentObjectGroupPython] C_element115  label="C_element : 062"  # scripted group (container) (typed FeaturePython)
  n = 2
  ref = C_element
FEATURE [App::DocumentObjectGroupPython] H_element105  label="H_element : 056"  # scripted group (container) (typed FeaturePython)
  n = 1
  ref = H_element
FEATURE [App::DocumentObjectGroupPython] Cl_element028  label="Cl_element : 014"  # scripted group (container) (typed FeaturePython)
  n = 3
  ref = Cl_element
FEATURE [App::DocumentObjectGroupPython] G4_TRICHLOROETHYLENE  # scripted group (container) (typed FeaturePython)
  Dunit = g/cm3
  Dvalue = 1.46
  Group = -> [C_element115,H_element105,Cl_element028]
  conduct = 2
  density = 1
  expand = 3
  formula = G4_TRICHLOROETHYLENE
  name = G4_TRICHLOROETHYLENE
  specific = 4
FEATURE [App::DocumentObjectGroupPython] C_element116  label="C_element : 063"  # scripted group (container) (typed FeaturePython)
  n = 6
  ref = C_element
FEATURE [App::DocumentObjectGroupPython] H_element106  label="H_element : 15"  # scripted group (container) (typed FeaturePython)
  n = 15
  ref = H_element
FEATURE [App::DocumentObjectGroupPython] O_element099  label="O_element : 053"  # scripted group (container) (typed FeaturePython)
  n = 4
  ref = O_element
FEATURE [App::DocumentObjectGroupPython] P_element012  label="P_element : 1"  # scripted group (container) (typed FeaturePython)
  n = 1
  ref = P_element
FEATURE [App::DocumentObjectGroupPython] G4_TRIETHYL_PHOSPHATE  # scripted group (container) (typed FeaturePython)
  Dunit = g/cm3
  Dvalue = 1.07
  Group = -> [C_element116,H_element106,O_element099,P_element012]
  conduct = 2
  density = 1
  expand = 3
  formula = G4_TRIETHYL_PHOSPHATE
  name = G4_TRIETHYL_PHOSPHATE
  specific = 4
FEATURE [App::DocumentObjectGroupPython] W_element003  label="W_element : 003"  # scripted group (container) (typed FeaturePython)
  n = 1
  ref = W_element
FEATURE [App::DocumentObjectGroupPython] F_element017  label="F_element : 6"  # scripted group (container) (typed FeaturePython)
  n = 6
  ref = F_element
FEATURE [App::DocumentObjectGroupPython] G4_TUNGSTEN_HEXAFLUORIDE  # scripted group (container) (typed FeaturePython)
  Dunit = g/cm3
  Dvalue = 2.4
  Group = -> [W_element003,F_element017]
  conduct = 2
  density = 1
  expand = 3
  formula = G4_TUNGSTEN_HEXAFLUORIDE
  name = G4_TUNGSTEN_HEXAFLUORIDE
  specific = 4
FEATURE [App::DocumentObjectGroupPython] U_element001  label="U_element : 1"  # scripted group (container) (typed FeaturePython)
  n = 1
  ref = U_element
FEATURE [App::DocumentObjectGroupPython] C_element117  label="C_element : 064"  # scripted group (container) (typed FeaturePython)
  n = 2
  ref = C_element
FEATURE [App::DocumentObjectGroupPython] G4_URANIUM_DICARBIDE  # scripted group (container) (typed FeaturePython)
  Dunit = g/cm3
  Dvalue = 11.28
  Group = -> [U_element001,C_element117]
  conduct = 2
  density = 1
  expand = 3
  formula = G4_URANIUM_DICARBIDE
  name = G4_URANIUM_DICARBIDE
  specific = 4
FEATURE [App::DocumentObjectGroupPython] U_element002  label="U_element : 002"  # scripted group (container) (typed FeaturePython)
  n = 1
  ref = U_element
FEATURE [App::DocumentObjectGroupPython] C_element118  label="C_element : 065"  # scripted group (container) (typed FeaturePython)
  n = 1
  ref = C_element
FEATURE [App::DocumentObjectGroupPython] G4_URANIUM_MONOCARBIDE  # scripted group (container) (typed FeaturePython)
  Dunit = g/cm3
  Dvalue = 13.63
  Group = -> [U_element002,C_element118]
  conduct = 2
  density = 1
  expand = 3
  formula = G4_URANIUM_MONOCARBIDE
  name = G4_URANIUM_MONOCARBIDE
  specific = 4
FEATURE [App::DocumentObjectGroupPython] U_element003  label="U_element : 003"  # scripted group (container) (typed FeaturePython)
  n = 1
  ref = U_element
FEATURE [App::DocumentObjectGroupPython] O_element100  label="O_element : 054"  # scripted group (container) (typed FeaturePython)
  n = 2
  ref = O_element
FEATURE [App::DocumentObjectGroupPython] G4_URANIUM_OXIDE  # scripted group (container) (typed FeaturePython)
  Dunit = g/cm3
  Dvalue = 10.96
  Group = -> [U_element003,O_element100]
  conduct = 2
  density = 1
  expand = 3
  formula = G4_URANIUM_OXIDE
  name = G4_URANIUM_OXIDE
  specific = 4
FEATURE [App::DocumentObjectGroupPython] C_element119  label="C_element : 066"  # scripted group (container) (typed FeaturePython)
  n = 1
  ref = C_element
FEATURE [App::DocumentObjectGroupPython] H_element107  label="H_element : 057"  # scripted group (container) (typed FeaturePython)
  n = 4
  ref = H_element
FEATURE [App::DocumentObjectGroupPython] N_element046  label="N_element : 019"  # scripted group (container) (typed FeaturePython)
  n = 2
  ref = N_element
FEATURE [App::DocumentObjectGroupPython] O_element101  label="O_element : 055"  # scripted group (container) (typed FeaturePython)
  n = 1
  ref = O_element
FEATURE [App::DocumentObjectGroupPython] G4_UREA  # scripted group (container) (typed FeaturePython)
  Dunit = g/cm3
  Dvalue = 1.323
  Group = -> [C_element119,H_element107,N_element046,O_element101]
  conduct = 2
  density = 1
  expand = 3
  formula = G4_UREA
  name = G4_UREA
  specific = 4
FEATURE [App::DocumentObjectGroupPython] C_element120  label="C_element : 067"  # scripted group (container) (typed FeaturePython)
  n = 5
  ref = C_element
FEATURE [App::DocumentObjectGroupPython] H_element108  label="H_element : 058"  # scripted group (container) (typed FeaturePython)
  n = 11
  ref = H_element
FEATURE [App::DocumentObjectGroupPython] N_element047  label="N_element : 020"  # scripted group (container) (typed FeaturePython)
  n = 1
  ref = N_element
FEATURE [App::DocumentObjectGroupPython] O_element102  label="O_element : 056"  # scripted group (container) (typed FeaturePython)
  n = 2
  ref = O_element
FEATURE [App::DocumentObjectGroupPython] G4_VALINE  # scripted group (container) (typed FeaturePython)
  Dunit = g/cm3
  Dvalue = 1.23
  Group = -> [C_element120,H_element108,N_element047,O_element102]
  conduct = 2
  density = 1
  expand = 3
  formula = G4_VALINE
  name = G4_VALINE
  specific = 4
FEATURE [App::DocumentObjectGroupPython] H_element109  label="H_element : 0.009"  # scripted group (container) (typed FeaturePython)
  n = 0.009417
FEATURE [App::DocumentObjectGroupPython] C_element121  label="C_element : 0.281"  # scripted group (container) (typed FeaturePython)
  n = 0.280555
FEATURE [App::DocumentObjectGroupPython] F_element018  label="F_element : 0.710"  # scripted group (container) (typed FeaturePython)
  n = 0.710028
FEATURE [App::DocumentObjectGroupPython] G4_VITON  # scripted group (container) (typed FeaturePython)
  Dunit = g/cm3
  Dvalue = 1.8
  Group = -> [H_element109,C_element121,F_element018]
  conduct = 2
  density = 1
  expand = 3
  formula = G4_VITON
  name = G4_VITON
  specific = 4
FEATURE [App::DocumentObjectGroupPython] H_element110  label="H_element : 059"  # scripted group (container) (typed FeaturePython)
  n = 2
  ref = H_element
FEATURE [App::DocumentObjectGroupPython] O_element103  label="O_element : 057"  # scripted group (container) (typed FeaturePython)
  n = 1
  ref = O_element
FEATURE [App::DocumentObjectGroupPython] G4_WATER  # scripted group (container) (typed FeaturePython)
  Dunit = g/cm3
  Dvalue = 1
  Group = -> [H_element110,O_element103]
  conduct = 2
  density = 1
  expand = 3
  formula = G4_WATER
  name = G4_WATER
  specific = 4
FEATURE [App::DocumentObjectGroupPython] H_element111  label="H_element : 060"  # scripted group (container) (typed FeaturePython)
  n = 2
  ref = H_element
FEATURE [App::DocumentObjectGroupPython] O_element104  label="O_element : 058"  # scripted group (container) (typed FeaturePython)
  n = 1
  ref = O_element
FEATURE [App::DocumentObjectGroupPython] G4_WATER_VAPOR  # scripted group (container) (typed FeaturePython)
  Dunit = g/cm3
  Dvalue = 0.000756182
  Group = -> [H_element111,O_element104]
  conduct = 2
  density = 1
  expand = 3
  formula = G4_WATER_VAPOR
  name = G4_WATER_VAPOR
  specific = 4
FEATURE [App::DocumentObjectGroupPython] C_element122  label="C_element : 068"  # scripted group (container) (typed FeaturePython)
  n = 8
  ref = C_element
FEATURE [App::DocumentObjectGroupPython] H_element112  label="H_element : 061"  # scripted group (container) (typed FeaturePython)
  n = 10
  ref = H_element
FEATURE [App::DocumentObjectGroupPython] G4_XYLENE  # scripted group (container) (typed FeaturePython)
  Dunit = g/cm3
  Dvalue = 0.87
  Group = -> [C_element122,H_element112]
  conduct = 2
  density = 1
  expand = 3
  formula = G4_XYLENE
  name = G4_XYLENE
  specific = 4
FEATURE [App::DocumentObjectGroupPython] C_element123  label="C_element : 069"  # scripted group (container) (typed FeaturePython)
  n = 1
  ref = C_element
FEATURE [App::DocumentObjectGroupPython] G4_GRAPHITE  # scripted group (container) (typed FeaturePython)
  Dunit = g/cm3
  Dvalue = 2.21
  Group = -> [C_element123]
  conduct = 2
  density = 1
  expand = 3
  formula = G4_GRAPHITE
  name = G4_GRAPHITE
  specific = 4
FEATURE [App::DocumentObjectGroupPython] NIST  # scripted group (container) (typed FeaturePython)
  Group = -> [G4_A_150_TISSUE,G4_ACETONE,G4_ACETYLENE,G4_ADENINE,G4_ADIPOSE_TISSUE_ICRP,G4_AIR,G4_ALANINE,G4_ALUMINUM_OXIDE,G4_AMBER,G4_AMMONIA,G4_ANILINE,G4_ANTHRACENE,G4_B_100_BONE,G4_BAKELITE,G4_BARIUM_FLUORIDE,G4_BARIUM_SULFATE,G4_BENZENE,G4_BERYLLIUM_OXIDE,G4_BGO,G4_BLOOD_ICRP,G4_BONE_COMPACT_ICRU,G4_BONE_CORTICAL_ICRP,G4_BORON_CARBIDE,G4_BORON_OXIDE,G4_BRAIN_ICRP,G4_BUTANE,G4_N_BUTYL_ALCOHOL,G4_C_552,+152 more]
FEATURE [App::DocumentObjectGroupPython] H_element113  label="H_element : 062"  # scripted group (container) (typed FeaturePython)
  n = 1
  ref = H_element
FEATURE [App::DocumentObjectGroupPython] G4_H  # scripted group (container) (typed FeaturePython)
  Dunit = g/cm3
  Dvalue = 8.3748e-05
  Group = -> [H_element113]
  conduct = 2
  density = 1
  expand = 3
  formula = H
  name = G4_H
  specific = 4
FEATURE [App::DocumentObjectGroupPython] He_element001  label="He_element : 1"  # scripted group (container) (typed FeaturePython)
  n = 1
  ref = He_element
FEATURE [App::DocumentObjectGroupPython] G4_He  # scripted group (container) (typed FeaturePython)
  Dunit = g/cm3
  Dvalue = 0.000166322
  Group = -> [He_element001]
  conduct = 2
  density = 1
  expand = 3
  formula = He
  name = G4_He
  specific = 4
FEATURE [App::DocumentObjectGroupPython] Li_element008  label="Li_element : 008"  # scripted group (container) (typed FeaturePython)
  n = 1
  ref = Li_element
FEATURE [App::DocumentObjectGroupPython] G4_Li  # scripted group (container) (typed FeaturePython)
  Dunit = g/cm3
  Dvalue = 0.534
  Group = -> [Li_element008]
  conduct = 2
  density = 1
  expand = 3
  formula = Li
  name = G4_Li
  specific = 4
FEATURE [App::DocumentObjectGroupPython] Be_element002  label="Be_element : 002"  # scripted group (container) (typed FeaturePython)
  n = 1
  ref = Be_element
FEATURE [App::DocumentObjectGroupPython] G4_Be  # scripted group (container) (typed FeaturePython)
  Dunit = g/cm3
  Dvalue = 1.848
  Group = -> [Be_element002]
  conduct = 2
  density = 1
  expand = 3
  formula = Be
  name = G4_Be
  specific = 4
FEATURE [App::DocumentObjectGroupPython] B_element007  label="B_element : 007"  # scripted group (container) (typed FeaturePython)
  n = 1
  ref = B_element
FEATURE [App::DocumentObjectGroupPython] G4_B  # scripted group (container) (typed FeaturePython)
  Dunit = g/cm3
  Dvalue = 2.37
  Group = -> [B_element007]
  conduct = 2
  density = 1
  expand = 3
  formula = B
  name = G4_B
  specific = 4
FEATURE [App::DocumentObjectGroupPython] C_element124  label="C_element : 070"  # scripted group (container) (typed FeaturePython)
  n = 1
  ref = C_element
FEATURE [App::DocumentObjectGroupPython] G4_C  # scripted group (container) (typed FeaturePython)
  Dunit = g/cm3
  Dvalue = 2
  Group = -> [C_element124]
  conduct = 2
  density = 1
  expand = 3
  formula = C
  name = G4_C
  specific = 4
FEATURE [App::DocumentObjectGroupPython] N_element048  label="N_element : 021"  # scripted group (container) (typed FeaturePython)
  n = 1
  ref = N_element
FEATURE [App::DocumentObjectGroupPython] G4_N  # scripted group (container) (typed FeaturePython)
  Dunit = g/cm3
  Dvalue = 0.0011652
  Group = -> [N_element048]
  conduct = 2
  density = 1
  expand = 3
  formula = N
  name = G4_N
  specific = 4
FEATURE [App::DocumentObjectGroupPython] O_element105  label="O_element : 059"  # scripted group (container) (typed FeaturePython)
  n = 1
  ref = O_element
FEATURE [App::DocumentObjectGroupPython] G4_O  # scripted group (container) (typed FeaturePython)
  Dunit = g/cm3
  Dvalue = 0.00133151
  Group = -> [O_element105]
  conduct = 2
  density = 1
  expand = 3
  formula = O
  name = G4_O
  specific = 4
FEATURE [App::DocumentObjectGroupPython] F_element019  label="F_element : 008"  # scripted group (container) (typed FeaturePython)
  n = 1
  ref = F_element
FEATURE [App::DocumentObjectGroupPython] G4_F  # scripted group (container) (typed FeaturePython)
  Dunit = g/cm3
  Dvalue = 0.00158029
  Group = -> [F_element019]
  conduct = 2
  density = 1
  expand = 3
  formula = F
  name = G4_F
  specific = 4
FEATURE [App::DocumentObjectGroupPython] Ne_element001  label="Ne_element : 1"  # scripted group (container) (typed FeaturePython)
  n = 1
  ref = Ne_element
FEATURE [App::DocumentObjectGroupPython] G4_Ne  # scripted group (container) (typed FeaturePython)
  Dunit = g/cm3
  Dvalue = 0.000838505
  Group = -> [Ne_element001]
  conduct = 2
  density = 1
  expand = 3
  formula = Ne
  name = G4_Ne
  specific = 4
FEATURE [App::DocumentObjectGroupPython] Na_element020  label="Na_element : 005"  # scripted group (container) (typed FeaturePython)
  n = 1
  ref = Na_element
FEATURE [App::DocumentObjectGroupPython] G4_Na  # scripted group (container) (typed FeaturePython)
  Dunit = g/cm3
  Dvalue = 0.971
  Group = -> [Na_element020]
  conduct = 2
  density = 1
  expand = 3
  formula = Na
  name = G4_Na
  specific = 4
FEATURE [App::DocumentObjectGroupPython] Mg_element011  label="Mg_element : 005"  # scripted group (container) (typed FeaturePython)
  n = 1
  ref = Mg_element
FEATURE [App::DocumentObjectGroupPython] G4_Mg  # scripted group (container) (typed FeaturePython)
  Dunit = g/cm3
  Dvalue = 1.74
  Group = -> [Mg_element011]
  conduct = 2
  density = 1
  expand = 3
  formula = Mg
  name = G4_Mg
  specific = 4
FEATURE [App::DocumentObjectGroupPython] Al_element004  label="Al_element : 1"  # scripted group (container) (typed FeaturePython)
  n = 1
  ref = Al_element
FEATURE [App::DocumentObjectGroupPython] G4_Al  # scripted group (container) (typed FeaturePython)
  Dunit = g/cm3
  Dvalue = 2.699
  Group = -> [Al_element004]
  conduct = 2
  density = 1
  expand = 3
  formula = Al
  name = G4_Al
  specific = 4
FEATURE [App::DocumentObjectGroupPython] Si_element007  label="Si_element : 002"  # scripted group (container) (typed FeaturePython)
  n = 1
  ref = Si_element
FEATURE [App::DocumentObjectGroupPython] G4_Si  # scripted group (container) (typed FeaturePython)
  Dunit = g/cm3
  Dvalue = 2.33
  Group = -> [Si_element007]
  conduct = 2
  density = 1
  expand = 3
  formula = Si
  name = G4_Si
  specific = 4
FEATURE [App::DocumentObjectGroupPython] P_element013  label="P_element : 002"  # scripted group (container) (typed FeaturePython)
  n = 1
  ref = P_element
FEATURE [App::DocumentObjectGroupPython] G4_P  # scripted group (container) (typed FeaturePython)
  Dunit = g/cm3
  Dvalue = 2.2
  Group = -> [P_element013]
  conduct = 2
  density = 1
  expand = 3
  formula = P
  name = G4_P
  specific = 4
FEATURE [App::DocumentObjectGroupPython] S_element023  label="S_element : 007"  # scripted group (container) (typed FeaturePython)
  n = 1
  ref = S_element
FEATURE [App::DocumentObjectGroupPython] G4_S  # scripted group (container) (typed FeaturePython)
  Dunit = g/cm3
  Dvalue = 2
  Group = -> [S_element023]
  conduct = 2
  density = 1
  expand = 3
  formula = S
  name = G4_S
  specific = 4
FEATURE [App::DocumentObjectGroupPython] Cl_element029  label="Cl_element : 015"  # scripted group (container) (typed FeaturePython)
  n = 1
  ref = Cl_element
FEATURE [App::DocumentObjectGroupPython] G4_Cl  # scripted group (container) (typed FeaturePython)
  Dunit = g/cm3
  Dvalue = 0.00299473
  Group = -> [Cl_element029]
  conduct = 2
  density = 1
  expand = 3
  formula = Cl
  name = G4_Cl
  specific = 4
FEATURE [App::DocumentObjectGroupPython] Ar_element002  label="Ar_element : 1"  # scripted group (container) (typed FeaturePython)
  n = 1
  ref = Ar_element
FEATURE [App::DocumentObjectGroupPython] G4_Ar  # scripted group (container) (typed FeaturePython)
  Dunit = g/cm3
  Dvalue = 0.00166201
  Group = -> [Ar_element002]
  conduct = 2
  density = 1
  expand = 3
  formula = Ar
  name = G4_Ar
  specific = 4
FEATURE [App::DocumentObjectGroupPython] K_element013  label="K_element : 003"  # scripted group (container) (typed FeaturePython)
  n = 1
  ref = K_element
FEATURE [App::DocumentObjectGroupPython] G4_K  # scripted group (container) (typed FeaturePython)
  Dunit = g/cm3
  Dvalue = 0.862
  Group = -> [K_element013]
  conduct = 2
  density = 1
  expand = 3
  formula = K
  name = G4_K
  specific = 4
FEATURE [App::DocumentObjectGroupPython] Ca_element014  label="Ca_element : 007"  # scripted group (container) (typed FeaturePython)
  n = 1
  ref = Ca_element
FEATURE [App::DocumentObjectGroupPython] G4_Ca  # scripted group (container) (typed FeaturePython)
  Dunit = g/cm3
  Dvalue = 1.55
  Group = -> [Ca_element014]
  conduct = 2
  density = 1
  expand = 3
  formula = Ca
  name = G4_Ca
  specific = 4
FEATURE [App::DocumentObjectGroupPython] Sc_element001  label="Sc_element : 1"  # scripted group (container) (typed FeaturePython)
  n = 1
  ref = Sc_element
FEATURE [App::DocumentObjectGroupPython] G4_Sc  # scripted group (container) (typed FeaturePython)
  Dunit = g/cm3
  Dvalue = 2.989
  Group = -> [Sc_element001]
  conduct = 2
  density = 1
  expand = 3
  formula = Sc
  name = G4_Sc
  specific = 4
FEATURE [App::DocumentObjectGroupPython] Ti_element004  label="Ti_element : 002"  # scripted group (container) (typed FeaturePython)
  n = 1
  ref = Ti_element
FEATURE [App::DocumentObjectGroupPython] G4_Ti  # scripted group (container) (typed FeaturePython)
  Dunit = g/cm3
  Dvalue = 4.54
  Group = -> [Ti_element004]
  conduct = 2
  density = 1
  expand = 3
  formula = Ti
  name = G4_Ti
  specific = 4
FEATURE [App::DocumentObjectGroupPython] V_element001  label="V_element : 1"  # scripted group (container) (typed FeaturePython)
  n = 1
  ref = V_element
FEATURE [App::DocumentObjectGroupPython] G4_V  # scripted group (container) (typed FeaturePython)
  Dunit = g/cm3
  Dvalue = 6.11
  Group = -> [V_element001]
  conduct = 2
  density = 1
  expand = 3
  formula = V
  name = G4_V
  specific = 4
FEATURE [App::DocumentObjectGroupPython] Cr_element001  label="Cr_element : 1"  # scripted group (container) (typed FeaturePython)
  n = 1
  ref = Cr_element
FEATURE [App::DocumentObjectGroupPython] G4_Cr  # scripted group (container) (typed FeaturePython)
  Dunit = g/cm3
  Dvalue = 7.18
  Group = -> [Cr_element001]
  conduct = 2
  density = 1
  expand = 3
  formula = Cr
  name = G4_Cr
  specific = 4
FEATURE [App::DocumentObjectGroupPython] Mn_element001  label="Mn_element : 1"  # scripted group (container) (typed FeaturePython)
  n = 1
  ref = Mn_element
FEATURE [App::DocumentObjectGroupPython] G4_Mn  # scripted group (container) (typed FeaturePython)
  Dunit = g/cm3
  Dvalue = 7.44
  Group = -> [Mn_element001]
  conduct = 2
  density = 1
  expand = 3
  formula = Mn
  name = G4_Mn
  specific = 4
FEATURE [App::DocumentObjectGroupPython] Fe_element007  label="Fe_element : 004"  # scripted group (container) (typed FeaturePython)
  n = 1
  ref = Fe_element
FEATURE [App::DocumentObjectGroupPython] G4_Fe  # scripted group (container) (typed FeaturePython)
  Dunit = g/cm3
  Dvalue = 7.874
  Group = -> [Fe_element007]
  conduct = 2
  density = 1
  expand = 3
  formula = Fe
  name = G4_Fe
  specific = 4
FEATURE [App::DocumentObjectGroupPython] Co_element001  label="Co_element : 1"  # scripted group (container) (typed FeaturePython)
  n = 1
  ref = Co_element
FEATURE [App::DocumentObjectGroupPython] G4_Co  # scripted group (container) (typed FeaturePython)
  Dunit = g/cm3
  Dvalue = 8.9
  Group = -> [Co_element001]
  conduct = 2
  density = 1
  expand = 3
  formula = Co
  name = G4_Co
  specific = 4
FEATURE [App::DocumentObjectGroupPython] Ni_element001  label="Ni_element : 1"  # scripted group (container) (typed FeaturePython)
  n = 1
  ref = Ni_element
FEATURE [App::DocumentObjectGroupPython] G4_Ni  # scripted group (container) (typed FeaturePython)
  Dunit = g/cm3
  Dvalue = 8.902
  Group = -> [Ni_element001]
  conduct = 2
  density = 1
  expand = 3
  formula = Ni
  name = G4_Ni
  specific = 4
FEATURE [App::DocumentObjectGroupPython] Cu_element001  label="Cu_element : 1"  # scripted group (container) (typed FeaturePython)
  n = 1
  ref = Cu_element
FEATURE [App::DocumentObjectGroupPython] G4_Cu  # scripted group (container) (typed FeaturePython)
  Dunit = g/cm3
  Dvalue = 8.96
  Group = -> [Cu_element001]
  conduct = 2
  density = 1
  expand = 3
  formula = Cu
  name = G4_Cu
  specific = 4
FEATURE [App::DocumentObjectGroupPython] Zn_element001  label="Zn_element : 1"  # scripted group (container) (typed FeaturePython)
  n = 1
  ref = Zn_element
FEATURE [App::DocumentObjectGroupPython] G4_Zn  # scripted group (container) (typed FeaturePython)
  Dunit = g/cm3
  Dvalue = 7.133
  Group = -> [Zn_element001]
  conduct = 2
  density = 1
  expand = 3
  formula = Zn
  name = G4_Zn
  specific = 4
FEATURE [App::DocumentObjectGroupPython] Ga_element002  label="Ga_element : 002"  # scripted group (container) (typed FeaturePython)
  n = 1
  ref = Ga_element
FEATURE [App::DocumentObjectGroupPython] G4_Ga  # scripted group (container) (typed FeaturePython)
  Dunit = g/cm3
  Dvalue = 5.904
  Group = -> [Ga_element002]
  conduct = 2
  density = 1
  expand = 3
  formula = Ga
  name = G4_Ga
  specific = 4
FEATURE [App::DocumentObjectGroupPython] Ge_element002  label="Ge_element : 1"  # scripted group (container) (typed FeaturePython)
  n = 1
  ref = Ge_element
FEATURE [App::DocumentObjectGroupPython] G4_Ge  # scripted group (container) (typed FeaturePython)
  Dunit = g/cm3
  Dvalue = 5.323
  Group = -> [Ge_element002]
  conduct = 2
  density = 1
  expand = 3
  formula = Ge
  name = G4_Ge
  specific = 4
FEATURE [App::DocumentObjectGroupPython] As_element003  label="As_element : 002"  # scripted group (container) (typed FeaturePython)
  n = 1
  ref = As_element
FEATURE [App::DocumentObjectGroupPython] G4_As  # scripted group (container) (typed FeaturePython)
  Dunit = g/cm3
  Dvalue = 5.73
  Group = -> [As_element003]
  conduct = 2
  density = 1
  expand = 3
  formula = As
  name = G4_As
  specific = 4
FEATURE [App::DocumentObjectGroupPython] Se_element001  label="Se_element : 1"  # scripted group (container) (typed FeaturePython)
  n = 1
  ref = Se_element
FEATURE [App::DocumentObjectGroupPython] G4_Se  # scripted group (container) (typed FeaturePython)
  Dunit = g/cm3
  Dvalue = 4.5
  Group = -> [Se_element001]
  conduct = 2
  density = 1
  expand = 3
  formula = Se
  name = G4_Se
  specific = 4
FEATURE [App::DocumentObjectGroupPython] Br_element007  label="Br_element : 004"  # scripted group (container) (typed FeaturePython)
  n = 1
  ref = Br_element
FEATURE [App::DocumentObjectGroupPython] G4_Br  # scripted group (container) (typed FeaturePython)
  Dunit = g/cm3
  Dvalue = 0.0070721
  Group = -> [Br_element007]
  conduct = 2
  density = 1
  expand = 3
  formula = Br
  name = G4_Br
  specific = 4
FEATURE [App::DocumentObjectGroupPython] Kr_element001  label="Kr_element : 1"  # scripted group (container) (typed FeaturePython)
  n = 1
  ref = Kr_element
FEATURE [App::DocumentObjectGroupPython] G4_Kr  # scripted group (container) (typed FeaturePython)
  Dunit = g/cm3
  Dvalue = 0.00347832
  Group = -> [Kr_element001]
  conduct = 2
  density = 1
  expand = 3
  formula = Kr
  name = G4_Kr
  specific = 4
FEATURE [App::DocumentObjectGroupPython] Rb_element001  label="Rb_element : 1"  # scripted group (container) (typed FeaturePython)
  n = 1
  ref = Rb_element
FEATURE [App::DocumentObjectGroupPython] G4_Rb  # scripted group (container) (typed FeaturePython)
  Dunit = g/cm3
  Dvalue = 1.532
  Group = -> [Rb_element001]
  conduct = 2
  density = 1
  expand = 3
  formula = Rb
  name = G4_Rb
  specific = 4
FEATURE [App::DocumentObjectGroupPython] Sr_element001  label="Sr_element : 1"  # scripted group (container) (typed FeaturePython)
  n = 1
  ref = Sr_element
FEATURE [App::DocumentObjectGroupPython] G4_Sr  # scripted group (container) (typed FeaturePython)
  Dunit = g/cm3
  Dvalue = 2.54
  Group = -> [Sr_element001]
  conduct = 2
  density = 1
  expand = 3
  formula = Sr
  name = G4_Sr
  specific = 4
FEATURE [App::DocumentObjectGroupPython] Y_element001  label="Y_element : 1"  # scripted group (container) (typed FeaturePython)
  n = 1
  ref = Y_element
FEATURE [App::DocumentObjectGroupPython] G4_Y  # scripted group (container) (typed FeaturePython)
  Dunit = g/cm3
  Dvalue = 4.469
  Group = -> [Y_element001]
  conduct = 2
  density = 1
  expand = 3
  formula = Y
  name = G4_Y
  specific = 4
FEATURE [App::DocumentObjectGroupPython] Zr_element001  label="Zr_element : 1"  # scripted group (container) (typed FeaturePython)
  n = 1
  ref = Zr_element
FEATURE [App::DocumentObjectGroupPython] G4_Zr  # scripted group (container) (typed FeaturePython)
  Dunit = g/cm3
  Dvalue = 6.506
  Group = -> [Zr_element001]
  conduct = 2
  density = 1
  expand = 3
  formula = Zr
  name = G4_Zr
  specific = 4
FEATURE [App::DocumentObjectGroupPython] Nb_element001  label="Nb_element : 1"  # scripted group (container) (typed FeaturePython)
  n = 1
  ref = Nb_element
FEATURE [App::DocumentObjectGroupPython] G4_Nb  # scripted group (container) (typed FeaturePython)
  Dunit = g/cm3
  Dvalue = 8.57
  Group = -> [Nb_element001]
  conduct = 2
  density = 1
  expand = 3
  formula = Nb
  name = G4_Nb
  specific = 4
FEATURE [App::DocumentObjectGroupPython] Mo_element001  label="Mo_element : 1"  # scripted group (container) (typed FeaturePython)
  n = 1
  ref = Mo_element
FEATURE [App::DocumentObjectGroupPython] G4_Mo  # scripted group (container) (typed FeaturePython)
  Dunit = g/cm3
  Dvalue = 10.22
  Group = -> [Mo_element001]
  conduct = 2
  density = 1
  expand = 3
  formula = Mo
  name = G4_Mo
  specific = 4
FEATURE [App::DocumentObjectGroupPython] Tc_element001  label="Tc_element : 1"  # scripted group (container) (typed FeaturePython)
  n = 1
  ref = Tc_element
FEATURE [App::DocumentObjectGroupPython] G4_Tc  # scripted group (container) (typed FeaturePython)
  Dunit = g/cm3
  Dvalue = 11.5
  Group = -> [Tc_element001]
  conduct = 2
  density = 1
  expand = 3
  formula = Tc
  name = G4_Tc
  specific = 4
FEATURE [App::DocumentObjectGroupPython] Ru_element001  label="Ru_element : 1"  # scripted group (container) (typed FeaturePython)
  n = 1
  ref = Ru_element
FEATURE [App::DocumentObjectGroupPython] G4_Ru  # scripted group (container) (typed FeaturePython)
  Dunit = g/cm3
  Dvalue = 12.41
  Group = -> [Ru_element001]
  conduct = 2
  density = 1
  expand = 3
  formula = Ru
  name = G4_Ru
  specific = 4
FEATURE [App::DocumentObjectGroupPython] Rh_element001  label="Rh_element : 1"  # scripted group (container) (typed FeaturePython)
  n = 1
  ref = Rh_element
FEATURE [App::DocumentObjectGroupPython] G4_Rh  # scripted group (container) (typed FeaturePython)
  Dunit = g/cm3
  Dvalue = 12.41
  Group = -> [Rh_element001]
  conduct = 2
  density = 1
  expand = 3
  formula = Rh
  name = G4_Rh
  specific = 4
FEATURE [App::DocumentObjectGroupPython] Pd_element001  label="Pd_element : 1"  # scripted group (container) (typed FeaturePython)
  n = 1
  ref = Pd_element
FEATURE [App::DocumentObjectGroupPython] G4_Pd  # scripted group (container) (typed FeaturePython)
  Dunit = g/cm3
  Dvalue = 12.02
  Group = -> [Pd_element001]
  conduct = 2
  density = 1
  expand = 3
  formula = Pd
  name = G4_Pd
  specific = 4
FEATURE [App::DocumentObjectGroupPython] Ag_element006  label="Ag_element : 004"  # scripted group (container) (typed FeaturePython)
  n = 1
  ref = Ag_element
FEATURE [App::DocumentObjectGroupPython] G4_Ag  # scripted group (container) (typed FeaturePython)
  Dunit = g/cm3
  Dvalue = 10.5
  Group = -> [Ag_element006]
  conduct = 2
  density = 1
  expand = 3
  formula = Ag
  name = G4_Ag
  specific = 4
FEATURE [App::DocumentObjectGroupPython] Cd_element003  label="Cd_element : 003"  # scripted group (container) (typed FeaturePython)
  n = 1
  ref = Cd_element
FEATURE [App::DocumentObjectGroupPython] G4_Cd  # scripted group (container) (typed FeaturePython)
  Dunit = g/cm3
  Dvalue = 8.65
  Group = -> [Cd_element003]
  conduct = 2
  density = 1
  expand = 3
  formula = Cd
  name = G4_Cd
  specific = 4
FEATURE [App::DocumentObjectGroupPython] In_element001  label="In_element : 1"  # scripted group (container) (typed FeaturePython)
  n = 1
  ref = In_element
FEATURE [App::DocumentObjectGroupPython] G4_In  # scripted group (container) (typed FeaturePython)
  Dunit = g/cm3
  Dvalue = 7.31
  Group = -> [In_element001]
  conduct = 2
  density = 1
  expand = 3
  formula = In
  name = G4_In
  specific = 4
FEATURE [App::DocumentObjectGroupPython] Sn_element001  label="Sn_element : 1"  # scripted group (container) (typed FeaturePython)
  n = 1
  ref = Sn_element
FEATURE [App::DocumentObjectGroupPython] G4_Sn  # scripted group (container) (typed FeaturePython)
  Dunit = g/cm3
  Dvalue = 7.31
  Group = -> [Sn_element001]
  conduct = 2
  density = 1
  expand = 3
  formula = Sn
  name = G4_Sn
  specific = 4
FEATURE [App::DocumentObjectGroupPython] Sb_element001  label="Sb_element : 1"  # scripted group (container) (typed FeaturePython)
  n = 1
  ref = Sb_element
FEATURE [App::DocumentObjectGroupPython] G4_Sb  # scripted group (container) (typed FeaturePython)
  Dunit = g/cm3
  Dvalue = 6.691
  Group = -> [Sb_element001]
  conduct = 2
  density = 1
  expand = 3
  formula = Sb
  name = G4_Sb
  specific = 4
FEATURE [App::DocumentObjectGroupPython] Te_element002  label="Te_element : 002"  # scripted group (container) (typed FeaturePython)
  n = 1
  ref = Te_element
FEATURE [App::DocumentObjectGroupPython] G4_Te  # scripted group (container) (typed FeaturePython)
  Dunit = g/cm3
  Dvalue = 6.24
  Group = -> [Te_element002]
  conduct = 2
  density = 1
  expand = 3
  formula = Te
  name = G4_Te
  specific = 4
FEATURE [App::DocumentObjectGroupPython] I_element010  label="I_element : 006"  # scripted group (container) (typed FeaturePython)
  n = 1
  ref = I_element
FEATURE [App::DocumentObjectGroupPython] G4_I  # scripted group (container) (typed FeaturePython)
  Dunit = g/cm3
  Dvalue = 4.93
  Group = -> [I_element010]
  conduct = 2
  density = 1
  expand = 3
  formula = I
  name = G4_I
  specific = 4
FEATURE [App::DocumentObjectGroupPython] Xe_element001  label="Xe_element : 1"  # scripted group (container) (typed FeaturePython)
  n = 1
  ref = Xe_element
FEATURE [App::DocumentObjectGroupPython] G4_Xe  # scripted group (container) (typed FeaturePython)
  Dunit = g/cm3
  Dvalue = 0.00548536
  Group = -> [Xe_element001]
  conduct = 2
  density = 1
  expand = 3
  formula = Xe
  name = G4_Xe
  specific = 4
FEATURE [App::DocumentObjectGroupPython] Cs_element003  label="Cs_element : 003"  # scripted group (container) (typed FeaturePython)
  n = 1
  ref = Cs_element
FEATURE [App::DocumentObjectGroupPython] G4_Cs  # scripted group (container) (typed FeaturePython)
  Dunit = g/cm3
  Dvalue = 1.873
  Group = -> [Cs_element003]
  conduct = 2
  density = 1
  expand = 3
  formula = Cs
  name = G4_Cs
  specific = 4
FEATURE [App::DocumentObjectGroupPython] Ba_element003  label="Ba_element : 003"  # scripted group (container) (typed FeaturePython)
  n = 1
  ref = Ba_element
FEATURE [App::DocumentObjectGroupPython] G4_Ba  # scripted group (container) (typed FeaturePython)
  Dunit = g/cm3
  Dvalue = 3.5
  Group = -> [Ba_element003]
  conduct = 2
  density = 1
  expand = 3
  formula = Ba
  name = G4_Ba
  specific = 4
FEATURE [App::DocumentObjectGroupPython] La_element003  label="La_element : 003"  # scripted group (container) (typed FeaturePython)
  n = 1
  ref = La_element
FEATURE [App::DocumentObjectGroupPython] G4_La  # scripted group (container) (typed FeaturePython)
  Dunit = g/cm3
  Dvalue = 6.154
  Group = -> [La_element003]
  conduct = 2
  density = 1
  expand = 3
  formula = La
  name = G4_La
  specific = 4
FEATURE [App::DocumentObjectGroupPython] Ce_element002  label="Ce_element : 1"  # scripted group (container) (typed FeaturePython)
  n = 1
  ref = Ce_element
FEATURE [App::DocumentObjectGroupPython] G4_Ce  # scripted group (container) (typed FeaturePython)
  Dunit = g/cm3
  Dvalue = 6.657
  Group = -> [Ce_element002]
  conduct = 2
  density = 1
  expand = 3
  formula = Ce
  name = G4_Ce
  specific = 4
FEATURE [App::DocumentObjectGroupPython] Pr_element001  label="Pr_element : 1"  # scripted group (container) (typed FeaturePython)
  n = 1
  ref = Pr_element
FEATURE [App::DocumentObjectGroupPython] G4_Pr  # scripted group (container) (typed FeaturePython)
  Dunit = g/cm3
  Dvalue = 6.71
  Group = -> [Pr_element001]
  conduct = 2
  density = 1
  expand = 3
  formula = Pr
  name = G4_Pr
  specific = 4
FEATURE [App::DocumentObjectGroupPython] Nd_element001  label="Nd_element : 1"  # scripted group (container) (typed FeaturePython)
  n = 1
  ref = Nd_element
FEATURE [App::DocumentObjectGroupPython] G4_Nd  # scripted group (container) (typed FeaturePython)
  Dunit = g/cm3
  Dvalue = 6.9
  Group = -> [Nd_element001]
  conduct = 2
  density = 1
  expand = 3
  formula = Nd
  name = G4_Nd
  specific = 4
FEATURE [App::DocumentObjectGroupPython] Pm_element001  label="Pm_element : 1"  # scripted group (container) (typed FeaturePython)
  n = 1
  ref = Pm_element
FEATURE [App::DocumentObjectGroupPython] G4_Pm  # scripted group (container) (typed FeaturePython)
  Dunit = g/cm3
  Dvalue = 7.22
  Group = -> [Pm_element001]
  conduct = 2
  density = 1
  expand = 3
  formula = Pm
  name = G4_Pm
  specific = 4
FEATURE [App::DocumentObjectGroupPython] Sm_element001  label="Sm_element : 1"  # scripted group (container) (typed FeaturePython)
  n = 1
  ref = Sm_element
FEATURE [App::DocumentObjectGroupPython] G4_Sm  # scripted group (container) (typed FeaturePython)
  Dunit = g/cm3
  Dvalue = 7.46
  Group = -> [Sm_element001]
  conduct = 2
  density = 1
  expand = 3
  formula = Sm
  name = G4_Sm
  specific = 4
FEATURE [App::DocumentObjectGroupPython] Eu_element001  label="Eu_element : 1"  # scripted group (container) (typed FeaturePython)
  n = 1
  ref = Eu_element
FEATURE [App::DocumentObjectGroupPython] G4_Eu  # scripted group (container) (typed FeaturePython)
  Dunit = g/cm3
  Dvalue = 5.243
  Group = -> [Eu_element001]
  conduct = 2
  density = 1
  expand = 3
  formula = Eu
  name = G4_Eu
  specific = 4
FEATURE [App::DocumentObjectGroupPython] Gd_element002  label="Gd_element : 1"  # scripted group (container) (typed FeaturePython)
  n = 1
  ref = Gd_element
FEATURE [App::DocumentObjectGroupPython] G4_Gd  # scripted group (container) (typed FeaturePython)
  Dunit = g/cm3
  Dvalue = 7.9004
  Group = -> [Gd_element002]
  conduct = 2
  density = 1
  expand = 3
  formula = Gd
  name = G4_Gd
  specific = 4
FEATURE [App::DocumentObjectGroupPython] Tb_element001  label="Tb_element : 1"  # scripted group (container) (typed FeaturePython)
  n = 1
  ref = Tb_element
FEATURE [App::DocumentObjectGroupPython] G4_Tb  # scripted group (container) (typed FeaturePython)
  Dunit = g/cm3
  Dvalue = 8.229
  Group = -> [Tb_element001]
  conduct = 2
  density = 1
  expand = 3
  formula = Tb
  name = G4_Tb
  specific = 4
FEATURE [App::DocumentObjectGroupPython] Dy_element001  label="Dy_element : 1"  # scripted group (container) (typed FeaturePython)
  n = 1
  ref = Dy_element
FEATURE [App::DocumentObjectGroupPython] G4_Dy  # scripted group (container) (typed FeaturePython)
  Dunit = g/cm3
  Dvalue = 8.55
  Group = -> [Dy_element001]
  conduct = 2
  density = 1
  expand = 3
  formula = Dy
  name = G4_Dy
  specific = 4
FEATURE [App::DocumentObjectGroupPython] Ho_element001  label="Ho_element : 1"  # scripted group (container) (typed FeaturePython)
  n = 1
  ref = Ho_element
FEATURE [App::DocumentObjectGroupPython] G4_Ho  # scripted group (container) (typed FeaturePython)
  Dunit = g/cm3
  Dvalue = 8.795
  Group = -> [Ho_element001]
  conduct = 2
  density = 1
  expand = 3
  formula = Ho
  name = G4_Ho
  specific = 4
FEATURE [App::DocumentObjectGroupPython] Er_element001  label="Er_element : 1"  # scripted group (container) (typed FeaturePython)
  n = 1
  ref = Er_element
FEATURE [App::DocumentObjectGroupPython] G4_Er  # scripted group (container) (typed FeaturePython)
  Dunit = g/cm3
  Dvalue = 9.066
  Group = -> [Er_element001]
  conduct = 2
  density = 1
  expand = 3
  formula = Er
  name = G4_Er
  specific = 4
FEATURE [App::DocumentObjectGroupPython] Tm_element001  label="Tm_element : 1"  # scripted group (container) (typed FeaturePython)
  n = 1
  ref = Tm_element
FEATURE [App::DocumentObjectGroupPython] G4_Tm  # scripted group (container) (typed FeaturePython)
  Dunit = g/cm3
  Dvalue = 9.321
  Group = -> [Tm_element001]
  conduct = 2
  density = 1
  expand = 3
  formula = Tm
  name = G4_Tm
  specific = 4
FEATURE [App::DocumentObjectGroupPython] Yb_element001  label="Yb_element : 1"  # scripted group (container) (typed FeaturePython)
  n = 1
  ref = Yb_element
FEATURE [App::DocumentObjectGroupPython] G4_Yb  # scripted group (container) (typed FeaturePython)
  Dunit = g/cm3
  Dvalue = 6.73
  Group = -> [Yb_element001]
  conduct = 2
  density = 1
  expand = 3
  formula = Yb
  name = G4_Yb
  specific = 4
FEATURE [App::DocumentObjectGroupPython] Lu_element001  label="Lu_element : 1"  # scripted group (container) (typed FeaturePython)
  n = 1
  ref = Lu_element
FEATURE [App::DocumentObjectGroupPython] G4_Lu  # scripted group (container) (typed FeaturePython)
  Dunit = g/cm3
  Dvalue = 9.84
  Group = -> [Lu_element001]
  conduct = 2
  density = 1
  expand = 3
  formula = Lu
  name = G4_Lu
  specific = 4
FEATURE [App::DocumentObjectGroupPython] Hf_element001  label="Hf_element : 1"  # scripted group (container) (typed FeaturePython)
  n = 1
  ref = Hf_element
FEATURE [App::DocumentObjectGroupPython] G4_Hf  # scripted group (container) (typed FeaturePython)
  Dunit = g/cm3
  Dvalue = 13.31
  Group = -> [Hf_element001]
  conduct = 2
  density = 1
  expand = 3
  formula = Hf
  name = G4_Hf
  specific = 4
FEATURE [App::DocumentObjectGroupPython] Ta_element001  label="Ta_element : 1"  # scripted group (container) (typed FeaturePython)
  n = 1
  ref = Ta_element
FEATURE [App::DocumentObjectGroupPython] G4_Ta  # scripted group (container) (typed FeaturePython)
  Dunit = g/cm3
  Dvalue = 16.654
  Group = -> [Ta_element001]
  conduct = 2
  density = 1
  expand = 3
  formula = Ta
  name = G4_Ta
  specific = 4
FEATURE [App::DocumentObjectGroupPython] W_element004  label="W_element : 004"  # scripted group (container) (typed FeaturePython)
  n = 1
  ref = W_element
FEATURE [App::DocumentObjectGroupPython] G4_W  # scripted group (container) (typed FeaturePython)
  Dunit = g/cm3
  Dvalue = 19.3
  Group = -> [W_element004]
  conduct = 2
  density = 1
  expand = 3
  formula = W
  name = G4_W
  specific = 4
FEATURE [App::DocumentObjectGroupPython] Re_element001  label="Re_element : 1"  # scripted group (container) (typed FeaturePython)
  n = 1
  ref = Re_element
FEATURE [App::DocumentObjectGroupPython] G4_Re  # scripted group (container) (typed FeaturePython)
  Dunit = g/cm3
  Dvalue = 21.02
  Group = -> [Re_element001]
  conduct = 2
  density = 1
  expand = 3
  formula = Re
  name = G4_Re
  specific = 4
FEATURE [App::DocumentObjectGroupPython] Os_element001  label="Os_element : 1"  # scripted group (container) (typed FeaturePython)
  n = 1
  ref = Os_element
FEATURE [App::DocumentObjectGroupPython] G4_Os  # scripted group (container) (typed FeaturePython)
  Dunit = g/cm3
  Dvalue = 22.57
  Group = -> [Os_element001]
  conduct = 2
  density = 1
  expand = 3
  formula = Os
  name = G4_Os
  specific = 4
FEATURE [App::DocumentObjectGroupPython] Ir_element001  label="Ir_element : 1"  # scripted group (container) (typed FeaturePython)
  n = 1
  ref = Ir_element
FEATURE [App::DocumentObjectGroupPython] G4_Ir  # scripted group (container) (typed FeaturePython)
  Dunit = g/cm3
  Dvalue = 22.42
  Group = -> [Ir_element001]
  conduct = 2
  density = 1
  expand = 3
  formula = Ir
  name = G4_Ir
  specific = 4
FEATURE [App::DocumentObjectGroupPython] Pt_element001  label="Pt_element : 1"  # scripted group (container) (typed FeaturePython)
  n = 1
  ref = Pt_element
FEATURE [App::DocumentObjectGroupPython] G4_Pt  # scripted group (container) (typed FeaturePython)
  Dunit = g/cm3
  Dvalue = 21.45
  Group = -> [Pt_element001]
  conduct = 2
  density = 1
  expand = 3
  formula = Pt
  name = G4_Pt
  specific = 4
FEATURE [App::DocumentObjectGroupPython] Au_element001  label="Au_element : 1"  # scripted group (container) (typed FeaturePython)
  n = 1
  ref = Au_element
FEATURE [App::DocumentObjectGroupPython] G4_Au  # scripted group (container) (typed FeaturePython)
  Dunit = g/cm3
  Dvalue = 19.32
  Group = -> [Au_element001]
  conduct = 2
  density = 1
  expand = 3
  formula = Au
  name = G4_Au
  specific = 4
FEATURE [App::DocumentObjectGroupPython] Hg_element002  label="Hg_element : 002"  # scripted group (container) (typed FeaturePython)
  n = 1
  ref = Hg_element
FEATURE [App::DocumentObjectGroupPython] G4_Hg  # scripted group (container) (typed FeaturePython)
  Dunit = g/cm3
  Dvalue = 13.546
  Group = -> [Hg_element002]
  conduct = 2
  density = 1
  expand = 3
  formula = Hg
  name = G4_Hg
  specific = 4
FEATURE [App::DocumentObjectGroupPython] Tl_element002  label="Tl_element : 002"  # scripted group (container) (typed FeaturePython)
  n = 1
  ref = Tl_element
FEATURE [App::DocumentObjectGroupPython] G4_Tl  # scripted group (container) (typed FeaturePython)
  Dunit = g/cm3
  Dvalue = 11.72
  Group = -> [Tl_element002]
  conduct = 2
  density = 1
  expand = 3
  formula = Tl
  name = G4_Tl
  specific = 4
FEATURE [App::DocumentObjectGroupPython] Pb_element003  label="Pb_element : 1"  # scripted group (container) (typed FeaturePython)
  n = 1
  ref = Pb_element
FEATURE [App::DocumentObjectGroupPython] G4_Pb  # scripted group (container) (typed FeaturePython)
  Dunit = g/cm3
  Dvalue = 11.35
  Group = -> [Pb_element003]
  conduct = 2
  density = 1
  expand = 3
  formula = Pb
  name = G4_Pb
  specific = 4
FEATURE [App::DocumentObjectGroupPython] Bi_element002  label="Bi_element : 1"  # scripted group (container) (typed FeaturePython)
  n = 1
  ref = Bi_element
FEATURE [App::DocumentObjectGroupPython] G4_Bi  # scripted group (container) (typed FeaturePython)
  Dunit = g/cm3
  Dvalue = 9.747
  Group = -> [Bi_element002]
  conduct = 2
  density = 1
  expand = 3
  formula = Bi
  name = G4_Bi
  specific = 4
FEATURE [App::DocumentObjectGroupPython] Po_element001  label="Po_element : 1"  # scripted group (container) (typed FeaturePython)
  n = 1
  ref = Po_element
FEATURE [App::DocumentObjectGroupPython] G4_Po  # scripted group (container) (typed FeaturePython)
  Dunit = g/cm3
  Dvalue = 9.32
  Group = -> [Po_element001]
  conduct = 2
  density = 1
  expand = 3
  formula = Po
  name = G4_Po
  specific = 4
FEATURE [App::DocumentObjectGroupPython] At_element001  label="At_element : 1"  # scripted group (container) (typed FeaturePython)
  n = 1
  ref = At_element
FEATURE [App::DocumentObjectGroupPython] G4_At  # scripted group (container) (typed FeaturePython)
  Dunit = g/cm3
  Dvalue = 9.32
  Group = -> [At_element001]
  conduct = 2
  density = 1
  expand = 3
  formula = At
  name = G4_At
  specific = 4
FEATURE [App::DocumentObjectGroupPython] Rn_element001  label="Rn_element : 1"  # scripted group (container) (typed FeaturePython)
  n = 1
  ref = Rn_element
FEATURE [App::DocumentObjectGroupPython] G4_Rn  # scripted group (container) (typed FeaturePython)
  Dunit = g/cm3
  Dvalue = 0.00900662
  Group = -> [Rn_element001]
  conduct = 2
  density = 1
  expand = 3
  formula = Rn
  name = G4_Rn
  specific = 4
FEATURE [App::DocumentObjectGroupPython] Fr_element001  label="Fr_element : 1"  # scripted group (container) (typed FeaturePython)
  n = 1
  ref = Fr_element
FEATURE [App::DocumentObjectGroupPython] G4_Fr  # scripted group (container) (typed FeaturePython)
  Dunit = g/cm3
  Dvalue = 1
  Group = -> [Fr_element001]
  conduct = 2
  density = 1
  expand = 3
  formula = Fr
  name = G4_Fr
  specific = 4
FEATURE [App::DocumentObjectGroupPython] Ra_element001  label="Ra_element : 1"  # scripted group (container) (typed FeaturePython)
  n = 1
  ref = Ra_element
FEATURE [App::DocumentObjectGroupPython] G4_Ra  # scripted group (container) (typed FeaturePython)
  Dunit = g/cm3
  Dvalue = 5
  Group = -> [Ra_element001]
  conduct = 2
  density = 1
  expand = 3
  formula = Ra
  name = G4_Ra
  specific = 4
FEATURE [App::DocumentObjectGroupPython] Ac_element001  label="Ac_element : 1"  # scripted group (container) (typed FeaturePython)
  n = 1
  ref = Ac_element
FEATURE [App::DocumentObjectGroupPython] G4_Ac  # scripted group (container) (typed FeaturePython)
  Dunit = g/cm3
  Dvalue = 10.07
  Group = -> [Ac_element001]
  conduct = 2
  density = 1
  expand = 3
  formula = Ac
  name = G4_Ac
  specific = 4
FEATURE [App::DocumentObjectGroupPython] Th_element001  label="Th_element : 1"  # scripted group (container) (typed FeaturePython)
  n = 1
  ref = Th_element
FEATURE [App::DocumentObjectGroupPython] G4_Th  # scripted group (container) (typed FeaturePython)
  Dunit = g/cm3
  Dvalue = 11.72
  Group = -> [Th_element001]
  conduct = 2
  density = 1
  expand = 3
  formula = Th
  name = G4_Th
  specific = 4
FEATURE [App::DocumentObjectGroupPython] Pa_element001  label="Pa_element : 1"  # scripted group (container) (typed FeaturePython)
  n = 1
  ref = Pa_element
FEATURE [App::DocumentObjectGroupPython] G4_Pa  # scripted group (container) (typed FeaturePython)
  Dunit = g/cm3
  Dvalue = 15.37
  Group = -> [Pa_element001]
  conduct = 2
  density = 1
  expand = 3
  formula = Pa
  name = G4_Pa
  specific = 4
FEATURE [App::DocumentObjectGroupPython] U_element004  label="U_element : 004"  # scripted group (container) (typed FeaturePython)
  n = 1
  ref = U_element
FEATURE [App::DocumentObjectGroupPython] G4_U  # scripted group (container) (typed FeaturePython)
  Dunit = g/cm3
  Dvalue = 18.95
  Group = -> [U_element004]
  conduct = 2
  density = 1
  expand = 3
  formula = U
  name = G4_U
  specific = 4
FEATURE [App::DocumentObjectGroupPython] Np_element001  label="Np_element : 1"  # scripted group (container) (typed FeaturePython)
  n = 1
  ref = Np_element
FEATURE [App::DocumentObjectGroupPython] G4_Np  # scripted group (container) (typed FeaturePython)
  Dunit = g/cm3
  Dvalue = 20.25
  Group = -> [Np_element001]
  conduct = 2
  density = 1
  expand = 3
  formula = Np
  name = G4_Np
  specific = 4
FEATURE [App::DocumentObjectGroupPython] Pu_element002  label="Pu_element : 002"  # scripted group (container) (typed FeaturePython)
  n = 1
  ref = Pu_element
FEATURE [App::DocumentObjectGroupPython] G4_Pu  # scripted group (container) (typed FeaturePython)
  Dunit = g/cm3
  Dvalue = 19.84
  Group = -> [Pu_element002]
  conduct = 2
  density = 1
  expand = 3
  formula = Pu
  name = G4_Pu
  specific = 4
FEATURE [App::DocumentObjectGroupPython] Am_element001  label="Am_element : 1"  # scripted group (container) (typed FeaturePython)
  n = 1
  ref = Am_element
FEATURE [App::DocumentObjectGroupPython] G4_Am  # scripted group (container) (typed FeaturePython)
  Dunit = g/cm3
  Dvalue = 13.67
  Group = -> [Am_element001]
  conduct = 2
  density = 1
  expand = 3
  formula = Am
  name = G4_Am
  specific = 4
FEATURE [App::DocumentObjectGroupPython] Cm_element001  label="Cm_element : 1"  # scripted group (container) (typed FeaturePython)
  n = 1
  ref = Cm_element
FEATURE [App::DocumentObjectGroupPython] G4_Cm  # scripted group (container) (typed FeaturePython)
  Dunit = g/cm3
  Dvalue = 13.51
  Group = -> [Cm_element001]
  conduct = 2
  density = 1
  expand = 3
  formula = Cm
  name = G4_Cm
  specific = 4
FEATURE [App::DocumentObjectGroupPython] Bk_element001  label="Bk_element : 1"  # scripted group (container) (typed FeaturePython)
  n = 1
  ref = Bk_element
FEATURE [App::DocumentObjectGroupPython] G4_Bk  # scripted group (container) (typed FeaturePython)
  Dunit = g/cm3
  Dvalue = 14
  Group = -> [Bk_element001]
  conduct = 2
  density = 1
  expand = 3
  formula = Bk
  name = G4_Bk
  specific = 4
FEATURE [App::DocumentObjectGroupPython] Cf_element001  label="Cf_element : 1"  # scripted group (container) (typed FeaturePython)
  n = 1
  ref = Cf_element
FEATURE [App::DocumentObjectGroupPython] G4_Cf  # scripted group (container) (typed FeaturePython)
  Dunit = g/cm3
  Dvalue = 10
  Group = -> [Cf_element001]
  conduct = 2
  density = 1
  expand = 3
  formula = Cf
  name = G4_Cf
  specific = 4
FEATURE [App::DocumentObjectGroupPython] Element  # scripted group (container) (typed FeaturePython)
  Group = -> [G4_H,G4_He,G4_Li,G4_Be,G4_B,G4_C,G4_N,G4_O,G4_F,G4_Ne,G4_Na,G4_Mg,G4_Al,G4_Si,G4_P,G4_S,G4_Cl,G4_Ar,G4_K,G4_Ca,G4_Sc,G4_Ti,G4_V,G4_Cr,G4_Mn,G4_Fe,G4_Co,G4_Ni,G4_Cu,G4_Zn,G4_Ga,G4_Ge,G4_As,G4_Se,G4_Br,G4_Kr,G4_Rb,G4_Sr,G4_Y,G4_Zr,G4_Nb,G4_Mo,G4_Tc,G4_Ru,G4_Rh,G4_Pd,G4_Ag,G4_Cd,G4_In,G4_Sn,G4_Sb,G4_Te,G4_I,G4_Xe,G4_Cs,G4_Ba,G4_La,G4_Ce,G4_Pr,G4_Nd,G4_Pm,G4_Sm,G4_Eu,G4_Gd,G4_Tb,G4_Dy,G4_Ho,G4_Er,+30 more]
FEATURE [App::DocumentObjectGroupPython] H_element114  label="H_element : 063"  # scripted group (container) (typed FeaturePython)
  n = 2
  ref = H_element
FEATURE [App::DocumentObjectGroupPython] G4_lH2  # scripted group (container) (typed FeaturePython)
  Dunit = g/cm3
  Dvalue = 0.0708
  Group = -> [H_element114]
  conduct = 2
  density = 1
  expand = 3
  formula = G4_lH2
  name = G4_lH2
  specific = 4
FEATURE [App::DocumentObjectGroupPython] N_element049  label="N_element : 022"  # scripted group (container) (typed FeaturePython)
  n = 2
  ref = N_element
FEATURE [App::DocumentObjectGroupPython] G4_lN2  # scripted group (container) (typed FeaturePython)
  Dunit = g/cm3
  Dvalue = 0.807
  Group = -> [N_element049]
  conduct = 2
  density = 1
  expand = 3
  formula = G4_lN2
  name = G4_lN2
  specific = 4
FEATURE [App::DocumentObjectGroupPython] O_element106  label="O_element : 060"  # scripted group (container) (typed FeaturePython)
  n = 2
  ref = O_element
FEATURE [App::DocumentObjectGroupPython] G4_lO2  # scripted group (container) (typed FeaturePython)
  Dunit = g/cm3
  Dvalue = 1.141
  Group = -> [O_element106]
  conduct = 2
  density = 1
  expand = 3
  formula = G4_lO2
  name = G4_lO2
  specific = 4
FEATURE [App::DocumentObjectGroupPython] Ar_element003  label="Ar_element : 002"  # scripted group (container) (typed FeaturePython)
  n = 1
  ref = Ar_element
FEATURE [App::DocumentObjectGroupPython] G4_lAr  # scripted group (container) (typed FeaturePython)
  Dunit = g/cm3
  Dvalue = 1.396
  Group = -> [Ar_element003]
  conduct = 2
  density = 1
  expand = 3
  formula = G4_lAr
  name = G4_lAr
  specific = 4
FEATURE [App::DocumentObjectGroupPython] Br_element008  label="Br_element : 005"  # scripted group (container) (typed FeaturePython)
  n = 1
  ref = Br_element
FEATURE [App::DocumentObjectGroupPython] G4_lBr  # scripted group (container) (typed FeaturePython)
  Dunit = g/cm3
  Dvalue = 3.1028
  Group = -> [Br_element008]
  conduct = 2
  density = 1
  expand = 3
  formula = G4_lBr
  name = G4_lBr
  specific = 4
FEATURE [App::DocumentObjectGroupPython] Kr_element002  label="Kr_element : 002"  # scripted group (container) (typed FeaturePython)
  n = 1
  ref = Kr_element
FEATURE [App::DocumentObjectGroupPython] G4_lKr  # scripted group (container) (typed FeaturePython)
  Dunit = g/cm3
  Dvalue = 2.418
  Group = -> [Kr_element002]
  conduct = 2
  density = 1
  expand = 3
  formula = G4_lKr
  name = G4_lKr
  specific = 4
FEATURE [App::DocumentObjectGroupPython] Xe_element002  label="Xe_element : 002"  # scripted group (container) (typed FeaturePython)
  n = 1
  ref = Xe_element
FEATURE [App::DocumentObjectGroupPython] G4_lXe  # scripted group (container) (typed FeaturePython)
  Dunit = g/cm3
  Dvalue = 2.953
  Group = -> [Xe_element002]
  conduct = 2
  density = 1
  expand = 3
  formula = G4_lXe
  name = G4_lXe
  specific = 4
FEATURE [App::DocumentObjectGroupPython] O_element107  label="O_element : 061"  # scripted group (container) (typed FeaturePython)
  n = 4
  ref = O_element
FEATURE [App::DocumentObjectGroupPython] Pb_element004  label="Pb_element : 002"  # scripted group (container) (typed FeaturePython)
  n = 1
  ref = Pb_element
FEATURE [App::DocumentObjectGroupPython] W_element005  label="W_element : 005"  # scripted group (container) (typed FeaturePython)
  n = 1
  ref = W_element
FEATURE [App::DocumentObjectGroupPython] G4_PbWO4  # scripted group (container) (typed FeaturePython)
  Dunit = g/cm3
  Dvalue = 8.28
  Group = -> [O_element107,Pb_element004,W_element005]
  conduct = 2
  density = 1
  expand = 3
  formula = G4_PbWO4
  name = G4_PbWO4
  specific = 4
FEATURE [App::DocumentObjectGroupPython] H_element115  label="H_element : 064"  # scripted group (container) (typed FeaturePython)
  n = 1
  ref = H_element
FEATURE [App::DocumentObjectGroupPython] G4_Galactic  # scripted group (container) (typed FeaturePython)
  Dunit = g/cm3
  Dvalue = 0
  Group = -> [H_element115]
  conduct = 2
  density = 1
  expand = 3
  formula = G4_Galactic
  name = G4_Galactic
  specific = 4
FEATURE [App::DocumentObjectGroupPython] C_element125  label="C_element : 071"  # scripted group (container) (typed FeaturePython)
  n = 1
  ref = C_element
FEATURE [App::DocumentObjectGroupPython] G4_GRAPHITE_POROUS  # scripted group (container) (typed FeaturePython)
  Dunit = g/cm3
  Dvalue = 1.7
  Group = -> [C_element125]
  conduct = 2
  density = 1
  expand = 3
  formula = G4_GRAPHITE_POROUS
  name = G4_GRAPHITE_POROUS
  specific = 4
FEATURE [App::DocumentObjectGroupPython] H_element116  label="H_element : 0.150"  # scripted group (container) (typed FeaturePython)
  n = 0.080538
FEATURE [App::DocumentObjectGroupPython] C_element126  label="C_element : 0.600"  # scripted group (container) (typed FeaturePython)
  n = 0.599848
FEATURE [App::DocumentObjectGroupPython] O_element108  label="O_element : 0.320"  # scripted group (container) (typed FeaturePython)
  n = 0.319614
FEATURE [App::DocumentObjectGroupPython] G4_LUCITE  # scripted group (container) (typed FeaturePython)
  Dunit = g/cm3
  Dvalue = 1.19
  Group = -> [H_element116,C_element126,O_element108]
  conduct = 2
  density = 1
  expand = 3
  formula = G4_LUCITE
  name = G4_LUCITE
  specific = 4
FEATURE [App::DocumentObjectGroupPython] Cu_element002  label="Cu_element : 62"  # scripted group (container) (typed FeaturePython)
  n = 62
  ref = Cu_element
FEATURE [App::DocumentObjectGroupPython] Zn_element002  label="Zn_element : 35"  # scripted group (container) (typed FeaturePython)
  n = 35
  ref = Zn_element
FEATURE [App::DocumentObjectGroupPython] Pb_element005  label="Pb_element : 3"  # scripted group (container) (typed FeaturePython)
  n = 3
  ref = Pb_element
FEATURE [App::DocumentObjectGroupPython] G4_BRASS  # scripted group (container) (typed FeaturePython)
  Dunit = g/cm3
  Dvalue = 8.52
  Group = -> [Cu_element002,Zn_element002,Pb_element005]
  conduct = 2
  density = 1
  expand = 3
  formula = G4_BRASS
  name = G4_BRASS
  specific = 4
FEATURE [App::DocumentObjectGroupPython] Cu_element003  label="Cu_element : 89"  # scripted group (container) (typed FeaturePython)
  n = 89
  ref = Cu_element
FEATURE [App::DocumentObjectGroupPython] Zn_element003  label="Zn_element : 9"  # scripted group (container) (typed FeaturePython)
  n = 9
  ref = Zn_element
FEATURE [App::DocumentObjectGroupPython] Pb_element006  label="Pb_element : 2"  # scripted group (container) (typed FeaturePython)
  n = 2
  ref = Pb_element
FEATURE [App::DocumentObjectGroupPython] G4_BRONZE  # scripted group (container) (typed FeaturePython)
  Dunit = g/cm3
  Dvalue = 8.82
  Group = -> [Cu_element003,Zn_element003,Pb_element006]
  conduct = 2
  density = 1
  expand = 3
  formula = G4_BRONZE
  name = G4_BRONZE
  specific = 4
FEATURE [App::DocumentObjectGroupPython] Fe_element008  label="Fe_element : 74"  # scripted group (container) (typed FeaturePython)
  n = 74
  ref = Fe_element
FEATURE [App::DocumentObjectGroupPython] Cr_element002  label="Cr_element : 18"  # scripted group (container) (typed FeaturePython)
  n = 18
  ref = Cr_element
FEATURE [App::DocumentObjectGroupPython] Ni_element002  label="Ni_element : 8"  # scripted group (container) (typed FeaturePython)
  n = 8
  ref = Ni_element
FEATURE [App::DocumentObjectGroupPython] G4_STAINLESS_STEEL  label="G4_STAINLESS-STEEL"  # scripted group (container) (typed FeaturePython)
  Dunit = g/cm3
  Dvalue = 8
  Group = -> [Fe_element008,Cr_element002,Ni_element002]
  conduct = 2
  density = 1
  expand = 3
  formula = G4_STAINLESS-STEEL
  name = G4_STAINLESS-STEEL
  specific = 4
FEATURE [App::DocumentObjectGroupPython] H_element117  label="H_element : 065"  # scripted group (container) (typed FeaturePython)
  n = 18
  ref = H_element
FEATURE [App::DocumentObjectGroupPython] C_element127  label="C_element : 072"  # scripted group (container) (typed FeaturePython)
  n = 12
  ref = C_element
FEATURE [App::DocumentObjectGroupPython] O_element109  label="O_element : 062"  # scripted group (container) (typed FeaturePython)
  n = 7
  ref = O_element
FEATURE [App::DocumentObjectGroupPython] G4_CR39  # scripted group (container) (typed FeaturePython)
  Dunit = g/cm3
  Dvalue = 1.32
  Group = -> [H_element117,C_element127,O_element109]
  conduct = 2
  density = 1
  expand = 3
  formula = G4_CR39
  name = G4_CR39
  specific = 4
FEATURE [App::DocumentObjectGroupPython] H_element118  label="H_element : 38"  # scripted group (container) (typed FeaturePython)
  n = 38
  ref = H_element
FEATURE [App::DocumentObjectGroupPython] C_element128  label="C_element : 073"  # scripted group (container) (typed FeaturePython)
  n = 18
  ref = C_element
FEATURE [App::DocumentObjectGroupPython] O_element110  label="O_element : 063"  # scripted group (container) (typed FeaturePython)
  n = 1
  ref = O_element
FEATURE [App::DocumentObjectGroupPython] G4_OCTADECANOL  # scripted group (container) (typed FeaturePython)
  Dunit = g/cm3
  Dvalue = 0.812
  Group = -> [H_element118,C_element128,O_element110]
  conduct = 2
  density = 1
  expand = 3
  formula = G4_OCTADECANOL
  name = G4_OCTADECANOL
  specific = 4
FEATURE [App::DocumentObjectGroupPython] HEP  # scripted group (container) (typed FeaturePython)
  Group = -> [G4_lH2,G4_lN2,G4_lO2,G4_lAr,G4_lBr,G4_lKr,G4_lXe,G4_PbWO4,G4_Galactic,G4_GRAPHITE_POROUS,G4_LUCITE,G4_BRASS,G4_BRONZE,G4_STAINLESS_STEEL,G4_CR39,G4_OCTADECANOL]
FEATURE [App::DocumentObjectGroupPython] C_element129  label="C_element : 074"  # scripted group (container) (typed FeaturePython)
  n = 14
  ref = C_element
FEATURE [App::DocumentObjectGroupPython] H_element119  label="H_element : 066"  # scripted group (container) (typed FeaturePython)
  n = 10
  ref = H_element
FEATURE [App::DocumentObjectGroupPython] O_element111  label="O_element : 064"  # scripted group (container) (typed FeaturePython)
  n = 2
  ref = O_element
FEATURE [App::DocumentObjectGroupPython] N_element050  label="N_element : 023"  # scripted group (container) (typed FeaturePython)
  n = 2
  ref = N_element
FEATURE [App::DocumentObjectGroupPython] G4_KEVLAR  # scripted group (container) (typed FeaturePython)
  Dunit = g/cm3
  Dvalue = 1.44
  Group = -> [C_element129,H_element119,O_element111,N_element050]
  conduct = 2
  density = 1
  expand = 3
  formula = G4_KEVLAR
  name = G4_KEVLAR
  specific = 4
FEATURE [App::DocumentObjectGroupPython] C_element130  label="C_element : 075"  # scripted group (container) (typed FeaturePython)
  n = 10
  ref = C_element
FEATURE [App::DocumentObjectGroupPython] H_element120  label="H_element : 067"  # scripted group (container) (typed FeaturePython)
  n = 8
  ref = H_element
FEATURE [App::DocumentObjectGroupPython] O_element112  label="O_element : 065"  # scripted group (container) (typed FeaturePython)
  n = 4
  ref = O_element
FEATURE [App::DocumentObjectGroupPython] G4_DACRON  # scripted group (container) (typed FeaturePython)
  Dunit = g/cm3
  Dvalue = 1.4
  Group = -> [C_element130,H_element120,O_element112]
  conduct = 2
  density = 1
  expand = 3
  formula = G4_DACRON
  name = G4_DACRON
  specific = 4
FEATURE [App::DocumentObjectGroupPython] C_element131  label="C_element : 076"  # scripted group (container) (typed FeaturePython)
  n = 4
  ref = C_element
FEATURE [App::DocumentObjectGroupPython] H_element121  label="H_element : 068"  # scripted group (container) (typed FeaturePython)
  n = 5
  ref = H_element
FEATURE [App::DocumentObjectGroupPython] Cl_element030  label="Cl_element : 016"  # scripted group (container) (typed FeaturePython)
  n = 1
  ref = Cl_element
FEATURE [App::DocumentObjectGroupPython] G4_NEOPRENE  # scripted group (container) (typed FeaturePython)
  Dunit = g/cm3
  Dvalue = 1.23
  Group = -> [C_element131,H_element121,Cl_element030]
  conduct = 2
  density = 1
  expand = 3
  formula = G4_NEOPRENE
  name = G4_NEOPRENE
  specific = 4
FEATURE [App::DocumentObjectGroupPython] Space  # scripted group (container) (typed FeaturePython)
  Group = -> [G4_KEVLAR,G4_DACRON,G4_NEOPRENE]
FEATURE [App::DocumentObjectGroupPython] H_element122  label="H_element : 069"  # scripted group (container) (typed FeaturePython)
  n = 5
  ref = H_element
FEATURE [App::DocumentObjectGroupPython] C_element132  label="C_element : 077"  # scripted group (container) (typed FeaturePython)
  n = 4
  ref = C_element
FEATURE [App::DocumentObjectGroupPython] N_element051  label="N_element : 3"  # scripted group (container) (typed FeaturePython)
  n = 3
  ref = N_element
FEATURE [App::DocumentObjectGroupPython] O_element113  label="O_element : 066"  # scripted group (container) (typed FeaturePython)
  n = 1
  ref = O_element
FEATURE [App::DocumentObjectGroupPython] G4_CYTOSINE  # scripted group (container) (typed FeaturePython)
  Dunit = g/cm3
  Dvalue = 1.55
  Group = -> [H_element122,C_element132,N_element051,O_element113]
  conduct = 2
  density = 1
  expand = 3
  formula = G4_CYTOSINE
  name = G4_CYTOSINE
  specific = 4
FEATURE [App::DocumentObjectGroupPython] H_element123  label="H_element : 070"  # scripted group (container) (typed FeaturePython)
  n = 6
  ref = H_element
FEATURE [App::DocumentObjectGroupPython] C_element133  label="C_element : 078"  # scripted group (container) (typed FeaturePython)
  n = 5
  ref = C_element
FEATURE [App::DocumentObjectGroupPython] N_element052  label="N_element : 024"  # scripted group (container) (typed FeaturePython)
  n = 2
  ref = N_element
FEATURE [App::DocumentObjectGroupPython] O_element114  label="O_element : 067"  # scripted group (container) (typed FeaturePython)
  n = 2
  ref = O_element
FEATURE [App::DocumentObjectGroupPython] G4_THYMINE  # scripted group (container) (typed FeaturePython)
  Dunit = g/cm3
  Dvalue = 1.23
  Group = -> [H_element123,C_element133,N_element052,O_element114]
  conduct = 2
  density = 1
  expand = 3
  formula = G4_THYMINE
  name = G4_THYMINE
  specific = 4
FEATURE [App::DocumentObjectGroupPython] H_element124  label="H_element : 071"  # scripted group (container) (typed FeaturePython)
  n = 4
  ref = H_element
FEATURE [App::DocumentObjectGroupPython] C_element134  label="C_element : 079"  # scripted group (container) (typed FeaturePython)
  n = 4
  ref = C_element
FEATURE [App::DocumentObjectGroupPython] N_element053  label="N_element : 025"  # scripted group (container) (typed FeaturePython)
  n = 2
  ref = N_element
FEATURE [App::DocumentObjectGroupPython] O_element115  label="O_element : 068"  # scripted group (container) (typed FeaturePython)
  n = 2
  ref = O_element
FEATURE [App::DocumentObjectGroupPython] G4_URACIL  # scripted group (container) (typed FeaturePython)
  Dunit = g/cm3
  Dvalue = 1.32
  Group = -> [H_element124,C_element134,N_element053,O_element115]
  conduct = 2
  density = 1
  expand = 3
  formula = G4_URACIL
  name = G4_URACIL
  specific = 4
FEATURE [App::DocumentObjectGroupPython] H_element125  label="H_element : 072"  # scripted group (container) (typed FeaturePython)
  n = 4
  ref = H_element
FEATURE [App::DocumentObjectGroupPython] C_element135  label="C_element : 080"  # scripted group (container) (typed FeaturePython)
  n = 5
  ref = C_element
FEATURE [App::DocumentObjectGroupPython] N_element054  label="N_element : 026"  # scripted group (container) (typed FeaturePython)
  n = 5
  ref = N_element
FEATURE [App::DocumentObjectGroupPython] G4_DNA_ADENINE  # scripted group (container) (typed FeaturePython)
  Dunit = g/cm3
  Dvalue = 1
  Group = -> [H_element125,C_element135,N_element054]
  conduct = 2
  density = 1
  expand = 3
  formula = G4_DNA_ADENINE
  name = G4_DNA_ADENINE
  specific = 4
FEATURE [App::DocumentObjectGroupPython] H_element126  label="H_element : 073"  # scripted group (container) (typed FeaturePython)
  n = 4
  ref = H_element
FEATURE [App::DocumentObjectGroupPython] C_element136  label="C_element : 081"  # scripted group (container) (typed FeaturePython)
  n = 5
  ref = C_element
FEATURE [App::DocumentObjectGroupPython] N_element055  label="N_element : 027"  # scripted group (container) (typed FeaturePython)
  n = 5
  ref = N_element
FEATURE [App::DocumentObjectGroupPython] O_element116  label="O_element : 069"  # scripted group (container) (typed FeaturePython)
  n = 1
  ref = O_element
FEATURE [App::DocumentObjectGroupPython] G4_DNA_GUANINE  # scripted group (container) (typed FeaturePython)
  Dunit = g/cm3
  Dvalue = 1
  Group = -> [H_element126,C_element136,N_element055,O_element116]
  conduct = 2
  density = 1
  expand = 3
  formula = G4_DNA_GUANINE
  name = G4_DNA_GUANINE
  specific = 4
FEATURE [App::DocumentObjectGroupPython] H_element127  label="H_element : 074"  # scripted group (container) (typed FeaturePython)
  n = 4
  ref = H_element
FEATURE [App::DocumentObjectGroupPython] C_element137  label="C_element : 082"  # scripted group (container) (typed FeaturePython)
  n = 4
  ref = C_element
FEATURE [App::DocumentObjectGroupPython] N_element056  label="N_element : 028"  # scripted group (container) (typed FeaturePython)
  n = 3
  ref = N_element
FEATURE [App::DocumentObjectGroupPython] O_element117  label="O_element : 070"  # scripted group (container) (typed FeaturePython)
  n = 1
  ref = O_element
FEATURE [App::DocumentObjectGroupPython] G4_DNA_CYTOSINE  # scripted group (container) (typed FeaturePython)
  Dunit = g/cm3
  Dvalue = 1
  Group = -> [H_element127,C_element137,N_element056,O_element117]
  conduct = 2
  density = 1
  expand = 3
  formula = G4_DNA_CYTOSINE
  name = G4_DNA_CYTOSINE
  specific = 4
FEATURE [App::DocumentObjectGroupPython] H_element128  label="H_element : 075"  # scripted group (container) (typed FeaturePython)
  n = 5
  ref = H_element
FEATURE [App::DocumentObjectGroupPython] C_element138  label="C_element : 083"  # scripted group (container) (typed FeaturePython)
  n = 5
  ref = C_element
FEATURE [App::DocumentObjectGroupPython] N_element057  label="N_element : 029"  # scripted group (container) (typed FeaturePython)
  n = 2
  ref = N_element
FEATURE [App::DocumentObjectGroupPython] O_element118  label="O_element : 071"  # scripted group (container) (typed FeaturePython)
  n = 2
  ref = O_element
FEATURE [App::DocumentObjectGroupPython] G4_DNA_THYMINE  # scripted group (container) (typed FeaturePython)
  Dunit = g/cm3
  Dvalue = 1
  Group = -> [H_element128,C_element138,N_element057,O_element118]
  conduct = 2
  density = 1
  expand = 3
  formula = G4_DNA_THYMINE
  name = G4_DNA_THYMINE
  specific = 4
FEATURE [App::DocumentObjectGroupPython] H_element129  label="H_element : 076"  # scripted group (container) (typed FeaturePython)
  n = 3
  ref = H_element
FEATURE [App::DocumentObjectGroupPython] C_element139  label="C_element : 084"  # scripted group (container) (typed FeaturePython)
  n = 4
  ref = C_element
FEATURE [App::DocumentObjectGroupPython] N_element058  label="N_element : 030"  # scripted group (container) (typed FeaturePython)
  n = 2
  ref = N_element
FEATURE [App::DocumentObjectGroupPython] O_element119  label="O_element : 072"  # scripted group (container) (typed FeaturePython)
  n = 2
  ref = O_element
FEATURE [App::DocumentObjectGroupPython] G4_DNA_URACIL  # scripted group (container) (typed FeaturePython)
  Dunit = g/cm3
  Dvalue = 1
  Group = -> [H_element129,C_element139,N_element058,O_element119]
  conduct = 2
  density = 1
  expand = 3
  formula = G4_DNA_URACIL
  name = G4_DNA_URACIL
  specific = 4
FEATURE [App::DocumentObjectGroupPython] H_element130  label="H_element : 077"  # scripted group (container) (typed FeaturePython)
  n = 10
  ref = H_element
FEATURE [App::DocumentObjectGroupPython] C_element140  label="C_element : 085"  # scripted group (container) (typed FeaturePython)
  n = 10
  ref = C_element
FEATURE [App::DocumentObjectGroupPython] N_element059  label="N_element : 031"  # scripted group (container) (typed FeaturePython)
  n = 5
  ref = N_element
FEATURE [App::DocumentObjectGroupPython] O_element120  label="O_element : 073"  # scripted group (container) (typed FeaturePython)
  n = 4
  ref = O_element
FEATURE [App::DocumentObjectGroupPython] G4_DNA_ADENOSINE  # scripted group (container) (typed FeaturePython)
  Dunit = g/cm3
  Dvalue = 1
  Group = -> [H_element130,C_element140,N_element059,O_element120]
  conduct = 2
  density = 1
  expand = 3
  formula = G4_DNA_ADENOSINE
  name = G4_DNA_ADENOSINE
  specific = 4
FEATURE [App::DocumentObjectGroupPython] H_element131  label="H_element : 078"  # scripted group (container) (typed FeaturePython)
  n = 10
  ref = H_element
FEATURE [App::DocumentObjectGroupPython] C_element141  label="C_element : 086"  # scripted group (container) (typed FeaturePython)
  n = 10
  ref = C_element
FEATURE [App::DocumentObjectGroupPython] N_element060  label="N_element : 032"  # scripted group (container) (typed FeaturePython)
  n = 5
  ref = N_element
FEATURE [App::DocumentObjectGroupPython] O_element121  label="O_element : 074"  # scripted group (container) (typed FeaturePython)
  n = 5
  ref = O_element
FEATURE [App::DocumentObjectGroupPython] G4_DNA_GUANOSINE  # scripted group (container) (typed FeaturePython)
  Dunit = g/cm3
  Dvalue = 1
  Group = -> [H_element131,C_element141,N_element060,O_element121]
  conduct = 2
  density = 1
  expand = 3
  formula = G4_DNA_GUANOSINE
  name = G4_DNA_GUANOSINE
  specific = 4
FEATURE [App::DocumentObjectGroupPython] H_element132  label="H_element : 079"  # scripted group (container) (typed FeaturePython)
  n = 10
  ref = H_element
FEATURE [App::DocumentObjectGroupPython] C_element142  label="C_element : 087"  # scripted group (container) (typed FeaturePython)
  n = 9
  ref = C_element
FEATURE [App::DocumentObjectGroupPython] N_element061  label="N_element : 033"  # scripted group (container) (typed FeaturePython)
  n = 3
  ref = N_element
FEATURE [App::DocumentObjectGroupPython] O_element122  label="O_element : 075"  # scripted group (container) (typed FeaturePython)
  n = 5
  ref = O_element
FEATURE [App::DocumentObjectGroupPython] G4_DNA_CYTIDINE  # scripted group (container) (typed FeaturePython)
  Dunit = g/cm3
  Dvalue = 1
  Group = -> [H_element132,C_element142,N_element061,O_element122]
  conduct = 2
  density = 1
  expand = 3
  formula = G4_DNA_CYTIDINE
  name = G4_DNA_CYTIDINE
  specific = 4
FEATURE [App::DocumentObjectGroupPython] H_element133  label="H_element : 080"  # scripted group (container) (typed FeaturePython)
  n = 9
  ref = H_element
FEATURE [App::DocumentObjectGroupPython] C_element143  label="C_element : 088"  # scripted group (container) (typed FeaturePython)
  n = 9
  ref = C_element
FEATURE [App::DocumentObjectGroupPython] N_element062  label="N_element : 034"  # scripted group (container) (typed FeaturePython)
  n = 2
  ref = N_element
FEATURE [App::DocumentObjectGroupPython] O_element123  label="O_element : 076"  # scripted group (container) (typed FeaturePython)
  n = 6
  ref = O_element
FEATURE [App::DocumentObjectGroupPython] G4_DNA_URIDINE  # scripted group (container) (typed FeaturePython)
  Dunit = g/cm3
  Dvalue = 1
  Group = -> [H_element133,C_element143,N_element062,O_element123]
  conduct = 2
  density = 1
  expand = 3
  formula = G4_DNA_URIDINE
  name = G4_DNA_URIDINE
  specific = 4
FEATURE [App::DocumentObjectGroupPython] H_element134  label="H_element : 081"  # scripted group (container) (typed FeaturePython)
  n = 11
  ref = H_element
FEATURE [App::DocumentObjectGroupPython] C_element144  label="C_element : 089"  # scripted group (container) (typed FeaturePython)
  n = 10
  ref = C_element
FEATURE [App::DocumentObjectGroupPython] N_element063  label="N_element : 035"  # scripted group (container) (typed FeaturePython)
  n = 2
  ref = N_element
FEATURE [App::DocumentObjectGroupPython] O_element124  label="O_element : 077"  # scripted group (container) (typed FeaturePython)
  n = 6
  ref = O_element
FEATURE [App::DocumentObjectGroupPython] G4_DNA_METHYLURIDINE  # scripted group (container) (typed FeaturePython)
  Dunit = g/cm3
  Dvalue = 1
  Group = -> [H_element134,C_element144,N_element063,O_element124]
  conduct = 2
  density = 1
  expand = 3
  formula = G4_DNA_METHYLURIDINE
  name = G4_DNA_METHYLURIDINE
  specific = 4
FEATURE [App::DocumentObjectGroupPython] P_element014  label="P_element : 003"  # scripted group (container) (typed FeaturePython)
  n = 1
  ref = P_element
FEATURE [App::DocumentObjectGroupPython] O_element125  label="O_element : 078"  # scripted group (container) (typed FeaturePython)
  n = 3
  ref = O_element
FEATURE [App::DocumentObjectGroupPython] G4_DNA_MONOPHOSPHATE  # scripted group (container) (typed FeaturePython)
  Dunit = g/cm3
  Dvalue = 1
  Group = -> [P_element014,O_element125]
  conduct = 2
  density = 1
  expand = 3
  formula = G4_DNA_MONOPHOSPHATE
  name = G4_DNA_MONOPHOSPHATE
  specific = 4
FEATURE [App::DocumentObjectGroupPython] H_element135  label="H_element : 082"  # scripted group (container) (typed FeaturePython)
  n = 10
  ref = H_element
FEATURE [App::DocumentObjectGroupPython] C_element145  label="C_element : 090"  # scripted group (container) (typed FeaturePython)
  n = 10
  ref = C_element
FEATURE [App::DocumentObjectGroupPython] N_element064  label="N_element : 036"  # scripted group (container) (typed FeaturePython)
  n = 5
  ref = N_element
FEATURE [App::DocumentObjectGroupPython] O_element126  label="O_element : 079"  # scripted group (container) (typed FeaturePython)
  n = 7
  ref = O_element
FEATURE [App::DocumentObjectGroupPython] P_element015  label="P_element : 004"  # scripted group (container) (typed FeaturePython)
  n = 1
  ref = P_element
FEATURE [App::DocumentObjectGroupPython] G4_DNA_A  # scripted group (container) (typed FeaturePython)
  Dunit = g/cm3
  Dvalue = 1
  Group = -> [H_element135,C_element145,N_element064,O_element126,P_element015]
  conduct = 2
  density = 1
  expand = 3
  formula = G4_DNA_A
  name = G4_DNA_A
  specific = 4
FEATURE [App::DocumentObjectGroupPython] H_element136  label="H_element : 083"  # scripted group (container) (typed FeaturePython)
  n = 10
  ref = H_element
FEATURE [App::DocumentObjectGroupPython] C_element146  label="C_element : 091"  # scripted group (container) (typed FeaturePython)
  n = 10
  ref = C_element
FEATURE [App::DocumentObjectGroupPython] N_element065  label="N_element : 037"  # scripted group (container) (typed FeaturePython)
  n = 5
  ref = N_element
FEATURE [App::DocumentObjectGroupPython] O_element127  label="O_element : 8"  # scripted group (container) (typed FeaturePython)
  n = 8
  ref = O_element
FEATURE [App::DocumentObjectGroupPython] P_element016  label="P_element : 005"  # scripted group (container) (typed FeaturePython)
  n = 1
  ref = P_element
FEATURE [App::DocumentObjectGroupPython] G4_DNA_G  # scripted group (container) (typed FeaturePython)
  Dunit = g/cm3
  Dvalue = 1
  Group = -> [H_element136,C_element146,N_element065,O_element127,P_element016]
  conduct = 2
  density = 1
  expand = 3
  formula = G4_DNA_G
  name = G4_DNA_G
  specific = 4
FEATURE [App::DocumentObjectGroupPython] H_element137  label="H_element : 084"  # scripted group (container) (typed FeaturePython)
  n = 10
  ref = H_element
FEATURE [App::DocumentObjectGroupPython] C_element147  label="C_element : 092"  # scripted group (container) (typed FeaturePython)
  n = 9
  ref = C_element
FEATURE [App::DocumentObjectGroupPython] N_element066  label="N_element : 038"  # scripted group (container) (typed FeaturePython)
  n = 3
  ref = N_element
FEATURE [App::DocumentObjectGroupPython] O_element128  label="O_element : 080"  # scripted group (container) (typed FeaturePython)
  n = 8
  ref = O_element
FEATURE [App::DocumentObjectGroupPython] P_element017  label="P_element : 006"  # scripted group (container) (typed FeaturePython)
  n = 1
  ref = P_element
FEATURE [App::DocumentObjectGroupPython] G4_DNA_C  # scripted group (container) (typed FeaturePython)
  Dunit = g/cm3
  Dvalue = 1
  Group = -> [H_element137,C_element147,N_element066,O_element128,P_element017]
  conduct = 2
  density = 1
  expand = 3
  formula = G4_DNA_C
  name = G4_DNA_C
  specific = 4
FEATURE [App::DocumentObjectGroupPython] H_element138  label="H_element : 085"  # scripted group (container) (typed FeaturePython)
  n = 9
  ref = H_element
FEATURE [App::DocumentObjectGroupPython] C_element148  label="C_element : 093"  # scripted group (container) (typed FeaturePython)
  n = 9
  ref = C_element
FEATURE [App::DocumentObjectGroupPython] N_element067  label="N_element : 039"  # scripted group (container) (typed FeaturePython)
  n = 2
  ref = N_element
FEATURE [App::DocumentObjectGroupPython] O_element129  label="O_element : 9"  # scripted group (container) (typed FeaturePython)
  n = 9
  ref = O_element
FEATURE [App::DocumentObjectGroupPython] P_element018  label="P_element : 007"  # scripted group (container) (typed FeaturePython)
  n = 1
  ref = P_element
FEATURE [App::DocumentObjectGroupPython] G4_DNA_U  # scripted group (container) (typed FeaturePython)
  Dunit = g/cm3
  Dvalue = 1
  Group = -> [H_element138,C_element148,N_element067,O_element129,P_element018]
  conduct = 2
  density = 1
  expand = 3
  formula = G4_DNA_U
  name = G4_DNA_U
  specific = 4
FEATURE [App::DocumentObjectGroupPython] H_element139  label="H_element : 086"  # scripted group (container) (typed FeaturePython)
  n = 11
  ref = H_element
FEATURE [App::DocumentObjectGroupPython] C_element149  label="C_element : 094"  # scripted group (container) (typed FeaturePython)
  n = 10
  ref = C_element
FEATURE [App::DocumentObjectGroupPython] N_element068  label="N_element : 040"  # scripted group (container) (typed FeaturePython)
  n = 2
  ref = N_element
FEATURE [App::DocumentObjectGroupPython] O_element130  label="O_element : 081"  # scripted group (container) (typed FeaturePython)
  n = 9
  ref = O_element
FEATURE [App::DocumentObjectGroupPython] P_element019  label="P_element : 008"  # scripted group (container) (typed FeaturePython)
  n = 1
  ref = P_element
FEATURE [App::DocumentObjectGroupPython] G4_DNA_MU  # scripted group (container) (typed FeaturePython)
  Dunit = g/cm3
  Dvalue = 1
  Group = -> [H_element139,C_element149,N_element068,O_element130,P_element019]
  conduct = 2
  density = 1
  expand = 3
  formula = G4_DNA_MU
  name = G4_DNA_MU
  specific = 4
FEATURE [App::DocumentObjectGroupPython] BioChemical  # scripted group (container) (typed FeaturePython)
  Group = -> [G4_CYTOSINE,G4_THYMINE,G4_URACIL,G4_DNA_ADENINE,G4_DNA_GUANINE,G4_DNA_CYTOSINE,G4_DNA_THYMINE,G4_DNA_URACIL,G4_DNA_ADENOSINE,G4_DNA_GUANOSINE,G4_DNA_CYTIDINE,G4_DNA_URIDINE,G4_DNA_METHYLURIDINE,G4_DNA_MONOPHOSPHATE,G4_DNA_A,G4_DNA_G,G4_DNA_C,G4_DNA_U,G4_DNA_MU]
FEATURE [App::DocumentObjectGroupPython] G4Materials  # scripted group (container) (typed FeaturePython)
  Group = -> [NIST,Element,HEP,Space,BioChemical]
  version = 1
FEATURE [App::DocumentObjectGroupPython] Geant4  # scripted group (container) (typed FeaturePython)
  Group = -> [G4Isotopes,G4Elements,G4Materials]
FEATURE [App::DocumentObjectGroupPython] Materials  # scripted group (container) (typed FeaturePython)
  Group = -> [Al,Water,Air,Geant4]
FEATURE [Part::FeaturePython] GDMLBox_WorldBox  # WARN: FeaturePython — macro-defined, semantics opaque (R4)
  lunit = 2
  material = 2
  x = 10000
  y = 10000
  z = 10000
FEATURE [Part::FeaturePython] GDMLBox_b500  # WARN: FeaturePython — macro-defined, semantics opaque (R4)
  lunit = 2
  material = 1
  x = 50
  y = 50
  z = 50
FEATURE [Part::FeaturePython] GDMLBox_b501  # WARN: FeaturePython — macro-defined, semantics opaque (R4)
  Placement = pos=(25,0,0) rot=(0,0,1;0rad)
  lunit = 2
  material = 1
  x = 10
  y = 10
  z = 10
FEATURE [Part::Fuse] u1
  Base = -> GDMLBox_b500
  Tool = -> GDMLBox_b501
FEATURE [Part::FeaturePython] GDMLBox_b502  # WARN: FeaturePython — macro-defined, semantics opaque (R4)
  Placement = pos=(-25,0,0) rot=(0,0,1;0rad)
  lunit = 2
  material = 1
  x = 10
  y = 10
  z = 10
FEATURE [Part::Cut] sub1
  Base = -> u1
  Tool = -> GDMLBox_b502
FEATURE [App::Part] vol31
  Group = -> [sub1,u1,GDMLBox_b500,GDMLBox_b501,GDMLBox_b502]
  Origin = -> Origin008
  Placement = pos=(125,125,0) rot=(0,0,1;0rad)
  SkinSurface = 0
FEATURE [App::Part] World
  Group = -> [GDMLBox_WorldBox,vol31]
  Origin = -> Origin
